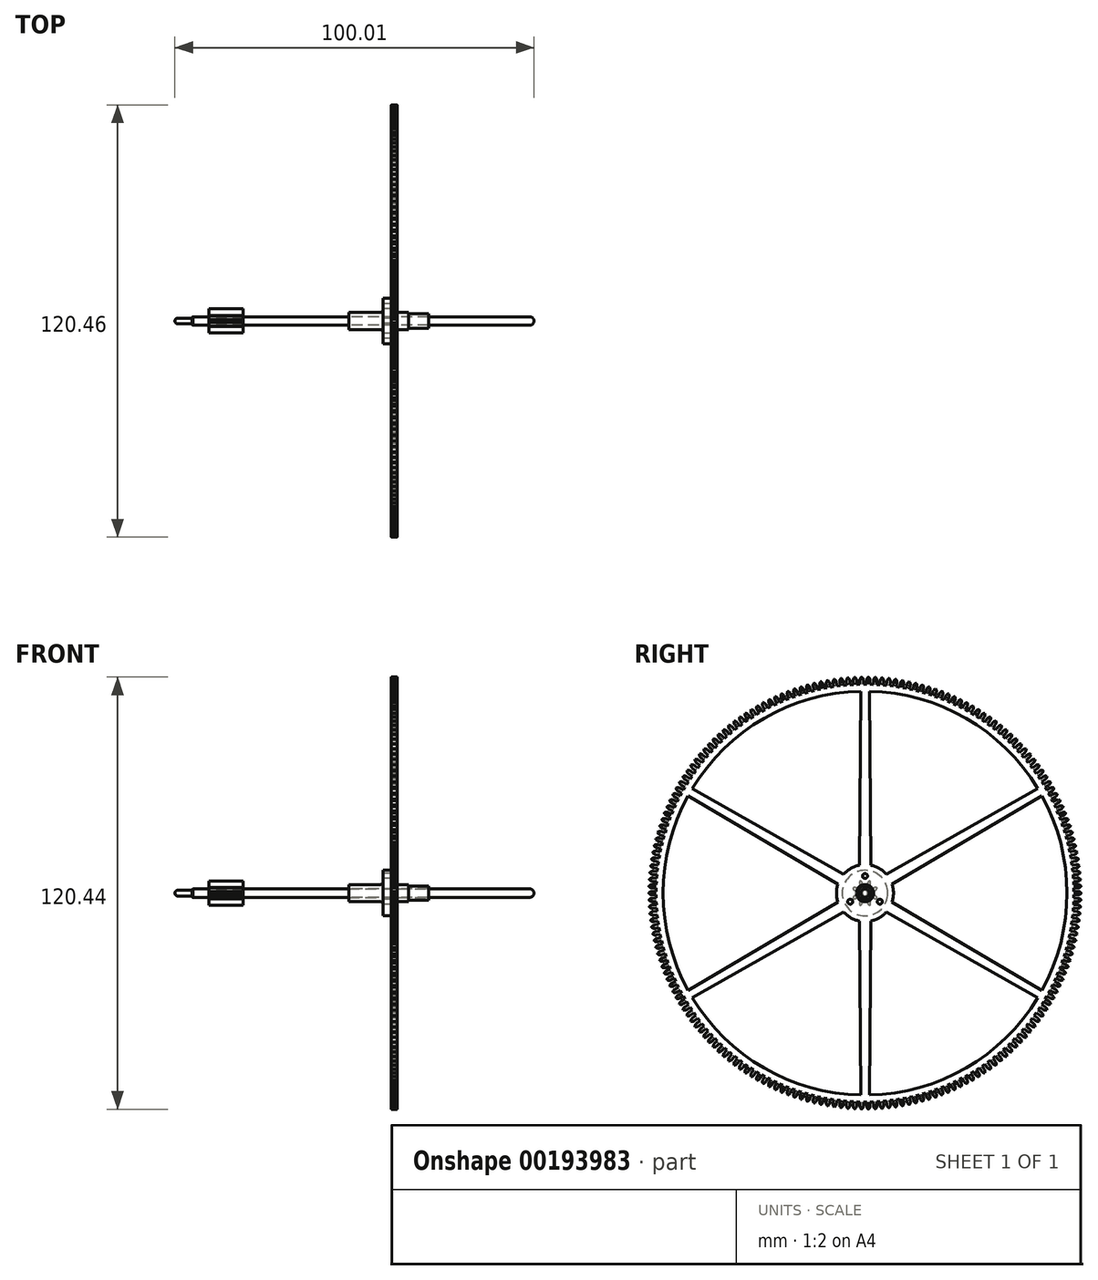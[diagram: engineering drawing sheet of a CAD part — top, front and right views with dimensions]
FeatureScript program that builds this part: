
annotation { "Feature Type Name" : "Feature", "Feature Type Description" : "" }
export const myFeature = defineFeature(function(context is Context, id is Id, definition is map)
    precondition{}
    {
        {
            var Q0;
            Q0=qCreatedBy(makeId("Front.planeOp"),FACE);
            var sketch = newSketch(context, id + "F0", { "sketchPlane" : qUnion([Q0])});
            skLineSegment(sketch, "E0", {"start": v(-11.11, 0) * mm, "end": v(-11.11, 1.2) * mm, "construction": true});
            skLineSegment(sketch, "E1", {"start": v(-11.11, 2.38) * mm, "end": v(-1.59, 2.38) * mm});
            skLineSegment(sketch, "E2", {"start": v(-1.59, 2.38) * mm, "end": v(-1.59, 6.35) * mm});
            skLineSegment(sketch, "E3", {"start": v(-1.59, 6.35) * mm, "end": v(0.8, 6.35) * mm});
            skLineSegment(sketch, "E4", {"start": v(0.8, 6.35) * mm, "end": v(0.8, 2.38) * mm});
            skLineSegment(sketch, "E5", {"start": v(11.11, 1.98) * mm, "end": v(11.11, 1.2) * mm});
            skLineSegment(sketch, "E6", {"start": v(11.11, 0) * mm, "end": v(-11.11, 0) * mm, "construction": true});
            skPoint(sketch, "E7", {"position": v(-11.11, 1.2) * mm});
            skPoint(sketch, "E8", {"position": v(11.11, 1.2) * mm});
            skLineSegment(sketch, "E9", {"start": v(-11.11, 1.2) * mm, "end": v(11.11, 1.2) * mm});
            skLineSegment(sketch, "E10", {"start": v(-11.11, 1.2) * mm, "end": v(-11.11, 2.38) * mm});
            skLineSegment(sketch, "E11", {"start": v(11.11, 1.2) * mm, "end": v(11.11, 0) * mm, "construction": true});
            skLineSegment(sketch, "E12", {"start": v(0.8, 2.38) * mm, "end": v(5.56, 2.38) * mm});
            skLineSegment(sketch, "E13", {"start": v(5.56, 2.38) * mm, "end": v(5.56, 1.98) * mm});
            skLineSegment(sketch, "E14", {"start": v(5.56, 1.98) * mm, "end": v(11.11, 1.98) * mm});
            skSolve(sketch);
        }
        {
            var Q0;
            Q0=makeQuery(id+"F0.imprint","IMPRINT",FACE,{"disambiguationData":[TD([[makeQuery(id+"F0.imprint","IMPRINT",EDGE,{"derivedFrom":sQuery(id+"F0.wireOp",EDGE,"E1")}),-1.0]])]});
            var Q1;
            Q1=sQuery(id+"F0.wireOp",EDGE,"E6");
            revolve(context, id + "F1", {"entities" : qUnion([Q0]), "axis" : qUnion([Q1]), "revolveType" : RevolveType.FULL});
        }
        {
            var Q0;
            Q0=makeQuery(id+"F1.opRevolve","SWEPT_FACE",FACE,{"disambiguationData":[OSD([sQuery(id+"F0.wireOp",EDGE,"E2")])]});
            var sketch = newSketch(context, id + "F2", { "sketchPlane" : qUnion([Q0])});
            skCircle(sketch, "E15", {"center": v(0, 4.76) * mm, "radius": 0.7 * mm});
            skCircle(sketch, "E16", {"center": v(0, 0) * mm, "radius": 4.76 * mm, "construction": true});
            skCircle(sketch, "E17.1.0", {"center": v(-4.12, -2.38) * mm, "radius": 0.7 * mm});
            skCircle(sketch, "E17.2.0", {"center": v(4.12, -2.38) * mm, "radius": 0.7 * mm});
            skSolve(sketch);
        }
        {
            var Q0;
            Q0=makeQuery(id+"F1.opRevolve","SWEPT_EDGE",EDGE,{"disambiguationData":[OSD([sQuery(id+"F0.wireOp",EDGE,"E1"),sQuery(id+"F0.wireOp",EDGE,"E2")])]});
            fillet(context, id + "F3", {"entities" : qUnion([Q0]), "radius" : 0.8 * mm, "tangentPropagation" : true, "allowEdgeOverflow" : false});
        }
        {
            var Q0;
            Q0=qCreatedBy(makeId("Front.planeOp"),FACE);
            var sketch = newSketch(context, id + "F4", { "sketchPlane" : qUnion([Q0])});
            skLineSegment(sketch, "E18", {"start": v(-54.77, 1.2) * mm, "end": v(40.48, 1.2) * mm});
            skLineSegment(sketch, "E19", {"start": v(-54.77, 1.2) * mm, "end": v(-54.77, 0.8) * mm});
            skLineSegment(sketch, "E20", {"start": v(-54.77, 0.8) * mm, "end": v(-59.53, 0.8) * mm});
            skLineSegment(sketch, "E21", {"start": v(-59.53, 0.8) * mm, "end": v(-59.53, 0) * mm});
            skLineSegment(sketch, "E22", {"start": v(-59.53, 0) * mm, "end": v(40.48, 0) * mm});
            skLineSegment(sketch, "E23", {"start": v(40.48, 0) * mm, "end": v(40.48, 1.2) * mm});
            skSolve(sketch);
        }
        {
            var Q0;
            Q0=makeQuery(id+"F4.imprint","IMPRINT",FACE,{"disambiguationData":[TD([[makeQuery(id+"F4.imprint","IMPRINT",EDGE,{"derivedFrom":sQuery(id+"F4.wireOp",EDGE,"E18")}),-1.0]])]});
            var Q1;
            Q1=sQuery(id+"F4.wireOp",EDGE,"E22");
            revolve(context, id + "F5", {"entities" : qUnion([Q0]), "axis" : qUnion([Q1]), "revolveType" : RevolveType.FULL});
        }
        {
            var Q0;
            Q0=makeQuery(id+"F5.opRevolve","SWEPT_EDGE",EDGE,{"disambiguationData":[OSD([sQuery(id+"F4.wireOp",EDGE,"E20"),sQuery(id+"F4.wireOp",EDGE,"E21")])]});
            fillet(context, id + "F6", {"entities" : qUnion([Q0]), "radius" : 0.8 * mm, "tangentPropagation" : true, "allowEdgeOverflow" : false});
        }
        {
            var Q0;
            Q0=makeQuery(id+"F5.opRevolve","SWEPT_EDGE",EDGE,{"disambiguationData":[OSD([sQuery(id+"F4.wireOp",EDGE,"E18"),sQuery(id+"F4.wireOp",EDGE,"E19")])]});
            chamfer(context, id + "F7", {"entities" : qUnion([Q0]), "width" : 0.2 * mm, "tangentPropagation" : true});
        }
        {
            var Q0;
            Q0=makeQuery(id+"F5.opRevolve","SWEPT_EDGE",EDGE,{"disambiguationData":[OSD([sQuery(id+"F4.wireOp",EDGE,"E18"),sQuery(id+"F4.wireOp",EDGE,"E23")])]});
            fillet(context, id + "F8", {"entities" : qUnion([Q0]), "radius" : 1.2 * mm, "tangentPropagation" : true, "allowEdgeOverflow" : false});
        }
        {
            var Q0;
            Q0=makeQuery(id+"F2.imprint","IMPRINT",FACE,{"disambiguationData":[TD([[makeQuery(id+"F2.imprint","IMPRINT",EDGE,{"derivedFrom":sQuery(id+"F2.wireOp",EDGE,"E15")}),1.0]])]});
            var Q1;
            Q1=makeQuery(id+"F2.imprint","IMPRINT",FACE,{"disambiguationData":[TD([[makeQuery(id+"F2.imprint","IMPRINT",EDGE,{"derivedFrom":sQuery(id+"F2.wireOp",EDGE,"E17.2.0")}),1.0]])]});
            var Q2;
            Q2=makeQuery(id+"F2.imprint","IMPRINT",FACE,{"disambiguationData":[TD([[makeQuery(id+"F2.imprint","IMPRINT",EDGE,{"derivedFrom":sQuery(id+"F2.wireOp",EDGE,"E17.1.0")}),1.0]])]});
            extrude(context, id + "F9", {"entities" : qUnion([Q0, Q1, Q2]), "operationType" : NewBodyOperationType.REMOVE, "endBound" : BoundingType.UP_TO_NEXT, "oppositeDirection" : true, "depth" : 25.4 * mm});
        }
        {
            var Q0;
            Q0=makeQuery(id+"F5.opRevolve","SWEPT_FACE",FACE,{"disambiguationData":[OSD([sQuery(id+"F4.wireOp",EDGE,"E19")])]});
            cPlane(context, id + "F10", {"entities" : qUnion([Q0]), "cplaneType" : CPlaneType.OFFSET, "offset" : 4.76 * mm, "oppositeDirection" : true, "width" : 152.4 * mm, "height" : 152.4 * mm});
        }
        {
            var Q0;
            Q0=qCreatedBy(id+"F10.planeOp",FACE);
            var sketch = newSketch(context, id + "F11", { "sketchPlane" : qUnion([Q0])});
            skCircle(sketch, "E24", {"center": v(0, 0) * mm, "radius": 1.2 * mm});
            skCircle(sketch, "E25", {"center": v(0, 0) * mm, "radius": 1.57 * mm, "construction": true});
            skCircle(sketch, "E26", {"center": v(0, 0) * mm, "radius": 3.64 * mm, "construction": true});
            skCircle(sketch, "E27", {"center": v(0, 0) * mm, "radius": 3 * mm, "construction": true});
            skLineSegment(sketch, "E28", {"start": v(0, 0) * mm, "end": v(0, 3.64) * mm, "construction": true});
            skLineSegment(sketch, "E29", {"start": v(0, 0) * mm, "end": v(2.57, 2.57) * mm, "construction": true});
            skLineSegment(sketch, "E30", {"start": v(0.43, 1.57) * mm, "end": v(0.73, 2.77) * mm});
            skLineSegment(sketch, "E31", {"start": v(0.8, 1.42) * mm, "end": v(1.44, 2.48) * mm});
            skArc(sketch, "E32", {"start": v(1.4, 3.36) * mm, "mid": v(0.97, 3.17) * mm, "end": v(0.73, 2.77) * mm});
            skArc(sketch, "E33", {"start": v(1.44, 2.48) * mm, "mid": v(1.56, 2.93) * mm, "end": v(1.4, 3.36) * mm});
            skLineSegment(sketch, "E34", {"start": v(0, 0) * mm, "end": v(1.4, 3.36) * mm, "construction": true});
            skLineSegment(sketch, "E35", {"start": v(0.77, 2.9) * mm, "end": v(1.5, 2.6) * mm, "construction": true});
            skPoint(sketch, "E36", {"position": v(1.14, 2.75) * mm});
            skLineSegment(sketch, "E37", {"start": v(0.43, 1.57) * mm, "end": v(0, 1.57) * mm});
            skLineSegment(sketch, "E38", {"start": v(0.8, 1.42) * mm, "end": v(1.11, 1.11) * mm});
            skLineSegment(sketch, "E39.1.0", {"start": v(-0.8, 1.42) * mm, "end": v(-1.11, 1.11) * mm});
            skLineSegment(sketch, "E39.1.1", {"start": v(-0.8, 1.42) * mm, "end": v(-1.44, 2.48) * mm});
            skArc(sketch, "E39.1.2", {"start": v(-1.4, 3.36) * mm, "mid": v(-1.56, 2.93) * mm, "end": v(-1.44, 2.48) * mm});
            skArc(sketch, "E39.1.3", {"start": v(-0.73, 2.77) * mm, "mid": v(-0.97, 3.17) * mm, "end": v(-1.4, 3.36) * mm});
            skLineSegment(sketch, "E39.1.4", {"start": v(-0.43, 1.57) * mm, "end": v(-0.73, 2.77) * mm});
            skLineSegment(sketch, "E39.1.5", {"start": v(-0.43, 1.57) * mm, "end": v(0, 1.57) * mm});
            skLineSegment(sketch, "E39.2.0", {"start": v(-1.57, 0.43) * mm, "end": v(-1.57, 0) * mm});
            skLineSegment(sketch, "E39.2.1", {"start": v(-1.57, 0.43) * mm, "end": v(-2.77, 0.73) * mm});
            skArc(sketch, "E39.2.2", {"start": v(-3.36, 1.4) * mm, "mid": v(-3.17, 0.97) * mm, "end": v(-2.77, 0.73) * mm});
            skArc(sketch, "E39.2.3", {"start": v(-2.48, 1.44) * mm, "mid": v(-2.93, 1.56) * mm, "end": v(-3.36, 1.4) * mm});
            skLineSegment(sketch, "E39.2.4", {"start": v(-1.42, 0.8) * mm, "end": v(-2.48, 1.44) * mm});
            skLineSegment(sketch, "E39.2.5", {"start": v(-1.42, 0.8) * mm, "end": v(-1.11, 1.11) * mm});
            skLineSegment(sketch, "E40.2.3.0", {"start": v(-1.42, -0.8) * mm, "end": v(-1.11, -1.11) * mm});
            skLineSegment(sketch, "E40.3.3.0", {"start": v(-1.42, -0.8) * mm, "end": v(-2.48, -1.44) * mm});
            skArc(sketch, "E40.6.3.0", {"start": v(-3.36, -1.4) * mm, "mid": v(-2.93, -1.56) * mm, "end": v(-2.48, -1.44) * mm});
            skArc(sketch, "E40.10.3.0", {"start": v(-2.77, -0.73) * mm, "mid": v(-3.17, -0.97) * mm, "end": v(-3.36, -1.4) * mm});
            skLineSegment(sketch, "E40.14.3.0", {"start": v(-1.57, -0.43) * mm, "end": v(-2.77, -0.73) * mm});
            skLineSegment(sketch, "E40.17.3.0", {"start": v(-1.57, -0.43) * mm, "end": v(-1.57, 0) * mm});
            skLineSegment(sketch, "E40.2.4.0", {"start": v(-0.43, -1.57) * mm, "end": v(0, -1.57) * mm});
            skLineSegment(sketch, "E40.3.4.0", {"start": v(-0.43, -1.57) * mm, "end": v(-0.73, -2.77) * mm});
            skArc(sketch, "E40.6.4.0", {"start": v(-1.4, -3.36) * mm, "mid": v(-0.97, -3.17) * mm, "end": v(-0.73, -2.77) * mm});
            skArc(sketch, "E40.10.4.0", {"start": v(-1.44, -2.48) * mm, "mid": v(-1.56, -2.93) * mm, "end": v(-1.4, -3.36) * mm});
            skLineSegment(sketch, "E40.14.4.0", {"start": v(-0.8, -1.42) * mm, "end": v(-1.44, -2.48) * mm});
            skLineSegment(sketch, "E40.17.4.0", {"start": v(-0.8, -1.42) * mm, "end": v(-1.11, -1.11) * mm});
            skLineSegment(sketch, "E40.2.5.0", {"start": v(0.8, -1.42) * mm, "end": v(1.11, -1.11) * mm});
            skLineSegment(sketch, "E40.3.5.0", {"start": v(0.8, -1.42) * mm, "end": v(1.44, -2.48) * mm});
            skArc(sketch, "E40.6.5.0", {"start": v(1.4, -3.36) * mm, "mid": v(1.56, -2.93) * mm, "end": v(1.44, -2.48) * mm});
            skArc(sketch, "E40.10.5.0", {"start": v(0.73, -2.77) * mm, "mid": v(0.97, -3.17) * mm, "end": v(1.4, -3.36) * mm});
            skLineSegment(sketch, "E40.14.5.0", {"start": v(0.43, -1.57) * mm, "end": v(0.73, -2.77) * mm});
            skLineSegment(sketch, "E40.17.5.0", {"start": v(0.43, -1.57) * mm, "end": v(0, -1.57) * mm});
            skLineSegment(sketch, "E40.2.6.0", {"start": v(1.57, -0.43) * mm, "end": v(1.57, 0) * mm});
            skLineSegment(sketch, "E40.3.6.0", {"start": v(1.57, -0.43) * mm, "end": v(2.77, -0.73) * mm});
            skArc(sketch, "E40.6.6.0", {"start": v(3.36, -1.4) * mm, "mid": v(3.17, -0.97) * mm, "end": v(2.77, -0.73) * mm});
            skArc(sketch, "E40.10.6.0", {"start": v(2.48, -1.44) * mm, "mid": v(2.93, -1.56) * mm, "end": v(3.36, -1.4) * mm});
            skLineSegment(sketch, "E40.14.6.0", {"start": v(1.42, -0.8) * mm, "end": v(2.48, -1.44) * mm});
            skLineSegment(sketch, "E40.17.6.0", {"start": v(1.42, -0.8) * mm, "end": v(1.11, -1.11) * mm});
            skLineSegment(sketch, "E40.2.7.0", {"start": v(1.42, 0.8) * mm, "end": v(1.11, 1.11) * mm});
            skLineSegment(sketch, "E40.3.7.0", {"start": v(1.42, 0.8) * mm, "end": v(2.48, 1.44) * mm});
            skArc(sketch, "E40.6.7.0", {"start": v(3.36, 1.4) * mm, "mid": v(2.93, 1.56) * mm, "end": v(2.48, 1.44) * mm});
            skArc(sketch, "E40.10.7.0", {"start": v(2.77, 0.73) * mm, "mid": v(3.17, 0.97) * mm, "end": v(3.36, 1.4) * mm});
            skLineSegment(sketch, "E40.14.7.0", {"start": v(1.57, 0.43) * mm, "end": v(2.77, 0.73) * mm});
            skLineSegment(sketch, "E40.17.7.0", {"start": v(1.57, 0.43) * mm, "end": v(1.57, 0) * mm});
            skSolve(sketch);
        }
        {
            var Q0;
            Q0=makeQuery(id+"F11.imprint","IMPRINT",FACE,{"disambiguationData":[TD([[makeQuery(id+"F11.imprint","IMPRINT",EDGE,{"derivedFrom":sQuery(id+"F11.wireOp",EDGE,"E24")}),-1.0]])]});
            extrude(context, id + "F12", {"entities" : qUnion([Q0]), "oppositeDirection" : true, "depth" : 9.52 * mm});
        }
        {
            var Q0;
            Q0=makeQuery(id+"F1.opRevolve","SWEPT_FACE",FACE,{"disambiguationData":[OSD([sQuery(id+"F0.wireOp",EDGE,"E4")])]});
            var sketch = newSketch(context, id + "F13", { "sketchPlane" : qUnion([Q0])});
            skCircle(sketch, "E41", {"center": v(0, 0) * mm, "radius": 2.38 * mm});
            skArc(sketch, "E42", {"start": v(7.53, -2.51) * mm, "mid": v(7.94, 0) * mm, "end": v(7.53, 2.51) * mm});
            skCircle(sketch, "E43", {"center": v(0, 4.76) * mm, "radius": 0.7 * mm});
            skCircle(sketch, "E44.1.0", {"center": v(-4.12, -2.38) * mm, "radius": 0.7 * mm});
            skCircle(sketch, "E44.2.0", {"center": v(4.12, -2.38) * mm, "radius": 0.7 * mm});
            skCircle(sketch, "E45", {"center": v(0, 0) * mm, "radius": 60.23 * mm, "construction": true});
            skCircle(sketch, "E46", {"center": v(0, 0) * mm, "radius": 59.4 * mm, "construction": true});
            skCircle(sketch, "E47", {"center": v(0, 0) * mm, "radius": 58.2 * mm, "construction": true});
            skArc(sketch, "E48", {"start": v(-1.2, 56.25) * mm, "mid": v(-28.13, 48.72) * mm, "end": v(-48.12, 29.15) * mm});
            skLineSegment(sketch, "E49", {"start": v(0, 0) * mm, "end": v(0, 60.23) * mm, "construction": true});
            skLineSegment(sketch, "E50", {"start": v(0, 0) * mm, "end": v(0.96, 60.22) * mm, "construction": true});
            skLineSegment(sketch, "E51", {"start": v(0, 0) * mm, "end": v(1.91, 60.2) * mm, "construction": true});
            skLineSegment(sketch, "E52", {"start": v(-1.59, 7.78) * mm, "end": v(-1.2, 56.25) * mm});
            skLineSegment(sketch, "E53", {"start": v(1.59, 7.78) * mm, "end": v(1.2, 56.25) * mm});
            skLineSegment(sketch, "E54", {"start": v(-1.2, 56.25) * mm, "end": v(1.2, 56.25) * mm, "construction": true});
            skLineSegment(sketch, "E55", {"start": v(-1.59, 7.78) * mm, "end": v(1.59, 7.78) * mm, "construction": true});
            skPoint(sketch, "E56", {"position": v(0, 7.78) * mm});
            skPoint(sketch, "E57", {"position": v(0, 56.25) * mm});
            skLineSegment(sketch, "E58.1.0", {"start": v(-7.53, 2.51) * mm, "end": v(-49.3, 27.1) * mm});
            skLineSegment(sketch, "E58.1.1", {"start": v(-5.94, 5.26) * mm, "end": v(-48.12, 29.15) * mm});
            skLineSegment(sketch, "E58.2.0", {"start": v(-5.94, -5.26) * mm, "end": v(-48.12, -29.15) * mm});
            skLineSegment(sketch, "E58.2.1", {"start": v(-7.53, -2.51) * mm, "end": v(-49.3, -27.1) * mm});
            skLineSegment(sketch, "E59.1.3.0", {"start": v(1.59, -7.78) * mm, "end": v(1.2, -56.25) * mm});
            skLineSegment(sketch, "E59.3.3.0", {"start": v(-1.59, -7.78) * mm, "end": v(-1.2, -56.25) * mm});
            skLineSegment(sketch, "E59.1.4.0", {"start": v(7.53, -2.51) * mm, "end": v(49.3, -27.1) * mm});
            skLineSegment(sketch, "E59.3.4.0", {"start": v(5.94, -5.26) * mm, "end": v(48.12, -29.15) * mm});
            skLineSegment(sketch, "E59.1.5.0", {"start": v(5.94, 5.26) * mm, "end": v(48.12, 29.15) * mm});
            skLineSegment(sketch, "E59.3.5.0", {"start": v(7.53, 2.51) * mm, "end": v(49.3, 27.1) * mm});
            skLineSegment(sketch, "E60", {"start": v(0.47, 58.2) * mm, "end": v(0.46, 59.27) * mm});
            skLineSegment(sketch, "E61", {"start": v(1.38, 58.19) * mm, "end": v(1.42, 59.26) * mm});
            skLineSegment(sketch, "E62", {"start": v(0.47, 58.2) * mm, "end": v(0, 58.2) * mm});
            skLineSegment(sketch, "E63", {"start": v(1.38, 58.19) * mm, "end": v(1.85, 58.17) * mm});
            skArc(sketch, "E64", {"start": v(0.96, 60.22) * mm, "mid": v(0.6, 59.8) * mm, "end": v(0.46, 59.27) * mm});
            skArc(sketch, "E65", {"start": v(1.42, 59.26) * mm, "mid": v(1.3, 59.8) * mm, "end": v(0.96, 60.22) * mm});
            skLineSegment(sketch, "E66", {"start": v(0.47, 59.4) * mm, "end": v(1.41, 59.38) * mm, "construction": true});
            skPoint(sketch, "E67", {"position": v(0.94, 59.4) * mm});
            skLineSegment(sketch, "E68.1.0", {"start": v(-1.38, 58.19) * mm, "end": v(-1.85, 58.17) * mm});
            skLineSegment(sketch, "E68.1.1", {"start": v(-1.38, 58.19) * mm, "end": v(-1.42, 59.26) * mm});
            skArc(sketch, "E68.1.2", {"start": v(-0.96, 60.22) * mm, "mid": v(-1.3, 59.8) * mm, "end": v(-1.42, 59.26) * mm});
            skArc(sketch, "E68.1.3", {"start": v(-0.46, 59.27) * mm, "mid": v(-0.6, 59.8) * mm, "end": v(-0.96, 60.22) * mm});
            skLineSegment(sketch, "E68.1.4", {"start": v(-0.47, 58.2) * mm, "end": v(-0.46, 59.27) * mm});
            skLineSegment(sketch, "E68.1.5", {"start": v(-0.47, 58.2) * mm, "end": v(0, 58.2) * mm});
            skArc(sketch, "E69.trimOffspring", {"start": v(48.12, 29.15) * mm, "mid": v(28.13, 48.72) * mm, "end": v(1.2, 56.25) * mm});
            skArc(sketch, "E70.trimOffspring", {"start": v(49.3, -27.1) * mm, "mid": v(56.26, 0) * mm, "end": v(49.3, 27.1) * mm});
            skArc(sketch, "E71.trimOffspring", {"start": v(5.94, 5.26) * mm, "mid": v(3.97, 6.87) * mm, "end": v(1.59, 7.78) * mm});
            skArc(sketch, "E72.trimOffspring", {"start": v(1.59, -7.78) * mm, "mid": v(3.97, -6.87) * mm, "end": v(5.94, -5.26) * mm});
            skArc(sketch, "E73.trimOffspring", {"start": v(1.2, -56.25) * mm, "mid": v(28.13, -48.72) * mm, "end": v(48.12, -29.15) * mm});
            skArc(sketch, "E74.trimOffspring", {"start": v(-48.12, -29.15) * mm, "mid": v(-28.13, -48.72) * mm, "end": v(-1.2, -56.25) * mm});
            skArc(sketch, "E75.trimOffspring", {"start": v(-5.94, -5.26) * mm, "mid": v(-3.97, -6.87) * mm, "end": v(-1.59, -7.78) * mm});
            skArc(sketch, "E76.trimOffspring", {"start": v(-7.53, 2.51) * mm, "mid": v(-7.94, 0) * mm, "end": v(-7.53, -2.51) * mm});
            skArc(sketch, "E77.trimOffspring", {"start": v(-49.3, 27.1) * mm, "mid": v(-56.26, 0) * mm, "end": v(-49.3, -27.1) * mm});
            skArc(sketch, "E78.trimOffspring", {"start": v(-1.59, 7.78) * mm, "mid": v(-3.97, 6.87) * mm, "end": v(-5.94, 5.26) * mm});
            skLineSegment(sketch, "E79.2.2.0", {"start": v(-3.23, 58.11) * mm, "end": v(-3.7, 58.08) * mm});
            skLineSegment(sketch, "E79.3.2.0", {"start": v(-3.23, 58.11) * mm, "end": v(-3.3, 59.18) * mm});
            skArc(sketch, "E79.6.2.0", {"start": v(-2.87, 60.16) * mm, "mid": v(-3.2, 59.72) * mm, "end": v(-3.3, 59.18) * mm});
            skArc(sketch, "E79.10.2.0", {"start": v(-2.35, 59.23) * mm, "mid": v(-2.5, 59.76) * mm, "end": v(-2.87, 60.16) * mm});
            skLineSegment(sketch, "E79.14.2.0", {"start": v(-2.31, 58.16) * mm, "end": v(-2.35, 59.23) * mm});
            skLineSegment(sketch, "E79.17.2.0", {"start": v(-2.31, 58.16) * mm, "end": v(-1.85, 58.17) * mm});
            skLineSegment(sketch, "E80.2.3.0", {"start": v(-5.07, 57.98) * mm, "end": v(-5.53, 57.94) * mm});
            skLineSegment(sketch, "E80.3.3.0", {"start": v(-5.07, 57.98) * mm, "end": v(-5.17, 59.05) * mm});
            skArc(sketch, "E80.6.3.0", {"start": v(-4.77, 60.04) * mm, "mid": v(-5.1, 59.6) * mm, "end": v(-5.17, 59.05) * mm});
            skArc(sketch, "E80.10.3.0", {"start": v(-4.22, 59.12) * mm, "mid": v(-4.39, 59.65) * mm, "end": v(-4.77, 60.04) * mm});
            skLineSegment(sketch, "E80.14.3.0", {"start": v(-4.16, 58.05) * mm, "end": v(-4.22, 59.12) * mm});
            skLineSegment(sketch, "E80.17.3.0", {"start": v(-4.16, 58.05) * mm, "end": v(-3.7, 58.08) * mm});
            skLineSegment(sketch, "E80.2.4.0", {"start": v(-6.9, 57.8) * mm, "end": v(-7.37, 57.73) * mm});
            skLineSegment(sketch, "E80.3.4.0", {"start": v(-6.9, 57.8) * mm, "end": v(-7.04, 58.85) * mm});
            skArc(sketch, "E80.6.4.0", {"start": v(-6.68, 59.86) * mm, "mid": v(-6.98, 59.4) * mm, "end": v(-7.04, 58.85) * mm});
            skArc(sketch, "E80.10.4.0", {"start": v(-6.1, 58.96) * mm, "mid": v(-6.28, 59.48) * mm, "end": v(-6.68, 59.86) * mm});
            skLineSegment(sketch, "E80.14.4.0", {"start": v(-6, 57.9) * mm, "end": v(-6.1, 58.96) * mm});
            skLineSegment(sketch, "E80.17.4.0", {"start": v(-6, 57.9) * mm, "end": v(-5.53, 57.94) * mm});
            skLineSegment(sketch, "E80.2.5.0", {"start": v(-8.74, 57.54) * mm, "end": v(-9.2, 57.47) * mm});
            skLineSegment(sketch, "E80.3.5.0", {"start": v(-8.74, 57.54) * mm, "end": v(-8.9, 58.6) * mm});
            skArc(sketch, "E80.6.5.0", {"start": v(-8.57, 59.62) * mm, "mid": v(-8.86, 59.15) * mm, "end": v(-8.9, 58.6) * mm});
            skArc(sketch, "E80.10.5.0", {"start": v(-7.96, 58.74) * mm, "mid": v(-8.16, 59.25) * mm, "end": v(-8.57, 59.62) * mm});
            skLineSegment(sketch, "E80.14.5.0", {"start": v(-7.83, 57.67) * mm, "end": v(-7.96, 58.74) * mm});
            skLineSegment(sketch, "E80.17.5.0", {"start": v(-7.83, 57.67) * mm, "end": v(-7.37, 57.73) * mm});
            skLineSegment(sketch, "E80.2.6.0", {"start": v(-10.56, 57.24) * mm, "end": v(-11.01, 57.15) * mm});
            skLineSegment(sketch, "E80.3.6.0", {"start": v(-10.56, 57.24) * mm, "end": v(-10.76, 58.29) * mm});
            skArc(sketch, "E80.6.6.0", {"start": v(-10.46, 59.31) * mm, "mid": v(-10.73, 58.84) * mm, "end": v(-10.76, 58.29) * mm});
            skArc(sketch, "E80.10.6.0", {"start": v(-9.82, 58.45) * mm, "mid": v(-10.04, 58.96) * mm, "end": v(-10.46, 59.31) * mm});
            skLineSegment(sketch, "E80.14.6.0", {"start": v(-9.66, 57.4) * mm, "end": v(-9.82, 58.45) * mm});
            skLineSegment(sketch, "E80.17.6.0", {"start": v(-9.66, 57.4) * mm, "end": v(-9.2, 57.47) * mm});
            skLineSegment(sketch, "E80.2.7.0", {"start": v(-12.37, 56.87) * mm, "end": v(-12.82, 56.77) * mm});
            skLineSegment(sketch, "E80.3.7.0", {"start": v(-12.37, 56.87) * mm, "end": v(-12.6, 57.92) * mm});
            skArc(sketch, "E80.6.7.0", {"start": v(-12.34, 58.95) * mm, "mid": v(-12.6, 58.47) * mm, "end": v(-12.6, 57.92) * mm});
            skArc(sketch, "E80.10.7.0", {"start": v(-11.67, 58.11) * mm, "mid": v(-11.9, 58.61) * mm, "end": v(-12.34, 58.95) * mm});
            skLineSegment(sketch, "E80.14.7.0", {"start": v(-11.47, 57.06) * mm, "end": v(-11.67, 58.11) * mm});
            skLineSegment(sketch, "E80.17.7.0", {"start": v(-11.47, 57.06) * mm, "end": v(-11.01, 57.15) * mm});
            skLineSegment(sketch, "E80.2.8.0", {"start": v(-14.17, 56.45) * mm, "end": v(-14.62, 56.33) * mm});
            skLineSegment(sketch, "E80.3.8.0", {"start": v(-14.17, 56.45) * mm, "end": v(-14.44, 57.49) * mm});
            skArc(sketch, "E80.6.8.0", {"start": v(-14.2, 58.53) * mm, "mid": v(-14.44, 58.04) * mm, "end": v(-14.44, 57.49) * mm});
            skArc(sketch, "E80.10.8.0", {"start": v(-13.51, 57.71) * mm, "mid": v(-13.76, 58.2) * mm, "end": v(-14.2, 58.53) * mm});
            skLineSegment(sketch, "E80.14.8.0", {"start": v(-13.28, 56.67) * mm, "end": v(-13.51, 57.71) * mm});
            skLineSegment(sketch, "E80.17.8.0", {"start": v(-13.28, 56.67) * mm, "end": v(-12.82, 56.77) * mm});
            skLineSegment(sketch, "E80.2.9.0", {"start": v(-15.95, 55.97) * mm, "end": v(-16.4, 55.84) * mm});
            skLineSegment(sketch, "E80.3.9.0", {"start": v(-15.95, 55.97) * mm, "end": v(-16.25, 57) * mm});
            skArc(sketch, "E80.6.9.0", {"start": v(-16.05, 58.05) * mm, "mid": v(-16.28, 57.55) * mm, "end": v(-16.25, 57) * mm});
            skArc(sketch, "E80.10.9.0", {"start": v(-15.34, 57.26) * mm, "mid": v(-15.6, 57.74) * mm, "end": v(-16.05, 58.05) * mm});
            skLineSegment(sketch, "E80.14.9.0", {"start": v(-15.07, 56.22) * mm, "end": v(-15.34, 57.26) * mm});
            skLineSegment(sketch, "E80.17.9.0", {"start": v(-15.07, 56.22) * mm, "end": v(-14.62, 56.33) * mm});
            skLineSegment(sketch, "E80.2.10.0", {"start": v(-17.72, 55.44) * mm, "end": v(-18.16, 55.3) * mm});
            skLineSegment(sketch, "E80.3.10.0", {"start": v(-17.72, 55.44) * mm, "end": v(-18.05, 56.46) * mm});
            skArc(sketch, "E80.6.10.0", {"start": v(-17.88, 57.51) * mm, "mid": v(-18.1, 57) * mm, "end": v(-18.05, 56.46) * mm});
            skArc(sketch, "E80.10.10.0", {"start": v(-17.14, 56.74) * mm, "mid": v(-17.42, 57.22) * mm, "end": v(-17.88, 57.51) * mm});
            skLineSegment(sketch, "E80.14.10.0", {"start": v(-16.84, 55.71) * mm, "end": v(-17.14, 56.74) * mm});
            skLineSegment(sketch, "E80.17.10.0", {"start": v(-16.84, 55.71) * mm, "end": v(-16.4, 55.84) * mm});
            skLineSegment(sketch, "E80.2.11.0", {"start": v(-19.47, 54.85) * mm, "end": v(-19.9, 54.7) * mm});
            skLineSegment(sketch, "E80.3.11.0", {"start": v(-19.47, 54.85) * mm, "end": v(-19.84, 55.86) * mm});
            skArc(sketch, "E80.6.11.0", {"start": v(-19.7, 56.92) * mm, "mid": v(-19.9, 56.4) * mm, "end": v(-19.84, 55.86) * mm});
            skArc(sketch, "E80.10.11.0", {"start": v(-18.94, 56.17) * mm, "mid": v(-19.23, 56.63) * mm, "end": v(-19.7, 56.92) * mm});
            skLineSegment(sketch, "E80.14.11.0", {"start": v(-18.6, 55.15) * mm, "end": v(-18.94, 56.17) * mm});
            skLineSegment(sketch, "E80.17.11.0", {"start": v(-18.6, 55.15) * mm, "end": v(-18.16, 55.3) * mm});
            skLineSegment(sketch, "E80.2.12.0", {"start": v(-21.2, 54.2) * mm, "end": v(-21.63, 54.03) * mm});
            skLineSegment(sketch, "E80.3.12.0", {"start": v(-21.2, 54.2) * mm, "end": v(-21.6, 55.2) * mm});
            skArc(sketch, "E80.6.12.0", {"start": v(-21.5, 56.26) * mm, "mid": v(-21.68, 55.74) * mm, "end": v(-21.6, 55.2) * mm});
            skArc(sketch, "E80.10.12.0", {"start": v(-20.7, 55.54) * mm, "mid": v(-21.01, 56) * mm, "end": v(-21.5, 56.26) * mm});
            skLineSegment(sketch, "E80.14.12.0", {"start": v(-20.34, 54.53) * mm, "end": v(-20.7, 55.54) * mm});
            skLineSegment(sketch, "E80.17.12.0", {"start": v(-20.34, 54.53) * mm, "end": v(-19.9, 54.7) * mm});
            skLineSegment(sketch, "E80.2.13.0", {"start": v(-22.9, 53.5) * mm, "end": v(-23.33, 53.32) * mm});
            skLineSegment(sketch, "E80.3.13.0", {"start": v(-22.9, 53.5) * mm, "end": v(-23.34, 54.49) * mm});
            skArc(sketch, "E80.6.13.0", {"start": v(-23.27, 55.55) * mm, "mid": v(-23.43, 55.03) * mm, "end": v(-23.34, 54.49) * mm});
            skArc(sketch, "E80.10.13.0", {"start": v(-22.46, 54.85) * mm, "mid": v(-22.78, 55.3) * mm, "end": v(-23.27, 55.55) * mm});
            skLineSegment(sketch, "E80.14.13.0", {"start": v(-22.06, 53.86) * mm, "end": v(-22.46, 54.85) * mm});
            skLineSegment(sketch, "E80.17.13.0", {"start": v(-22.06, 53.86) * mm, "end": v(-21.63, 54.03) * mm});
            skLineSegment(sketch, "E80.2.14.0", {"start": v(-24.6, 52.75) * mm, "end": v(-25.01, 52.55) * mm});
            skLineSegment(sketch, "E80.3.14.0", {"start": v(-24.6, 52.75) * mm, "end": v(-25.06, 53.72) * mm});
            skArc(sketch, "E80.6.14.0", {"start": v(-25.02, 54.79) * mm, "mid": v(-25.17, 54.26) * mm, "end": v(-25.06, 53.72) * mm});
            skArc(sketch, "E80.10.14.0", {"start": v(-24.19, 54.11) * mm, "mid": v(-24.52, 54.55) * mm, "end": v(-25.02, 54.79) * mm});
            skLineSegment(sketch, "E80.14.14.0", {"start": v(-23.76, 53.13) * mm, "end": v(-24.19, 54.11) * mm});
            skLineSegment(sketch, "E80.17.14.0", {"start": v(-23.76, 53.13) * mm, "end": v(-23.33, 53.32) * mm});
            skLineSegment(sketch, "E80.2.15.0", {"start": v(-26.25, 51.94) * mm, "end": v(-26.67, 51.73) * mm});
            skLineSegment(sketch, "E80.3.15.0", {"start": v(-26.25, 51.94) * mm, "end": v(-26.75, 52.9) * mm});
            skArc(sketch, "E80.6.15.0", {"start": v(-26.75, 53.96) * mm, "mid": v(-26.88, 53.43) * mm, "end": v(-26.75, 52.9) * mm});
            skArc(sketch, "E80.10.15.0", {"start": v(-25.9, 53.32) * mm, "mid": v(-26.24, 53.75) * mm, "end": v(-26.75, 53.96) * mm});
            skLineSegment(sketch, "E80.14.15.0", {"start": v(-25.44, 52.35) * mm, "end": v(-25.9, 53.32) * mm});
            skLineSegment(sketch, "E80.17.15.0", {"start": v(-25.44, 52.35) * mm, "end": v(-25.01, 52.55) * mm});
            skLineSegment(sketch, "E80.2.16.0", {"start": v(-27.89, 51.08) * mm, "end": v(-28.3, 50.86) * mm});
            skLineSegment(sketch, "E80.3.16.0", {"start": v(-27.89, 51.08) * mm, "end": v(-28.41, 52.02) * mm});
            skArc(sketch, "E80.6.16.0", {"start": v(-28.44, 53.09) * mm, "mid": v(-28.56, 52.55) * mm, "end": v(-28.41, 52.02) * mm});
            skArc(sketch, "E80.10.16.0", {"start": v(-27.57, 52.47) * mm, "mid": v(-27.93, 52.89) * mm, "end": v(-28.44, 53.09) * mm});
            skLineSegment(sketch, "E80.14.16.0", {"start": v(-27.08, 51.52) * mm, "end": v(-27.57, 52.47) * mm});
            skLineSegment(sketch, "E80.17.16.0", {"start": v(-27.08, 51.52) * mm, "end": v(-26.67, 51.73) * mm});
            skLineSegment(sketch, "E80.2.17.0", {"start": v(-29.5, 50.17) * mm, "end": v(-29.9, 49.93) * mm});
            skLineSegment(sketch, "E80.3.17.0", {"start": v(-29.5, 50.17) * mm, "end": v(-30.05, 51.1) * mm});
            skArc(sketch, "E80.6.17.0", {"start": v(-30.11, 52.16) * mm, "mid": v(-30.21, 51.62) * mm, "end": v(-30.05, 51.1) * mm});
            skArc(sketch, "E80.10.17.0", {"start": v(-29.22, 51.57) * mm, "mid": v(-29.6, 51.97) * mm, "end": v(-30.11, 52.16) * mm});
            skLineSegment(sketch, "E80.14.17.0", {"start": v(-28.7, 50.63) * mm, "end": v(-29.22, 51.57) * mm});
            skLineSegment(sketch, "E80.17.17.0", {"start": v(-28.7, 50.63) * mm, "end": v(-28.3, 50.86) * mm});
            skLineSegment(sketch, "E80.2.18.0", {"start": v(-31.07, 49.21) * mm, "end": v(-31.47, 48.96) * mm});
            skLineSegment(sketch, "E80.3.18.0", {"start": v(-31.07, 49.21) * mm, "end": v(-31.65, 50.11) * mm});
            skArc(sketch, "E80.6.18.0", {"start": v(-31.75, 51.18) * mm, "mid": v(-31.83, 50.63) * mm, "end": v(-31.65, 50.11) * mm});
            skArc(sketch, "E80.10.18.0", {"start": v(-30.85, 50.62) * mm, "mid": v(-31.23, 51) * mm, "end": v(-31.75, 51.18) * mm});
            skLineSegment(sketch, "E80.14.18.0", {"start": v(-30.3, 49.7) * mm, "end": v(-30.85, 50.62) * mm});
            skLineSegment(sketch, "E80.17.18.0", {"start": v(-30.3, 49.7) * mm, "end": v(-29.9, 49.93) * mm});
            skLineSegment(sketch, "E80.2.19.0", {"start": v(-32.62, 48.2) * mm, "end": v(-33, 47.94) * mm});
            skLineSegment(sketch, "E80.3.19.0", {"start": v(-32.62, 48.2) * mm, "end": v(-33.23, 49.08) * mm});
            skArc(sketch, "E80.6.19.0", {"start": v(-33.36, 50.14) * mm, "mid": v(-33.42, 49.6) * mm, "end": v(-33.23, 49.08) * mm});
            skArc(sketch, "E80.10.19.0", {"start": v(-32.44, 49.61) * mm, "mid": v(-32.83, 50) * mm, "end": v(-33.36, 50.14) * mm});
            skLineSegment(sketch, "E80.14.19.0", {"start": v(-31.86, 48.7) * mm, "end": v(-32.44, 49.61) * mm});
            skLineSegment(sketch, "E80.17.19.0", {"start": v(-31.86, 48.7) * mm, "end": v(-31.47, 48.96) * mm});
            skLineSegment(sketch, "E80.2.20.0", {"start": v(-34.13, 47.14) * mm, "end": v(-34.5, 46.87) * mm});
            skLineSegment(sketch, "E80.3.20.0", {"start": v(-34.13, 47.14) * mm, "end": v(-34.77, 48) * mm});
            skArc(sketch, "E80.6.20.0", {"start": v(-34.94, 49.06) * mm, "mid": v(-34.98, 48.51) * mm, "end": v(-34.77, 48) * mm});
            skArc(sketch, "E80.10.20.0", {"start": v(-34, 48.56) * mm, "mid": v(-34.4, 48.92) * mm, "end": v(-34.94, 49.06) * mm});
            skLineSegment(sketch, "E80.14.20.0", {"start": v(-33.39, 47.67) * mm, "end": v(-34, 48.56) * mm});
            skLineSegment(sketch, "E80.17.20.0", {"start": v(-33.39, 47.67) * mm, "end": v(-33, 47.94) * mm});
            skLineSegment(sketch, "E80.2.21.0", {"start": v(-35.61, 46.04) * mm, "end": v(-35.98, 45.75) * mm});
            skLineSegment(sketch, "E80.3.21.0", {"start": v(-35.61, 46.04) * mm, "end": v(-36.27, 46.88) * mm});
            skArc(sketch, "E80.6.21.0", {"start": v(-36.47, 47.93) * mm, "mid": v(-36.5, 47.38) * mm, "end": v(-36.27, 46.88) * mm});
            skArc(sketch, "E80.10.21.0", {"start": v(-35.52, 47.45) * mm, "mid": v(-35.94, 47.8) * mm, "end": v(-36.47, 47.93) * mm});
            skLineSegment(sketch, "E80.14.21.0", {"start": v(-34.88, 46.6) * mm, "end": v(-35.52, 47.45) * mm});
            skLineSegment(sketch, "E80.17.21.0", {"start": v(-34.88, 46.6) * mm, "end": v(-34.5, 46.87) * mm});
            skLineSegment(sketch, "E80.2.22.0", {"start": v(-37.05, 44.88) * mm, "end": v(-37.41, 44.58) * mm});
            skLineSegment(sketch, "E80.3.22.0", {"start": v(-37.05, 44.88) * mm, "end": v(-37.74, 45.7) * mm});
            skArc(sketch, "E80.6.22.0", {"start": v(-37.98, 46.75) * mm, "mid": v(-37.99, 46.2) * mm, "end": v(-37.74, 45.7) * mm});
            skArc(sketch, "E80.10.22.0", {"start": v(-37, 46.3) * mm, "mid": v(-37.44, 46.64) * mm, "end": v(-37.98, 46.75) * mm});
            skLineSegment(sketch, "E80.14.22.0", {"start": v(-36.34, 45.46) * mm, "end": v(-37, 46.3) * mm});
            skLineSegment(sketch, "E80.17.22.0", {"start": v(-36.34, 45.46) * mm, "end": v(-35.98, 45.75) * mm});
            skLineSegment(sketch, "E80.2.23.0", {"start": v(-38.46, 43.69) * mm, "end": v(-38.8, 43.37) * mm});
            skLineSegment(sketch, "E80.3.23.0", {"start": v(-38.46, 43.69) * mm, "end": v(-39.17, 44.48) * mm});
            skArc(sketch, "E80.6.23.0", {"start": v(-39.44, 45.52) * mm, "mid": v(-39.43, 44.97) * mm, "end": v(-39.17, 44.48) * mm});
            skArc(sketch, "E80.10.23.0", {"start": v(-38.46, 45.1) * mm, "mid": v(-38.9, 45.43) * mm, "end": v(-39.44, 45.52) * mm});
            skLineSegment(sketch, "E80.14.23.0", {"start": v(-37.77, 44.28) * mm, "end": v(-38.46, 45.1) * mm});
            skLineSegment(sketch, "E80.17.23.0", {"start": v(-37.77, 44.28) * mm, "end": v(-37.41, 44.58) * mm});
            skLineSegment(sketch, "E80.2.24.0", {"start": v(-39.82, 42.44) * mm, "end": v(-40.16, 42.12) * mm});
            skLineSegment(sketch, "E80.3.24.0", {"start": v(-39.82, 42.44) * mm, "end": v(-40.57, 43.22) * mm});
            skArc(sketch, "E80.6.24.0", {"start": v(-40.87, 44.24) * mm, "mid": v(-40.84, 43.7) * mm, "end": v(-40.57, 43.22) * mm});
            skArc(sketch, "E80.10.24.0", {"start": v(-39.87, 43.86) * mm, "mid": v(-40.32, 44.18) * mm, "end": v(-40.87, 44.24) * mm});
            skLineSegment(sketch, "E80.14.24.0", {"start": v(-39.15, 43.06) * mm, "end": v(-39.87, 43.86) * mm});
            skLineSegment(sketch, "E80.17.24.0", {"start": v(-39.15, 43.06) * mm, "end": v(-38.8, 43.37) * mm});
            skLineSegment(sketch, "E80.2.25.0", {"start": v(-41.15, 41.16) * mm, "end": v(-41.48, 40.83) * mm});
            skLineSegment(sketch, "E80.3.25.0", {"start": v(-41.15, 41.16) * mm, "end": v(-41.92, 41.9) * mm});
            skArc(sketch, "E80.6.25.0", {"start": v(-42.25, 42.92) * mm, "mid": v(-42.2, 42.38) * mm, "end": v(-41.92, 41.9) * mm});
            skArc(sketch, "E80.10.25.0", {"start": v(-41.24, 42.58) * mm, "mid": v(-41.7, 42.87) * mm, "end": v(-42.25, 42.92) * mm});
            skLineSegment(sketch, "E80.14.25.0", {"start": v(-40.5, 41.8) * mm, "end": v(-41.24, 42.58) * mm});
            skLineSegment(sketch, "E80.17.25.0", {"start": v(-40.5, 41.8) * mm, "end": v(-40.16, 42.12) * mm});
            skLineSegment(sketch, "E80.2.26.0", {"start": v(-42.44, 39.83) * mm, "end": v(-42.75, 39.49) * mm});
            skLineSegment(sketch, "E80.3.26.0", {"start": v(-42.44, 39.83) * mm, "end": v(-43.23, 40.56) * mm});
            skArc(sketch, "E80.6.26.0", {"start": v(-43.59, 41.56) * mm, "mid": v(-43.53, 41.02) * mm, "end": v(-43.23, 40.56) * mm});
            skArc(sketch, "E80.10.26.0", {"start": v(-42.57, 41.25) * mm, "mid": v(-43.04, 41.53) * mm, "end": v(-43.59, 41.56) * mm});
            skLineSegment(sketch, "E80.14.26.0", {"start": v(-41.8, 40.5) * mm, "end": v(-42.57, 41.25) * mm});
            skLineSegment(sketch, "E80.17.26.0", {"start": v(-41.8, 40.5) * mm, "end": v(-41.48, 40.83) * mm});
            skLineSegment(sketch, "E80.2.27.0", {"start": v(-43.68, 38.47) * mm, "end": v(-43.98, 38.11) * mm});
            skLineSegment(sketch, "E80.3.27.0", {"start": v(-43.68, 38.47) * mm, "end": v(-44.5, 39.17) * mm});
            skArc(sketch, "E80.6.27.0", {"start": v(-44.89, 40.16) * mm, "mid": v(-44.8, 39.61) * mm, "end": v(-44.5, 39.17) * mm});
            skArc(sketch, "E80.10.27.0", {"start": v(-43.86, 39.88) * mm, "mid": v(-44.34, 40.14) * mm, "end": v(-44.89, 40.16) * mm});
            skLineSegment(sketch, "E80.14.27.0", {"start": v(-43.07, 39.15) * mm, "end": v(-43.86, 39.88) * mm});
            skLineSegment(sketch, "E80.17.27.0", {"start": v(-43.07, 39.15) * mm, "end": v(-42.75, 39.49) * mm});
            skLineSegment(sketch, "E80.2.28.0", {"start": v(-44.88, 37.06) * mm, "end": v(-45.17, 36.7) * mm});
            skLineSegment(sketch, "E80.3.28.0", {"start": v(-44.88, 37.06) * mm, "end": v(-45.71, 37.74) * mm});
            skArc(sketch, "E80.6.28.0", {"start": v(-46.14, 38.71) * mm, "mid": v(-46.04, 38.17) * mm, "end": v(-45.71, 37.74) * mm});
            skArc(sketch, "E80.10.28.0", {"start": v(-45.1, 38.46) * mm, "mid": v(-45.59, 38.72) * mm, "end": v(-46.14, 38.71) * mm});
            skLineSegment(sketch, "E80.14.28.0", {"start": v(-44.3, 37.76) * mm, "end": v(-45.1, 38.46) * mm});
            skLineSegment(sketch, "E80.17.28.0", {"start": v(-44.3, 37.76) * mm, "end": v(-43.98, 38.11) * mm});
            skLineSegment(sketch, "E80.2.29.0", {"start": v(-46.03, 35.62) * mm, "end": v(-46.31, 35.25) * mm});
            skLineSegment(sketch, "E80.3.29.0", {"start": v(-46.03, 35.62) * mm, "end": v(-46.89, 36.27) * mm});
            skArc(sketch, "E80.6.29.0", {"start": v(-47.34, 37.23) * mm, "mid": v(-47.23, 36.7) * mm, "end": v(-46.89, 36.27) * mm});
            skArc(sketch, "E80.10.29.0", {"start": v(-46.3, 37.01) * mm, "mid": v(-46.8, 37.25) * mm, "end": v(-47.34, 37.23) * mm});
            skLineSegment(sketch, "E80.14.29.0", {"start": v(-45.47, 36.34) * mm, "end": v(-46.3, 37.01) * mm});
            skLineSegment(sketch, "E80.17.29.0", {"start": v(-45.47, 36.34) * mm, "end": v(-45.17, 36.7) * mm});
            skLineSegment(sketch, "E80.2.30.0", {"start": v(-47.14, 34.14) * mm, "end": v(-47.4, 33.76) * mm});
            skLineSegment(sketch, "E80.3.30.0", {"start": v(-47.14, 34.14) * mm, "end": v(-48.01, 34.76) * mm});
            skArc(sketch, "E80.6.30.0", {"start": v(-48.5, 35.7) * mm, "mid": v(-48.37, 35.18) * mm, "end": v(-48.01, 34.76) * mm});
            skArc(sketch, "E80.10.30.0", {"start": v(-47.45, 35.53) * mm, "mid": v(-47.95, 35.75) * mm, "end": v(-48.5, 35.7) * mm});
            skLineSegment(sketch, "E80.14.30.0", {"start": v(-46.6, 34.88) * mm, "end": v(-47.45, 35.53) * mm});
            skLineSegment(sketch, "E80.17.30.0", {"start": v(-46.6, 34.88) * mm, "end": v(-46.31, 35.25) * mm});
            skLineSegment(sketch, "E80.2.31.0", {"start": v(-48.2, 32.63) * mm, "end": v(-48.46, 32.24) * mm});
            skLineSegment(sketch, "E80.3.31.0", {"start": v(-48.2, 32.63) * mm, "end": v(-49.1, 33.22) * mm});
            skArc(sketch, "E80.6.31.0", {"start": v(-49.6, 34.15) * mm, "mid": v(-49.46, 33.62) * mm, "end": v(-49.1, 33.22) * mm});
            skArc(sketch, "E80.10.31.0", {"start": v(-48.55, 34) * mm, "mid": v(-49.06, 34.2) * mm, "end": v(-49.6, 34.15) * mm});
            skLineSegment(sketch, "E80.14.31.0", {"start": v(-47.68, 33.38) * mm, "end": v(-48.55, 34) * mm});
            skLineSegment(sketch, "E80.17.31.0", {"start": v(-47.68, 33.38) * mm, "end": v(-47.4, 33.76) * mm});
            skLineSegment(sketch, "E80.2.32.0", {"start": v(-49.2, 31.08) * mm, "end": v(-49.45, 30.68) * mm});
            skLineSegment(sketch, "E80.3.32.0", {"start": v(-49.2, 31.08) * mm, "end": v(-50.12, 31.64) * mm});
            skArc(sketch, "E80.6.32.0", {"start": v(-50.67, 32.56) * mm, "mid": v(-50.5, 32.04) * mm, "end": v(-50.12, 31.64) * mm});
            skArc(sketch, "E80.10.32.0", {"start": v(-49.6, 32.45) * mm, "mid": v(-50.12, 32.63) * mm, "end": v(-50.67, 32.56) * mm});
            skLineSegment(sketch, "E80.14.32.0", {"start": v(-48.71, 31.85) * mm, "end": v(-49.6, 32.45) * mm});
            skLineSegment(sketch, "E80.17.32.0", {"start": v(-48.71, 31.85) * mm, "end": v(-48.46, 32.24) * mm});
            skLineSegment(sketch, "E80.2.33.0", {"start": v(-50.17, 29.5) * mm, "end": v(-50.4, 29.1) * mm});
            skLineSegment(sketch, "E80.3.33.0", {"start": v(-50.17, 29.5) * mm, "end": v(-51.1, 30.04) * mm});
            skArc(sketch, "E80.6.33.0", {"start": v(-51.67, 30.94) * mm, "mid": v(-51.5, 30.42) * mm, "end": v(-51.1, 30.04) * mm});
            skArc(sketch, "E80.10.33.0", {"start": v(-50.61, 30.85) * mm, "mid": v(-51.13, 31.03) * mm, "end": v(-51.67, 30.94) * mm});
            skLineSegment(sketch, "E80.14.33.0", {"start": v(-49.7, 30.29) * mm, "end": v(-50.61, 30.85) * mm});
            skLineSegment(sketch, "E80.17.33.0", {"start": v(-49.7, 30.29) * mm, "end": v(-49.45, 30.68) * mm});
            skLineSegment(sketch, "E80.2.34.0", {"start": v(-51.08, 27.9) * mm, "end": v(-51.3, 27.49) * mm});
            skLineSegment(sketch, "E80.3.34.0", {"start": v(-51.08, 27.9) * mm, "end": v(-52.03, 28.4) * mm});
            skArc(sketch, "E80.6.34.0", {"start": v(-52.63, 29.28) * mm, "mid": v(-52.44, 28.77) * mm, "end": v(-52.03, 28.4) * mm});
            skArc(sketch, "E80.10.34.0", {"start": v(-51.56, 29.23) * mm, "mid": v(-52.1, 29.39) * mm, "end": v(-52.63, 29.28) * mm});
            skLineSegment(sketch, "E80.14.34.0", {"start": v(-50.64, 28.7) * mm, "end": v(-51.56, 29.23) * mm});
            skLineSegment(sketch, "E80.17.34.0", {"start": v(-50.64, 28.7) * mm, "end": v(-50.4, 29.1) * mm});
            skLineSegment(sketch, "E80.2.35.0", {"start": v(-51.94, 26.26) * mm, "end": v(-52.15, 25.84) * mm});
            skLineSegment(sketch, "E80.3.35.0", {"start": v(-51.94, 26.26) * mm, "end": v(-52.9, 26.74) * mm});
            skArc(sketch, "E80.6.35.0", {"start": v(-53.53, 27.6) * mm, "mid": v(-53.32, 27.1) * mm, "end": v(-52.9, 26.74) * mm});
            skArc(sketch, "E80.10.35.0", {"start": v(-52.47, 27.58) * mm, "mid": v(-53, 27.72) * mm, "end": v(-53.53, 27.6) * mm});
            skLineSegment(sketch, "E80.14.35.0", {"start": v(-51.52, 27.07) * mm, "end": v(-52.47, 27.58) * mm});
            skLineSegment(sketch, "E80.17.35.0", {"start": v(-51.52, 27.07) * mm, "end": v(-51.3, 27.49) * mm});
            skLineSegment(sketch, "E80.2.36.0", {"start": v(-52.75, 24.6) * mm, "end": v(-52.94, 24.18) * mm});
            skLineSegment(sketch, "E80.3.36.0", {"start": v(-52.75, 24.6) * mm, "end": v(-53.72, 25.05) * mm});
            skArc(sketch, "E80.6.36.0", {"start": v(-54.38, 25.89) * mm, "mid": v(-54.16, 25.39) * mm, "end": v(-53.72, 25.05) * mm});
            skArc(sketch, "E80.10.36.0", {"start": v(-53.31, 25.9) * mm, "mid": v(-53.85, 26.03) * mm, "end": v(-54.38, 25.89) * mm});
            skLineSegment(sketch, "E80.14.36.0", {"start": v(-52.35, 25.43) * mm, "end": v(-53.31, 25.9) * mm});
            skLineSegment(sketch, "E80.17.36.0", {"start": v(-52.35, 25.43) * mm, "end": v(-52.15, 25.84) * mm});
            skLineSegment(sketch, "E80.2.37.0", {"start": v(-53.5, 22.92) * mm, "end": v(-53.68, 22.49) * mm});
            skLineSegment(sketch, "E80.3.37.0", {"start": v(-53.5, 22.92) * mm, "end": v(-54.5, 23.33) * mm});
            skArc(sketch, "E80.6.37.0", {"start": v(-55.18, 24.15) * mm, "mid": v(-54.93, 23.65) * mm, "end": v(-54.5, 23.33) * mm});
            skArc(sketch, "E80.10.37.0", {"start": v(-54.1, 24.2) * mm, "mid": v(-54.65, 24.3) * mm, "end": v(-55.18, 24.15) * mm});
            skLineSegment(sketch, "E80.14.37.0", {"start": v(-53.13, 23.75) * mm, "end": v(-54.1, 24.2) * mm});
            skLineSegment(sketch, "E80.17.37.0", {"start": v(-53.13, 23.75) * mm, "end": v(-52.94, 24.18) * mm});
            skLineSegment(sketch, "E80.2.38.0", {"start": v(-54.2, 21.2) * mm, "end": v(-54.37, 20.77) * mm});
            skLineSegment(sketch, "E80.3.38.0", {"start": v(-54.2, 21.2) * mm, "end": v(-55.2, 21.59) * mm});
            skArc(sketch, "E80.6.38.0", {"start": v(-55.91, 22.38) * mm, "mid": v(-55.66, 21.9) * mm, "end": v(-55.2, 21.59) * mm});
            skArc(sketch, "E80.10.38.0", {"start": v(-54.85, 22.47) * mm, "mid": v(-55.4, 22.56) * mm, "end": v(-55.91, 22.38) * mm});
            skLineSegment(sketch, "E80.14.38.0", {"start": v(-53.86, 22.05) * mm, "end": v(-54.85, 22.47) * mm});
            skLineSegment(sketch, "E80.17.38.0", {"start": v(-53.86, 22.05) * mm, "end": v(-53.68, 22.49) * mm});
            skLineSegment(sketch, "E80.2.39.0", {"start": v(-54.85, 19.48) * mm, "end": v(-55, 19.04) * mm});
            skLineSegment(sketch, "E80.3.39.0", {"start": v(-54.85, 19.48) * mm, "end": v(-55.86, 19.83) * mm});
            skArc(sketch, "E80.6.39.0", {"start": v(-56.6, 20.6) * mm, "mid": v(-56.32, 20.12) * mm, "end": v(-55.86, 19.83) * mm});
            skArc(sketch, "E80.10.39.0", {"start": v(-55.54, 20.72) * mm, "mid": v(-56.08, 20.79) * mm, "end": v(-56.6, 20.6) * mm});
            skLineSegment(sketch, "E80.14.39.0", {"start": v(-54.53, 20.33) * mm, "end": v(-55.54, 20.72) * mm});
            skLineSegment(sketch, "E80.17.39.0", {"start": v(-54.53, 20.33) * mm, "end": v(-54.37, 20.77) * mm});
            skLineSegment(sketch, "E80.2.40.0", {"start": v(-55.44, 17.73) * mm, "end": v(-55.58, 17.28) * mm});
            skLineSegment(sketch, "E80.3.40.0", {"start": v(-55.44, 17.73) * mm, "end": v(-56.46, 18.04) * mm});
            skArc(sketch, "E80.6.40.0", {"start": v(-57.22, 18.8) * mm, "mid": v(-56.93, 18.33) * mm, "end": v(-56.46, 18.04) * mm});
            skArc(sketch, "E80.10.40.0", {"start": v(-56.16, 18.95) * mm, "mid": v(-56.71, 19) * mm, "end": v(-57.22, 18.8) * mm});
            skLineSegment(sketch, "E80.14.40.0", {"start": v(-55.15, 18.6) * mm, "end": v(-56.16, 18.95) * mm});
            skLineSegment(sketch, "E80.17.40.0", {"start": v(-55.15, 18.6) * mm, "end": v(-55, 19.04) * mm});
            skLineSegment(sketch, "E80.2.41.0", {"start": v(-55.97, 15.96) * mm, "end": v(-56.1, 15.5) * mm});
            skLineSegment(sketch, "E80.3.41.0", {"start": v(-55.97, 15.96) * mm, "end": v(-57, 16.24) * mm});
            skArc(sketch, "E80.6.41.0", {"start": v(-57.79, 16.97) * mm, "mid": v(-57.49, 16.5) * mm, "end": v(-57, 16.24) * mm});
            skArc(sketch, "E80.10.41.0", {"start": v(-56.74, 17.16) * mm, "mid": v(-57.29, 17.2) * mm, "end": v(-57.79, 16.97) * mm});
            skLineSegment(sketch, "E80.14.41.0", {"start": v(-55.71, 16.84) * mm, "end": v(-56.74, 17.16) * mm});
            skLineSegment(sketch, "E80.17.41.0", {"start": v(-55.71, 16.84) * mm, "end": v(-55.58, 17.28) * mm});
            skLineSegment(sketch, "E80.2.42.0", {"start": v(-56.45, 14.17) * mm, "end": v(-56.56, 13.72) * mm});
            skLineSegment(sketch, "E80.3.42.0", {"start": v(-56.45, 14.17) * mm, "end": v(-57.5, 14.43) * mm});
            skArc(sketch, "E80.6.42.0", {"start": v(-58.3, 15.13) * mm, "mid": v(-57.98, 14.68) * mm, "end": v(-57.5, 14.43) * mm});
            skArc(sketch, "E80.10.42.0", {"start": v(-57.25, 15.35) * mm, "mid": v(-57.8, 15.36) * mm, "end": v(-58.3, 15.13) * mm});
            skLineSegment(sketch, "E80.14.42.0", {"start": v(-56.22, 15.06) * mm, "end": v(-57.25, 15.35) * mm});
            skLineSegment(sketch, "E80.17.42.0", {"start": v(-56.22, 15.06) * mm, "end": v(-56.1, 15.5) * mm});
            skLineSegment(sketch, "E80.2.43.0", {"start": v(-56.87, 12.38) * mm, "end": v(-56.97, 11.92) * mm});
            skLineSegment(sketch, "E80.3.43.0", {"start": v(-56.87, 12.38) * mm, "end": v(-57.92, 12.6) * mm});
            skArc(sketch, "E80.6.43.0", {"start": v(-58.75, 13.27) * mm, "mid": v(-58.42, 12.83) * mm, "end": v(-57.92, 12.6) * mm});
            skArc(sketch, "E80.10.43.0", {"start": v(-57.71, 13.52) * mm, "mid": v(-58.26, 13.52) * mm, "end": v(-58.75, 13.27) * mm});
            skLineSegment(sketch, "E80.14.43.0", {"start": v(-56.67, 13.27) * mm, "end": v(-57.71, 13.52) * mm});
            skLineSegment(sketch, "E80.17.43.0", {"start": v(-56.67, 13.27) * mm, "end": v(-56.56, 13.72) * mm});
            skLineSegment(sketch, "E80.2.44.0", {"start": v(-57.23, 10.57) * mm, "end": v(-57.32, 10.1) * mm});
            skLineSegment(sketch, "E80.3.44.0", {"start": v(-57.23, 10.57) * mm, "end": v(-58.3, 10.75) * mm});
            skArc(sketch, "E80.6.44.0", {"start": v(-59.14, 11.4) * mm, "mid": v(-58.8, 10.97) * mm, "end": v(-58.3, 10.75) * mm});
            skArc(sketch, "E80.10.44.0", {"start": v(-58.11, 11.68) * mm, "mid": v(-58.66, 11.67) * mm, "end": v(-59.14, 11.4) * mm});
            skLineSegment(sketch, "E80.14.44.0", {"start": v(-57.06, 11.46) * mm, "end": v(-58.11, 11.68) * mm});
            skLineSegment(sketch, "E80.17.44.0", {"start": v(-57.06, 11.46) * mm, "end": v(-56.97, 11.92) * mm});
            skLineSegment(sketch, "E80.2.45.0", {"start": v(-57.54, 8.74) * mm, "end": v(-57.6, 8.28) * mm});
            skLineSegment(sketch, "E80.3.45.0", {"start": v(-57.54, 8.74) * mm, "end": v(-58.6, 8.9) * mm});
            skArc(sketch, "E80.6.45.0", {"start": v(-59.47, 9.52) * mm, "mid": v(-59.11, 9.1) * mm, "end": v(-58.6, 8.9) * mm});
            skArc(sketch, "E80.10.45.0", {"start": v(-58.45, 9.83) * mm, "mid": v(-59, 9.8) * mm, "end": v(-59.47, 9.52) * mm});
            skLineSegment(sketch, "E80.14.45.0", {"start": v(-57.4, 9.65) * mm, "end": v(-58.45, 9.83) * mm});
            skLineSegment(sketch, "E80.17.45.0", {"start": v(-57.4, 9.65) * mm, "end": v(-57.32, 10.1) * mm});
            skLineSegment(sketch, "E80.2.46.0", {"start": v(-57.79, 6.91) * mm, "end": v(-57.84, 6.45) * mm});
            skLineSegment(sketch, "E80.3.46.0", {"start": v(-57.79, 6.91) * mm, "end": v(-58.86, 7.03) * mm});
            skArc(sketch, "E80.6.46.0", {"start": v(-59.74, 7.62) * mm, "mid": v(-59.37, 7.22) * mm, "end": v(-58.86, 7.03) * mm});
            skArc(sketch, "E80.10.46.0", {"start": v(-58.74, 7.98) * mm, "mid": v(-59.28, 7.92) * mm, "end": v(-59.74, 7.62) * mm});
            skLineSegment(sketch, "E80.14.46.0", {"start": v(-57.67, 7.82) * mm, "end": v(-58.74, 7.98) * mm});
            skLineSegment(sketch, "E80.17.46.0", {"start": v(-57.67, 7.82) * mm, "end": v(-57.6, 8.28) * mm});
            skLineSegment(sketch, "E80.2.47.0", {"start": v(-57.98, 5.08) * mm, "end": v(-58.02, 4.61) * mm});
            skLineSegment(sketch, "E80.3.47.0", {"start": v(-57.98, 5.08) * mm, "end": v(-59.05, 5.16) * mm});
            skArc(sketch, "E80.6.47.0", {"start": v(-59.96, 5.73) * mm, "mid": v(-59.57, 5.33) * mm, "end": v(-59.05, 5.16) * mm});
            skArc(sketch, "E80.10.47.0", {"start": v(-58.96, 6.1) * mm, "mid": v(-59.5, 6.04) * mm, "end": v(-59.96, 5.73) * mm});
            skLineSegment(sketch, "E80.14.47.0", {"start": v(-57.9, 5.99) * mm, "end": v(-58.96, 6.1) * mm});
            skLineSegment(sketch, "E80.17.47.0", {"start": v(-57.9, 5.99) * mm, "end": v(-57.84, 6.45) * mm});
            skLineSegment(sketch, "E80.2.48.0", {"start": v(-58.11, 3.24) * mm, "end": v(-58.13, 2.77) * mm});
            skLineSegment(sketch, "E80.3.48.0", {"start": v(-58.11, 3.24) * mm, "end": v(-59.18, 3.28) * mm});
            skArc(sketch, "E80.6.48.0", {"start": v(-60.1, 3.82) * mm, "mid": v(-59.71, 3.44) * mm, "end": v(-59.18, 3.28) * mm});
            skArc(sketch, "E80.10.48.0", {"start": v(-59.12, 4.23) * mm, "mid": v(-59.67, 4.15) * mm, "end": v(-60.1, 3.82) * mm});
            skLineSegment(sketch, "E80.14.48.0", {"start": v(-58.05, 4.15) * mm, "end": v(-59.12, 4.23) * mm});
            skLineSegment(sketch, "E80.17.48.0", {"start": v(-58.05, 4.15) * mm, "end": v(-58.02, 4.61) * mm});
            skLineSegment(sketch, "E80.2.49.0", {"start": v(-58.19, 1.39) * mm, "end": v(-58.2, 0.92) * mm});
            skLineSegment(sketch, "E80.3.49.0", {"start": v(-58.19, 1.39) * mm, "end": v(-59.26, 1.4) * mm});
            skArc(sketch, "E80.6.49.0", {"start": v(-60.2, 1.91) * mm, "mid": v(-59.79, 1.54) * mm, "end": v(-59.26, 1.4) * mm});
            skArc(sketch, "E80.10.49.0", {"start": v(-59.23, 2.36) * mm, "mid": v(-59.77, 2.25) * mm, "end": v(-60.2, 1.91) * mm});
            skLineSegment(sketch, "E80.14.49.0", {"start": v(-58.16, 2.3) * mm, "end": v(-59.23, 2.36) * mm});
            skLineSegment(sketch, "E80.17.49.0", {"start": v(-58.16, 2.3) * mm, "end": v(-58.13, 2.77) * mm});
            skLineSegment(sketch, "E80.2.50.0", {"start": v(-58.2, -0.46) * mm, "end": v(-58.2, -0.92) * mm});
            skLineSegment(sketch, "E80.3.50.0", {"start": v(-58.2, -0.46) * mm, "end": v(-59.27, -0.48) * mm});
            skArc(sketch, "E80.6.50.0", {"start": v(-60.23, 0) * mm, "mid": v(-59.8, -0.35) * mm, "end": v(-59.27, -0.48) * mm});
            skArc(sketch, "E80.10.50.0", {"start": v(-59.27, 0.48) * mm, "mid": v(-59.8, 0.35) * mm, "end": v(-60.23, 0) * mm});
            skLineSegment(sketch, "E80.14.50.0", {"start": v(-58.2, 0.46) * mm, "end": v(-59.27, 0.48) * mm});
            skLineSegment(sketch, "E80.17.50.0", {"start": v(-58.2, 0.46) * mm, "end": v(-58.2, 0.92) * mm});
            skLineSegment(sketch, "E80.2.51.0", {"start": v(-58.16, -2.3) * mm, "end": v(-58.13, -2.77) * mm});
            skLineSegment(sketch, "E80.3.51.0", {"start": v(-58.16, -2.3) * mm, "end": v(-59.23, -2.36) * mm});
            skArc(sketch, "E80.6.51.0", {"start": v(-60.2, -1.91) * mm, "mid": v(-59.77, -2.25) * mm, "end": v(-59.23, -2.36) * mm});
            skArc(sketch, "E80.10.51.0", {"start": v(-59.26, -1.4) * mm, "mid": v(-59.79, -1.54) * mm, "end": v(-60.2, -1.91) * mm});
            skLineSegment(sketch, "E80.14.51.0", {"start": v(-58.19, -1.39) * mm, "end": v(-59.26, -1.4) * mm});
            skLineSegment(sketch, "E80.17.51.0", {"start": v(-58.19, -1.39) * mm, "end": v(-58.2, -0.92) * mm});
            skLineSegment(sketch, "E80.2.52.0", {"start": v(-58.05, -4.15) * mm, "end": v(-58.02, -4.61) * mm});
            skLineSegment(sketch, "E80.3.52.0", {"start": v(-58.05, -4.15) * mm, "end": v(-59.12, -4.23) * mm});
            skArc(sketch, "E80.6.52.0", {"start": v(-60.1, -3.82) * mm, "mid": v(-59.67, -4.15) * mm, "end": v(-59.12, -4.23) * mm});
            skArc(sketch, "E80.10.52.0", {"start": v(-59.18, -3.28) * mm, "mid": v(-59.71, -3.44) * mm, "end": v(-60.1, -3.82) * mm});
            skLineSegment(sketch, "E80.14.52.0", {"start": v(-58.11, -3.24) * mm, "end": v(-59.18, -3.28) * mm});
            skLineSegment(sketch, "E80.17.52.0", {"start": v(-58.11, -3.24) * mm, "end": v(-58.13, -2.77) * mm});
            skLineSegment(sketch, "E80.2.53.0", {"start": v(-57.9, -5.99) * mm, "end": v(-57.84, -6.45) * mm});
            skLineSegment(sketch, "E80.3.53.0", {"start": v(-57.9, -5.99) * mm, "end": v(-58.96, -6.1) * mm});
            skArc(sketch, "E80.6.53.0", {"start": v(-59.96, -5.73) * mm, "mid": v(-59.5, -6.04) * mm, "end": v(-58.96, -6.1) * mm});
            skArc(sketch, "E80.10.53.0", {"start": v(-59.05, -5.16) * mm, "mid": v(-59.57, -5.33) * mm, "end": v(-59.96, -5.73) * mm});
            skLineSegment(sketch, "E80.14.53.0", {"start": v(-57.98, -5.08) * mm, "end": v(-59.05, -5.16) * mm});
            skLineSegment(sketch, "E80.17.53.0", {"start": v(-57.98, -5.08) * mm, "end": v(-58.02, -4.61) * mm});
            skLineSegment(sketch, "E80.2.54.0", {"start": v(-57.67, -7.82) * mm, "end": v(-57.6, -8.28) * mm});
            skLineSegment(sketch, "E80.3.54.0", {"start": v(-57.67, -7.82) * mm, "end": v(-58.74, -7.98) * mm});
            skArc(sketch, "E80.6.54.0", {"start": v(-59.74, -7.62) * mm, "mid": v(-59.28, -7.92) * mm, "end": v(-58.74, -7.98) * mm});
            skArc(sketch, "E80.10.54.0", {"start": v(-58.86, -7.03) * mm, "mid": v(-59.37, -7.22) * mm, "end": v(-59.74, -7.62) * mm});
            skLineSegment(sketch, "E80.14.54.0", {"start": v(-57.79, -6.91) * mm, "end": v(-58.86, -7.03) * mm});
            skLineSegment(sketch, "E80.17.54.0", {"start": v(-57.79, -6.91) * mm, "end": v(-57.84, -6.45) * mm});
            skLineSegment(sketch, "E80.2.55.0", {"start": v(-57.4, -9.65) * mm, "end": v(-57.32, -10.1) * mm});
            skLineSegment(sketch, "E80.3.55.0", {"start": v(-57.4, -9.65) * mm, "end": v(-58.45, -9.83) * mm});
            skArc(sketch, "E80.6.55.0", {"start": v(-59.47, -9.52) * mm, "mid": v(-59, -9.8) * mm, "end": v(-58.45, -9.83) * mm});
            skArc(sketch, "E80.10.55.0", {"start": v(-58.6, -8.9) * mm, "mid": v(-59.11, -9.1) * mm, "end": v(-59.47, -9.52) * mm});
            skLineSegment(sketch, "E80.14.55.0", {"start": v(-57.54, -8.74) * mm, "end": v(-58.6, -8.9) * mm});
            skLineSegment(sketch, "E80.17.55.0", {"start": v(-57.54, -8.74) * mm, "end": v(-57.6, -8.28) * mm});
            skLineSegment(sketch, "E80.2.56.0", {"start": v(-57.06, -11.46) * mm, "end": v(-56.97, -11.92) * mm});
            skLineSegment(sketch, "E80.3.56.0", {"start": v(-57.06, -11.46) * mm, "end": v(-58.11, -11.68) * mm});
            skArc(sketch, "E80.6.56.0", {"start": v(-59.14, -11.4) * mm, "mid": v(-58.66, -11.67) * mm, "end": v(-58.11, -11.68) * mm});
            skArc(sketch, "E80.10.56.0", {"start": v(-58.3, -10.75) * mm, "mid": v(-58.8, -10.97) * mm, "end": v(-59.14, -11.4) * mm});
            skLineSegment(sketch, "E80.14.56.0", {"start": v(-57.23, -10.57) * mm, "end": v(-58.3, -10.75) * mm});
            skLineSegment(sketch, "E80.17.56.0", {"start": v(-57.23, -10.57) * mm, "end": v(-57.32, -10.1) * mm});
            skLineSegment(sketch, "E80.2.57.0", {"start": v(-56.67, -13.27) * mm, "end": v(-56.56, -13.72) * mm});
            skLineSegment(sketch, "E80.3.57.0", {"start": v(-56.67, -13.27) * mm, "end": v(-57.71, -13.52) * mm});
            skArc(sketch, "E80.6.57.0", {"start": v(-58.75, -13.27) * mm, "mid": v(-58.26, -13.52) * mm, "end": v(-57.71, -13.52) * mm});
            skArc(sketch, "E80.10.57.0", {"start": v(-57.92, -12.6) * mm, "mid": v(-58.42, -12.83) * mm, "end": v(-58.75, -13.27) * mm});
            skLineSegment(sketch, "E80.14.57.0", {"start": v(-56.87, -12.38) * mm, "end": v(-57.92, -12.6) * mm});
            skLineSegment(sketch, "E80.17.57.0", {"start": v(-56.87, -12.38) * mm, "end": v(-56.97, -11.92) * mm});
            skLineSegment(sketch, "E80.2.58.0", {"start": v(-56.22, -15.06) * mm, "end": v(-56.1, -15.5) * mm});
            skLineSegment(sketch, "E80.3.58.0", {"start": v(-56.22, -15.06) * mm, "end": v(-57.25, -15.35) * mm});
            skArc(sketch, "E80.6.58.0", {"start": v(-58.3, -15.13) * mm, "mid": v(-57.8, -15.36) * mm, "end": v(-57.25, -15.35) * mm});
            skArc(sketch, "E80.10.58.0", {"start": v(-57.5, -14.43) * mm, "mid": v(-57.98, -14.68) * mm, "end": v(-58.3, -15.13) * mm});
            skLineSegment(sketch, "E80.14.58.0", {"start": v(-56.45, -14.17) * mm, "end": v(-57.5, -14.43) * mm});
            skLineSegment(sketch, "E80.17.58.0", {"start": v(-56.45, -14.17) * mm, "end": v(-56.56, -13.72) * mm});
            skLineSegment(sketch, "E80.2.59.0", {"start": v(-55.71, -16.84) * mm, "end": v(-55.58, -17.28) * mm});
            skLineSegment(sketch, "E80.3.59.0", {"start": v(-55.71, -16.84) * mm, "end": v(-56.74, -17.16) * mm});
            skArc(sketch, "E80.6.59.0", {"start": v(-57.79, -16.97) * mm, "mid": v(-57.29, -17.2) * mm, "end": v(-56.74, -17.16) * mm});
            skArc(sketch, "E80.10.59.0", {"start": v(-57, -16.24) * mm, "mid": v(-57.49, -16.5) * mm, "end": v(-57.79, -16.97) * mm});
            skLineSegment(sketch, "E80.14.59.0", {"start": v(-55.97, -15.96) * mm, "end": v(-57, -16.24) * mm});
            skLineSegment(sketch, "E80.17.59.0", {"start": v(-55.97, -15.96) * mm, "end": v(-56.1, -15.5) * mm});
            skLineSegment(sketch, "E80.2.60.0", {"start": v(-55.15, -18.6) * mm, "end": v(-55, -19.04) * mm});
            skLineSegment(sketch, "E80.3.60.0", {"start": v(-55.15, -18.6) * mm, "end": v(-56.16, -18.95) * mm});
            skArc(sketch, "E80.6.60.0", {"start": v(-57.22, -18.8) * mm, "mid": v(-56.71, -19) * mm, "end": v(-56.16, -18.95) * mm});
            skArc(sketch, "E80.10.60.0", {"start": v(-56.46, -18.04) * mm, "mid": v(-56.93, -18.33) * mm, "end": v(-57.22, -18.8) * mm});
            skLineSegment(sketch, "E80.14.60.0", {"start": v(-55.44, -17.73) * mm, "end": v(-56.46, -18.04) * mm});
            skLineSegment(sketch, "E80.17.60.0", {"start": v(-55.44, -17.73) * mm, "end": v(-55.58, -17.28) * mm});
            skLineSegment(sketch, "E80.2.61.0", {"start": v(-54.53, -20.33) * mm, "end": v(-54.37, -20.77) * mm});
            skLineSegment(sketch, "E80.3.61.0", {"start": v(-54.53, -20.33) * mm, "end": v(-55.54, -20.72) * mm});
            skArc(sketch, "E80.6.61.0", {"start": v(-56.6, -20.6) * mm, "mid": v(-56.08, -20.79) * mm, "end": v(-55.54, -20.72) * mm});
            skArc(sketch, "E80.10.61.0", {"start": v(-55.86, -19.83) * mm, "mid": v(-56.32, -20.12) * mm, "end": v(-56.6, -20.6) * mm});
            skLineSegment(sketch, "E80.14.61.0", {"start": v(-54.85, -19.48) * mm, "end": v(-55.86, -19.83) * mm});
            skLineSegment(sketch, "E80.17.61.0", {"start": v(-54.85, -19.48) * mm, "end": v(-55, -19.04) * mm});
            skLineSegment(sketch, "E80.2.62.0", {"start": v(-53.86, -22.05) * mm, "end": v(-53.68, -22.49) * mm});
            skLineSegment(sketch, "E80.3.62.0", {"start": v(-53.86, -22.05) * mm, "end": v(-54.85, -22.47) * mm});
            skArc(sketch, "E80.6.62.0", {"start": v(-55.91, -22.38) * mm, "mid": v(-55.4, -22.56) * mm, "end": v(-54.85, -22.47) * mm});
            skArc(sketch, "E80.10.62.0", {"start": v(-55.2, -21.59) * mm, "mid": v(-55.66, -21.9) * mm, "end": v(-55.91, -22.38) * mm});
            skLineSegment(sketch, "E80.14.62.0", {"start": v(-54.2, -21.2) * mm, "end": v(-55.2, -21.59) * mm});
            skLineSegment(sketch, "E80.17.62.0", {"start": v(-54.2, -21.2) * mm, "end": v(-54.37, -20.77) * mm});
            skLineSegment(sketch, "E80.2.63.0", {"start": v(-53.13, -23.75) * mm, "end": v(-52.94, -24.18) * mm});
            skLineSegment(sketch, "E80.3.63.0", {"start": v(-53.13, -23.75) * mm, "end": v(-54.1, -24.2) * mm});
            skArc(sketch, "E80.6.63.0", {"start": v(-55.18, -24.15) * mm, "mid": v(-54.65, -24.3) * mm, "end": v(-54.1, -24.2) * mm});
            skArc(sketch, "E80.10.63.0", {"start": v(-54.5, -23.33) * mm, "mid": v(-54.93, -23.65) * mm, "end": v(-55.18, -24.15) * mm});
            skLineSegment(sketch, "E80.14.63.0", {"start": v(-53.5, -22.92) * mm, "end": v(-54.5, -23.33) * mm});
            skLineSegment(sketch, "E80.17.63.0", {"start": v(-53.5, -22.92) * mm, "end": v(-53.68, -22.49) * mm});
            skLineSegment(sketch, "E80.2.64.0", {"start": v(-52.35, -25.43) * mm, "end": v(-52.15, -25.84) * mm});
            skLineSegment(sketch, "E80.3.64.0", {"start": v(-52.35, -25.43) * mm, "end": v(-53.31, -25.9) * mm});
            skArc(sketch, "E80.6.64.0", {"start": v(-54.38, -25.89) * mm, "mid": v(-53.85, -26.03) * mm, "end": v(-53.31, -25.9) * mm});
            skArc(sketch, "E80.10.64.0", {"start": v(-53.72, -25.05) * mm, "mid": v(-54.16, -25.39) * mm, "end": v(-54.38, -25.89) * mm});
            skLineSegment(sketch, "E80.14.64.0", {"start": v(-52.75, -24.6) * mm, "end": v(-53.72, -25.05) * mm});
            skLineSegment(sketch, "E80.17.64.0", {"start": v(-52.75, -24.6) * mm, "end": v(-52.94, -24.18) * mm});
            skLineSegment(sketch, "E80.2.65.0", {"start": v(-51.52, -27.07) * mm, "end": v(-51.3, -27.49) * mm});
            skLineSegment(sketch, "E80.3.65.0", {"start": v(-51.52, -27.07) * mm, "end": v(-52.47, -27.58) * mm});
            skArc(sketch, "E80.6.65.0", {"start": v(-53.53, -27.6) * mm, "mid": v(-53, -27.72) * mm, "end": v(-52.47, -27.58) * mm});
            skArc(sketch, "E80.10.65.0", {"start": v(-52.9, -26.74) * mm, "mid": v(-53.32, -27.1) * mm, "end": v(-53.53, -27.6) * mm});
            skLineSegment(sketch, "E80.14.65.0", {"start": v(-51.94, -26.26) * mm, "end": v(-52.9, -26.74) * mm});
            skLineSegment(sketch, "E80.17.65.0", {"start": v(-51.94, -26.26) * mm, "end": v(-52.15, -25.84) * mm});
            skLineSegment(sketch, "E80.2.66.0", {"start": v(-50.64, -28.7) * mm, "end": v(-50.4, -29.1) * mm});
            skLineSegment(sketch, "E80.3.66.0", {"start": v(-50.64, -28.7) * mm, "end": v(-51.56, -29.23) * mm});
            skArc(sketch, "E80.6.66.0", {"start": v(-52.63, -29.28) * mm, "mid": v(-52.1, -29.39) * mm, "end": v(-51.56, -29.23) * mm});
            skArc(sketch, "E80.10.66.0", {"start": v(-52.03, -28.4) * mm, "mid": v(-52.44, -28.77) * mm, "end": v(-52.63, -29.28) * mm});
            skLineSegment(sketch, "E80.14.66.0", {"start": v(-51.08, -27.9) * mm, "end": v(-52.03, -28.4) * mm});
            skLineSegment(sketch, "E80.17.66.0", {"start": v(-51.08, -27.9) * mm, "end": v(-51.3, -27.49) * mm});
            skLineSegment(sketch, "E80.2.67.0", {"start": v(-49.7, -30.29) * mm, "end": v(-49.45, -30.68) * mm});
            skLineSegment(sketch, "E80.3.67.0", {"start": v(-49.7, -30.29) * mm, "end": v(-50.61, -30.85) * mm});
            skArc(sketch, "E80.6.67.0", {"start": v(-51.67, -30.94) * mm, "mid": v(-51.13, -31.03) * mm, "end": v(-50.61, -30.85) * mm});
            skArc(sketch, "E80.10.67.0", {"start": v(-51.1, -30.04) * mm, "mid": v(-51.5, -30.42) * mm, "end": v(-51.67, -30.94) * mm});
            skLineSegment(sketch, "E80.14.67.0", {"start": v(-50.17, -29.5) * mm, "end": v(-51.1, -30.04) * mm});
            skLineSegment(sketch, "E80.17.67.0", {"start": v(-50.17, -29.5) * mm, "end": v(-50.4, -29.1) * mm});
            skLineSegment(sketch, "E80.2.68.0", {"start": v(-48.71, -31.85) * mm, "end": v(-48.46, -32.24) * mm});
            skLineSegment(sketch, "E80.3.68.0", {"start": v(-48.71, -31.85) * mm, "end": v(-49.6, -32.45) * mm});
            skArc(sketch, "E80.6.68.0", {"start": v(-50.67, -32.56) * mm, "mid": v(-50.12, -32.63) * mm, "end": v(-49.6, -32.45) * mm});
            skArc(sketch, "E80.10.68.0", {"start": v(-50.12, -31.64) * mm, "mid": v(-50.5, -32.04) * mm, "end": v(-50.67, -32.56) * mm});
            skLineSegment(sketch, "E80.14.68.0", {"start": v(-49.2, -31.08) * mm, "end": v(-50.12, -31.64) * mm});
            skLineSegment(sketch, "E80.17.68.0", {"start": v(-49.2, -31.08) * mm, "end": v(-49.45, -30.68) * mm});
            skLineSegment(sketch, "E80.2.69.0", {"start": v(-47.68, -33.38) * mm, "end": v(-47.4, -33.76) * mm});
            skLineSegment(sketch, "E80.3.69.0", {"start": v(-47.68, -33.38) * mm, "end": v(-48.55, -34) * mm});
            skArc(sketch, "E80.6.69.0", {"start": v(-49.6, -34.15) * mm, "mid": v(-49.06, -34.2) * mm, "end": v(-48.55, -34) * mm});
            skArc(sketch, "E80.10.69.0", {"start": v(-49.1, -33.22) * mm, "mid": v(-49.46, -33.62) * mm, "end": v(-49.6, -34.15) * mm});
            skLineSegment(sketch, "E80.14.69.0", {"start": v(-48.2, -32.63) * mm, "end": v(-49.1, -33.22) * mm});
            skLineSegment(sketch, "E80.17.69.0", {"start": v(-48.2, -32.63) * mm, "end": v(-48.46, -32.24) * mm});
            skLineSegment(sketch, "E80.2.70.0", {"start": v(-46.6, -34.88) * mm, "end": v(-46.31, -35.25) * mm});
            skLineSegment(sketch, "E80.3.70.0", {"start": v(-46.6, -34.88) * mm, "end": v(-47.45, -35.53) * mm});
            skArc(sketch, "E80.6.70.0", {"start": v(-48.5, -35.7) * mm, "mid": v(-47.95, -35.75) * mm, "end": v(-47.45, -35.53) * mm});
            skArc(sketch, "E80.10.70.0", {"start": v(-48.01, -34.76) * mm, "mid": v(-48.37, -35.18) * mm, "end": v(-48.5, -35.7) * mm});
            skLineSegment(sketch, "E80.14.70.0", {"start": v(-47.14, -34.14) * mm, "end": v(-48.01, -34.76) * mm});
            skLineSegment(sketch, "E80.17.70.0", {"start": v(-47.14, -34.14) * mm, "end": v(-47.4, -33.76) * mm});
            skLineSegment(sketch, "E80.2.71.0", {"start": v(-45.47, -36.34) * mm, "end": v(-45.17, -36.7) * mm});
            skLineSegment(sketch, "E80.3.71.0", {"start": v(-45.47, -36.34) * mm, "end": v(-46.3, -37.01) * mm});
            skArc(sketch, "E80.6.71.0", {"start": v(-47.34, -37.23) * mm, "mid": v(-46.8, -37.25) * mm, "end": v(-46.3, -37.01) * mm});
            skArc(sketch, "E80.10.71.0", {"start": v(-46.89, -36.27) * mm, "mid": v(-47.23, -36.7) * mm, "end": v(-47.34, -37.23) * mm});
            skLineSegment(sketch, "E80.14.71.0", {"start": v(-46.03, -35.62) * mm, "end": v(-46.89, -36.27) * mm});
            skLineSegment(sketch, "E80.17.71.0", {"start": v(-46.03, -35.62) * mm, "end": v(-46.31, -35.25) * mm});
            skLineSegment(sketch, "E80.2.72.0", {"start": v(-44.3, -37.76) * mm, "end": v(-43.98, -38.11) * mm});
            skLineSegment(sketch, "E80.3.72.0", {"start": v(-44.3, -37.76) * mm, "end": v(-45.1, -38.46) * mm});
            skArc(sketch, "E80.6.72.0", {"start": v(-46.14, -38.71) * mm, "mid": v(-45.59, -38.72) * mm, "end": v(-45.1, -38.46) * mm});
            skArc(sketch, "E80.10.72.0", {"start": v(-45.71, -37.74) * mm, "mid": v(-46.04, -38.17) * mm, "end": v(-46.14, -38.71) * mm});
            skLineSegment(sketch, "E80.14.72.0", {"start": v(-44.88, -37.06) * mm, "end": v(-45.71, -37.74) * mm});
            skLineSegment(sketch, "E80.17.72.0", {"start": v(-44.88, -37.06) * mm, "end": v(-45.17, -36.7) * mm});
            skLineSegment(sketch, "E80.2.73.0", {"start": v(-43.07, -39.15) * mm, "end": v(-42.75, -39.49) * mm});
            skLineSegment(sketch, "E80.3.73.0", {"start": v(-43.07, -39.15) * mm, "end": v(-43.86, -39.88) * mm});
            skArc(sketch, "E80.6.73.0", {"start": v(-44.89, -40.16) * mm, "mid": v(-44.34, -40.14) * mm, "end": v(-43.86, -39.88) * mm});
            skArc(sketch, "E80.10.73.0", {"start": v(-44.5, -39.17) * mm, "mid": v(-44.8, -39.61) * mm, "end": v(-44.89, -40.16) * mm});
            skLineSegment(sketch, "E80.14.73.0", {"start": v(-43.68, -38.47) * mm, "end": v(-44.5, -39.17) * mm});
            skLineSegment(sketch, "E80.17.73.0", {"start": v(-43.68, -38.47) * mm, "end": v(-43.98, -38.11) * mm});
            skLineSegment(sketch, "E80.2.74.0", {"start": v(-41.8, -40.5) * mm, "end": v(-41.48, -40.83) * mm});
            skLineSegment(sketch, "E80.3.74.0", {"start": v(-41.8, -40.5) * mm, "end": v(-42.57, -41.25) * mm});
            skArc(sketch, "E80.6.74.0", {"start": v(-43.59, -41.56) * mm, "mid": v(-43.04, -41.53) * mm, "end": v(-42.57, -41.25) * mm});
            skArc(sketch, "E80.10.74.0", {"start": v(-43.23, -40.56) * mm, "mid": v(-43.53, -41.02) * mm, "end": v(-43.59, -41.56) * mm});
            skLineSegment(sketch, "E80.14.74.0", {"start": v(-42.44, -39.83) * mm, "end": v(-43.23, -40.56) * mm});
            skLineSegment(sketch, "E80.17.74.0", {"start": v(-42.44, -39.83) * mm, "end": v(-42.75, -39.49) * mm});
            skLineSegment(sketch, "E80.2.75.0", {"start": v(-40.5, -41.8) * mm, "end": v(-40.16, -42.12) * mm});
            skLineSegment(sketch, "E80.3.75.0", {"start": v(-40.5, -41.8) * mm, "end": v(-41.24, -42.58) * mm});
            skArc(sketch, "E80.6.75.0", {"start": v(-42.25, -42.92) * mm, "mid": v(-41.7, -42.87) * mm, "end": v(-41.24, -42.58) * mm});
            skArc(sketch, "E80.10.75.0", {"start": v(-41.92, -41.9) * mm, "mid": v(-42.2, -42.38) * mm, "end": v(-42.25, -42.92) * mm});
            skLineSegment(sketch, "E80.14.75.0", {"start": v(-41.15, -41.16) * mm, "end": v(-41.92, -41.9) * mm});
            skLineSegment(sketch, "E80.17.75.0", {"start": v(-41.15, -41.16) * mm, "end": v(-41.48, -40.83) * mm});
            skLineSegment(sketch, "E80.2.76.0", {"start": v(-39.15, -43.06) * mm, "end": v(-38.8, -43.37) * mm});
            skLineSegment(sketch, "E80.3.76.0", {"start": v(-39.15, -43.06) * mm, "end": v(-39.87, -43.86) * mm});
            skArc(sketch, "E80.6.76.0", {"start": v(-40.87, -44.24) * mm, "mid": v(-40.32, -44.18) * mm, "end": v(-39.87, -43.86) * mm});
            skArc(sketch, "E80.10.76.0", {"start": v(-40.57, -43.22) * mm, "mid": v(-40.84, -43.7) * mm, "end": v(-40.87, -44.24) * mm});
            skLineSegment(sketch, "E80.14.76.0", {"start": v(-39.82, -42.44) * mm, "end": v(-40.57, -43.22) * mm});
            skLineSegment(sketch, "E80.17.76.0", {"start": v(-39.82, -42.44) * mm, "end": v(-40.16, -42.12) * mm});
            skLineSegment(sketch, "E80.2.77.0", {"start": v(-37.77, -44.28) * mm, "end": v(-37.41, -44.58) * mm});
            skLineSegment(sketch, "E80.3.77.0", {"start": v(-37.77, -44.28) * mm, "end": v(-38.46, -45.1) * mm});
            skArc(sketch, "E80.6.77.0", {"start": v(-39.44, -45.52) * mm, "mid": v(-38.9, -45.43) * mm, "end": v(-38.46, -45.1) * mm});
            skArc(sketch, "E80.10.77.0", {"start": v(-39.17, -44.48) * mm, "mid": v(-39.43, -44.97) * mm, "end": v(-39.44, -45.52) * mm});
            skLineSegment(sketch, "E80.14.77.0", {"start": v(-38.46, -43.69) * mm, "end": v(-39.17, -44.48) * mm});
            skLineSegment(sketch, "E80.17.77.0", {"start": v(-38.46, -43.69) * mm, "end": v(-38.8, -43.37) * mm});
            skLineSegment(sketch, "E80.2.78.0", {"start": v(-36.34, -45.46) * mm, "end": v(-35.98, -45.75) * mm});
            skLineSegment(sketch, "E80.3.78.0", {"start": v(-36.34, -45.46) * mm, "end": v(-37, -46.3) * mm});
            skArc(sketch, "E80.6.78.0", {"start": v(-37.98, -46.75) * mm, "mid": v(-37.44, -46.64) * mm, "end": v(-37, -46.3) * mm});
            skArc(sketch, "E80.10.78.0", {"start": v(-37.74, -45.7) * mm, "mid": v(-37.99, -46.2) * mm, "end": v(-37.98, -46.75) * mm});
            skLineSegment(sketch, "E80.14.78.0", {"start": v(-37.05, -44.88) * mm, "end": v(-37.74, -45.7) * mm});
            skLineSegment(sketch, "E80.17.78.0", {"start": v(-37.05, -44.88) * mm, "end": v(-37.41, -44.58) * mm});
            skLineSegment(sketch, "E80.2.79.0", {"start": v(-34.88, -46.6) * mm, "end": v(-34.5, -46.87) * mm});
            skLineSegment(sketch, "E80.3.79.0", {"start": v(-34.88, -46.6) * mm, "end": v(-35.52, -47.45) * mm});
            skArc(sketch, "E80.6.79.0", {"start": v(-36.47, -47.93) * mm, "mid": v(-35.94, -47.8) * mm, "end": v(-35.52, -47.45) * mm});
            skArc(sketch, "E80.10.79.0", {"start": v(-36.27, -46.88) * mm, "mid": v(-36.5, -47.38) * mm, "end": v(-36.47, -47.93) * mm});
            skLineSegment(sketch, "E80.14.79.0", {"start": v(-35.61, -46.04) * mm, "end": v(-36.27, -46.88) * mm});
            skLineSegment(sketch, "E80.17.79.0", {"start": v(-35.61, -46.04) * mm, "end": v(-35.98, -45.75) * mm});
            skLineSegment(sketch, "E80.2.80.0", {"start": v(-33.39, -47.67) * mm, "end": v(-33, -47.94) * mm});
            skLineSegment(sketch, "E80.3.80.0", {"start": v(-33.39, -47.67) * mm, "end": v(-34, -48.56) * mm});
            skArc(sketch, "E80.6.80.0", {"start": v(-34.94, -49.06) * mm, "mid": v(-34.4, -48.92) * mm, "end": v(-34, -48.56) * mm});
            skArc(sketch, "E80.10.80.0", {"start": v(-34.77, -48) * mm, "mid": v(-34.98, -48.51) * mm, "end": v(-34.94, -49.06) * mm});
            skLineSegment(sketch, "E80.14.80.0", {"start": v(-34.13, -47.14) * mm, "end": v(-34.77, -48) * mm});
            skLineSegment(sketch, "E80.17.80.0", {"start": v(-34.13, -47.14) * mm, "end": v(-34.5, -46.87) * mm});
            skLineSegment(sketch, "E80.2.81.0", {"start": v(-31.86, -48.7) * mm, "end": v(-31.47, -48.96) * mm});
            skLineSegment(sketch, "E80.3.81.0", {"start": v(-31.86, -48.7) * mm, "end": v(-32.44, -49.61) * mm});
            skArc(sketch, "E80.6.81.0", {"start": v(-33.36, -50.14) * mm, "mid": v(-32.83, -50) * mm, "end": v(-32.44, -49.61) * mm});
            skArc(sketch, "E80.10.81.0", {"start": v(-33.23, -49.08) * mm, "mid": v(-33.42, -49.6) * mm, "end": v(-33.36, -50.14) * mm});
            skLineSegment(sketch, "E80.14.81.0", {"start": v(-32.62, -48.2) * mm, "end": v(-33.23, -49.08) * mm});
            skLineSegment(sketch, "E80.17.81.0", {"start": v(-32.62, -48.2) * mm, "end": v(-33, -47.94) * mm});
            skLineSegment(sketch, "E80.2.82.0", {"start": v(-30.3, -49.7) * mm, "end": v(-29.9, -49.93) * mm});
            skLineSegment(sketch, "E80.3.82.0", {"start": v(-30.3, -49.7) * mm, "end": v(-30.85, -50.62) * mm});
            skArc(sketch, "E80.6.82.0", {"start": v(-31.75, -51.18) * mm, "mid": v(-31.23, -51) * mm, "end": v(-30.85, -50.62) * mm});
            skArc(sketch, "E80.10.82.0", {"start": v(-31.65, -50.11) * mm, "mid": v(-31.83, -50.63) * mm, "end": v(-31.75, -51.18) * mm});
            skLineSegment(sketch, "E80.14.82.0", {"start": v(-31.07, -49.21) * mm, "end": v(-31.65, -50.11) * mm});
            skLineSegment(sketch, "E80.17.82.0", {"start": v(-31.07, -49.21) * mm, "end": v(-31.47, -48.96) * mm});
            skLineSegment(sketch, "E80.2.83.0", {"start": v(-28.7, -50.63) * mm, "end": v(-28.3, -50.86) * mm});
            skLineSegment(sketch, "E80.3.83.0", {"start": v(-28.7, -50.63) * mm, "end": v(-29.22, -51.57) * mm});
            skArc(sketch, "E80.6.83.0", {"start": v(-30.11, -52.16) * mm, "mid": v(-29.6, -51.97) * mm, "end": v(-29.22, -51.57) * mm});
            skArc(sketch, "E80.10.83.0", {"start": v(-30.05, -51.1) * mm, "mid": v(-30.21, -51.62) * mm, "end": v(-30.11, -52.16) * mm});
            skLineSegment(sketch, "E80.14.83.0", {"start": v(-29.5, -50.17) * mm, "end": v(-30.05, -51.1) * mm});
            skLineSegment(sketch, "E80.17.83.0", {"start": v(-29.5, -50.17) * mm, "end": v(-29.9, -49.93) * mm});
            skLineSegment(sketch, "E80.2.84.0", {"start": v(-27.08, -51.52) * mm, "end": v(-26.67, -51.73) * mm});
            skLineSegment(sketch, "E80.3.84.0", {"start": v(-27.08, -51.52) * mm, "end": v(-27.57, -52.47) * mm});
            skArc(sketch, "E80.6.84.0", {"start": v(-28.44, -53.09) * mm, "mid": v(-27.93, -52.89) * mm, "end": v(-27.57, -52.47) * mm});
            skArc(sketch, "E80.10.84.0", {"start": v(-28.41, -52.02) * mm, "mid": v(-28.56, -52.55) * mm, "end": v(-28.44, -53.09) * mm});
            skLineSegment(sketch, "E80.14.84.0", {"start": v(-27.89, -51.08) * mm, "end": v(-28.41, -52.02) * mm});
            skLineSegment(sketch, "E80.17.84.0", {"start": v(-27.89, -51.08) * mm, "end": v(-28.3, -50.86) * mm});
            skLineSegment(sketch, "E80.2.85.0", {"start": v(-25.44, -52.35) * mm, "end": v(-25.01, -52.55) * mm});
            skLineSegment(sketch, "E80.3.85.0", {"start": v(-25.44, -52.35) * mm, "end": v(-25.9, -53.32) * mm});
            skArc(sketch, "E80.6.85.0", {"start": v(-26.75, -53.96) * mm, "mid": v(-26.24, -53.75) * mm, "end": v(-25.9, -53.32) * mm});
            skArc(sketch, "E80.10.85.0", {"start": v(-26.75, -52.9) * mm, "mid": v(-26.88, -53.43) * mm, "end": v(-26.75, -53.96) * mm});
            skLineSegment(sketch, "E80.14.85.0", {"start": v(-26.25, -51.94) * mm, "end": v(-26.75, -52.9) * mm});
            skLineSegment(sketch, "E80.17.85.0", {"start": v(-26.25, -51.94) * mm, "end": v(-26.67, -51.73) * mm});
            skLineSegment(sketch, "E80.2.86.0", {"start": v(-23.76, -53.13) * mm, "end": v(-23.33, -53.32) * mm});
            skLineSegment(sketch, "E80.3.86.0", {"start": v(-23.76, -53.13) * mm, "end": v(-24.19, -54.11) * mm});
            skArc(sketch, "E80.6.86.0", {"start": v(-25.02, -54.79) * mm, "mid": v(-24.52, -54.55) * mm, "end": v(-24.19, -54.11) * mm});
            skArc(sketch, "E80.10.86.0", {"start": v(-25.06, -53.72) * mm, "mid": v(-25.17, -54.26) * mm, "end": v(-25.02, -54.79) * mm});
            skLineSegment(sketch, "E80.14.86.0", {"start": v(-24.6, -52.75) * mm, "end": v(-25.06, -53.72) * mm});
            skLineSegment(sketch, "E80.17.86.0", {"start": v(-24.6, -52.75) * mm, "end": v(-25.01, -52.55) * mm});
            skLineSegment(sketch, "E80.2.87.0", {"start": v(-22.06, -53.86) * mm, "end": v(-21.63, -54.03) * mm});
            skLineSegment(sketch, "E80.3.87.0", {"start": v(-22.06, -53.86) * mm, "end": v(-22.46, -54.85) * mm});
            skArc(sketch, "E80.6.87.0", {"start": v(-23.27, -55.55) * mm, "mid": v(-22.78, -55.3) * mm, "end": v(-22.46, -54.85) * mm});
            skArc(sketch, "E80.10.87.0", {"start": v(-23.34, -54.49) * mm, "mid": v(-23.43, -55.03) * mm, "end": v(-23.27, -55.55) * mm});
            skLineSegment(sketch, "E80.14.87.0", {"start": v(-22.9, -53.5) * mm, "end": v(-23.34, -54.49) * mm});
            skLineSegment(sketch, "E80.17.87.0", {"start": v(-22.9, -53.5) * mm, "end": v(-23.33, -53.32) * mm});
            skLineSegment(sketch, "E80.2.88.0", {"start": v(-20.34, -54.53) * mm, "end": v(-19.9, -54.7) * mm});
            skLineSegment(sketch, "E80.3.88.0", {"start": v(-20.34, -54.53) * mm, "end": v(-20.7, -55.54) * mm});
            skArc(sketch, "E80.6.88.0", {"start": v(-21.5, -56.26) * mm, "mid": v(-21.01, -56) * mm, "end": v(-20.7, -55.54) * mm});
            skArc(sketch, "E80.10.88.0", {"start": v(-21.6, -55.2) * mm, "mid": v(-21.68, -55.74) * mm, "end": v(-21.5, -56.26) * mm});
            skLineSegment(sketch, "E80.14.88.0", {"start": v(-21.2, -54.2) * mm, "end": v(-21.6, -55.2) * mm});
            skLineSegment(sketch, "E80.17.88.0", {"start": v(-21.2, -54.2) * mm, "end": v(-21.63, -54.03) * mm});
            skLineSegment(sketch, "E80.2.89.0", {"start": v(-18.6, -55.15) * mm, "end": v(-18.16, -55.3) * mm});
            skLineSegment(sketch, "E80.3.89.0", {"start": v(-18.6, -55.15) * mm, "end": v(-18.94, -56.17) * mm});
            skArc(sketch, "E80.6.89.0", {"start": v(-19.7, -56.92) * mm, "mid": v(-19.23, -56.63) * mm, "end": v(-18.94, -56.17) * mm});
            skArc(sketch, "E80.10.89.0", {"start": v(-19.84, -55.86) * mm, "mid": v(-19.9, -56.4) * mm, "end": v(-19.7, -56.92) * mm});
            skLineSegment(sketch, "E80.14.89.0", {"start": v(-19.47, -54.85) * mm, "end": v(-19.84, -55.86) * mm});
            skLineSegment(sketch, "E80.17.89.0", {"start": v(-19.47, -54.85) * mm, "end": v(-19.9, -54.7) * mm});
            skLineSegment(sketch, "E80.2.90.0", {"start": v(-16.84, -55.71) * mm, "end": v(-16.4, -55.84) * mm});
            skLineSegment(sketch, "E80.3.90.0", {"start": v(-16.84, -55.71) * mm, "end": v(-17.14, -56.74) * mm});
            skArc(sketch, "E80.6.90.0", {"start": v(-17.88, -57.51) * mm, "mid": v(-17.42, -57.22) * mm, "end": v(-17.14, -56.74) * mm});
            skArc(sketch, "E80.10.90.0", {"start": v(-18.05, -56.46) * mm, "mid": v(-18.1, -57) * mm, "end": v(-17.88, -57.51) * mm});
            skLineSegment(sketch, "E80.14.90.0", {"start": v(-17.72, -55.44) * mm, "end": v(-18.05, -56.46) * mm});
            skLineSegment(sketch, "E80.17.90.0", {"start": v(-17.72, -55.44) * mm, "end": v(-18.16, -55.3) * mm});
            skLineSegment(sketch, "E80.2.91.0", {"start": v(-15.07, -56.22) * mm, "end": v(-14.62, -56.33) * mm});
            skLineSegment(sketch, "E80.3.91.0", {"start": v(-15.07, -56.22) * mm, "end": v(-15.34, -57.26) * mm});
            skArc(sketch, "E80.6.91.0", {"start": v(-16.05, -58.05) * mm, "mid": v(-15.6, -57.74) * mm, "end": v(-15.34, -57.26) * mm});
            skArc(sketch, "E80.10.91.0", {"start": v(-16.25, -57) * mm, "mid": v(-16.28, -57.55) * mm, "end": v(-16.05, -58.05) * mm});
            skLineSegment(sketch, "E80.14.91.0", {"start": v(-15.95, -55.97) * mm, "end": v(-16.25, -57) * mm});
            skLineSegment(sketch, "E80.17.91.0", {"start": v(-15.95, -55.97) * mm, "end": v(-16.4, -55.84) * mm});
            skLineSegment(sketch, "E80.2.92.0", {"start": v(-13.28, -56.67) * mm, "end": v(-12.82, -56.77) * mm});
            skLineSegment(sketch, "E80.3.92.0", {"start": v(-13.28, -56.67) * mm, "end": v(-13.51, -57.71) * mm});
            skArc(sketch, "E80.6.92.0", {"start": v(-14.2, -58.53) * mm, "mid": v(-13.76, -58.2) * mm, "end": v(-13.51, -57.71) * mm});
            skArc(sketch, "E80.10.92.0", {"start": v(-14.44, -57.49) * mm, "mid": v(-14.44, -58.04) * mm, "end": v(-14.2, -58.53) * mm});
            skLineSegment(sketch, "E80.14.92.0", {"start": v(-14.17, -56.45) * mm, "end": v(-14.44, -57.49) * mm});
            skLineSegment(sketch, "E80.17.92.0", {"start": v(-14.17, -56.45) * mm, "end": v(-14.62, -56.33) * mm});
            skLineSegment(sketch, "E80.2.93.0", {"start": v(-11.47, -57.06) * mm, "end": v(-11.01, -57.15) * mm});
            skLineSegment(sketch, "E80.3.93.0", {"start": v(-11.47, -57.06) * mm, "end": v(-11.67, -58.11) * mm});
            skArc(sketch, "E80.6.93.0", {"start": v(-12.34, -58.95) * mm, "mid": v(-11.9, -58.61) * mm, "end": v(-11.67, -58.11) * mm});
            skArc(sketch, "E80.10.93.0", {"start": v(-12.6, -57.92) * mm, "mid": v(-12.6, -58.47) * mm, "end": v(-12.34, -58.95) * mm});
            skLineSegment(sketch, "E80.14.93.0", {"start": v(-12.37, -56.87) * mm, "end": v(-12.6, -57.92) * mm});
            skLineSegment(sketch, "E80.17.93.0", {"start": v(-12.37, -56.87) * mm, "end": v(-12.82, -56.77) * mm});
            skLineSegment(sketch, "E80.2.94.0", {"start": v(-9.66, -57.4) * mm, "end": v(-9.2, -57.47) * mm});
            skLineSegment(sketch, "E80.3.94.0", {"start": v(-9.66, -57.4) * mm, "end": v(-9.82, -58.45) * mm});
            skArc(sketch, "E80.6.94.0", {"start": v(-10.46, -59.31) * mm, "mid": v(-10.04, -58.96) * mm, "end": v(-9.82, -58.45) * mm});
            skArc(sketch, "E80.10.94.0", {"start": v(-10.76, -58.29) * mm, "mid": v(-10.73, -58.84) * mm, "end": v(-10.46, -59.31) * mm});
            skLineSegment(sketch, "E80.14.94.0", {"start": v(-10.56, -57.24) * mm, "end": v(-10.76, -58.29) * mm});
            skLineSegment(sketch, "E80.17.94.0", {"start": v(-10.56, -57.24) * mm, "end": v(-11.01, -57.15) * mm});
            skLineSegment(sketch, "E80.2.95.0", {"start": v(-7.83, -57.67) * mm, "end": v(-7.37, -57.73) * mm});
            skLineSegment(sketch, "E80.3.95.0", {"start": v(-7.83, -57.67) * mm, "end": v(-7.96, -58.74) * mm});
            skArc(sketch, "E80.6.95.0", {"start": v(-8.57, -59.62) * mm, "mid": v(-8.16, -59.25) * mm, "end": v(-7.96, -58.74) * mm});
            skArc(sketch, "E80.10.95.0", {"start": v(-8.9, -58.6) * mm, "mid": v(-8.86, -59.15) * mm, "end": v(-8.57, -59.62) * mm});
            skLineSegment(sketch, "E80.14.95.0", {"start": v(-8.74, -57.54) * mm, "end": v(-8.9, -58.6) * mm});
            skLineSegment(sketch, "E80.17.95.0", {"start": v(-8.74, -57.54) * mm, "end": v(-9.2, -57.47) * mm});
            skLineSegment(sketch, "E80.2.96.0", {"start": v(-6, -57.9) * mm, "end": v(-5.53, -57.94) * mm});
            skLineSegment(sketch, "E80.3.96.0", {"start": v(-6, -57.9) * mm, "end": v(-6.1, -58.96) * mm});
            skArc(sketch, "E80.6.96.0", {"start": v(-6.68, -59.86) * mm, "mid": v(-6.28, -59.48) * mm, "end": v(-6.1, -58.96) * mm});
            skArc(sketch, "E80.10.96.0", {"start": v(-7.04, -58.85) * mm, "mid": v(-6.98, -59.4) * mm, "end": v(-6.68, -59.86) * mm});
            skLineSegment(sketch, "E80.14.96.0", {"start": v(-6.9, -57.8) * mm, "end": v(-7.04, -58.85) * mm});
            skLineSegment(sketch, "E80.17.96.0", {"start": v(-6.9, -57.8) * mm, "end": v(-7.37, -57.73) * mm});
            skLineSegment(sketch, "E80.2.97.0", {"start": v(-4.16, -58.05) * mm, "end": v(-3.7, -58.08) * mm});
            skLineSegment(sketch, "E80.3.97.0", {"start": v(-4.16, -58.05) * mm, "end": v(-4.22, -59.12) * mm});
            skArc(sketch, "E80.6.97.0", {"start": v(-4.77, -60.04) * mm, "mid": v(-4.39, -59.65) * mm, "end": v(-4.22, -59.12) * mm});
            skArc(sketch, "E80.10.97.0", {"start": v(-5.17, -59.05) * mm, "mid": v(-5.1, -59.6) * mm, "end": v(-4.77, -60.04) * mm});
            skLineSegment(sketch, "E80.14.97.0", {"start": v(-5.07, -57.98) * mm, "end": v(-5.17, -59.05) * mm});
            skLineSegment(sketch, "E80.17.97.0", {"start": v(-5.07, -57.98) * mm, "end": v(-5.53, -57.94) * mm});
            skLineSegment(sketch, "E80.2.98.0", {"start": v(-2.31, -58.16) * mm, "end": v(-1.85, -58.17) * mm});
            skLineSegment(sketch, "E80.3.98.0", {"start": v(-2.31, -58.16) * mm, "end": v(-2.35, -59.23) * mm});
            skArc(sketch, "E80.6.98.0", {"start": v(-2.87, -60.16) * mm, "mid": v(-2.5, -59.76) * mm, "end": v(-2.35, -59.23) * mm});
            skArc(sketch, "E80.10.98.0", {"start": v(-3.3, -59.18) * mm, "mid": v(-3.2, -59.72) * mm, "end": v(-2.87, -60.16) * mm});
            skLineSegment(sketch, "E80.14.98.0", {"start": v(-3.23, -58.11) * mm, "end": v(-3.3, -59.18) * mm});
            skLineSegment(sketch, "E80.17.98.0", {"start": v(-3.23, -58.11) * mm, "end": v(-3.7, -58.08) * mm});
            skLineSegment(sketch, "E80.2.99.0", {"start": v(-0.47, -58.2) * mm, "end": v(0, -58.2) * mm});
            skLineSegment(sketch, "E80.3.99.0", {"start": v(-0.47, -58.2) * mm, "end": v(-0.46, -59.27) * mm});
            skArc(sketch, "E80.6.99.0", {"start": v(-0.96, -60.22) * mm, "mid": v(-0.6, -59.8) * mm, "end": v(-0.46, -59.27) * mm});
            skArc(sketch, "E80.10.99.0", {"start": v(-1.42, -59.26) * mm, "mid": v(-1.3, -59.8) * mm, "end": v(-0.96, -60.22) * mm});
            skLineSegment(sketch, "E80.14.99.0", {"start": v(-1.38, -58.19) * mm, "end": v(-1.42, -59.26) * mm});
            skLineSegment(sketch, "E80.17.99.0", {"start": v(-1.38, -58.19) * mm, "end": v(-1.85, -58.17) * mm});
            skLineSegment(sketch, "E80.2.100.0", {"start": v(1.38, -58.19) * mm, "end": v(1.85, -58.17) * mm});
            skLineSegment(sketch, "E80.3.100.0", {"start": v(1.38, -58.19) * mm, "end": v(1.42, -59.26) * mm});
            skArc(sketch, "E80.6.100.0", {"start": v(0.96, -60.22) * mm, "mid": v(1.3, -59.8) * mm, "end": v(1.42, -59.26) * mm});
            skArc(sketch, "E80.10.100.0", {"start": v(0.46, -59.27) * mm, "mid": v(0.6, -59.8) * mm, "end": v(0.96, -60.22) * mm});
            skLineSegment(sketch, "E80.14.100.0", {"start": v(0.47, -58.2) * mm, "end": v(0.46, -59.27) * mm});
            skLineSegment(sketch, "E80.17.100.0", {"start": v(0.47, -58.2) * mm, "end": v(0, -58.2) * mm});
            skLineSegment(sketch, "E80.2.101.0", {"start": v(3.23, -58.11) * mm, "end": v(3.7, -58.08) * mm});
            skLineSegment(sketch, "E80.3.101.0", {"start": v(3.23, -58.11) * mm, "end": v(3.3, -59.18) * mm});
            skArc(sketch, "E80.6.101.0", {"start": v(2.87, -60.16) * mm, "mid": v(3.2, -59.72) * mm, "end": v(3.3, -59.18) * mm});
            skArc(sketch, "E80.10.101.0", {"start": v(2.35, -59.23) * mm, "mid": v(2.5, -59.76) * mm, "end": v(2.87, -60.16) * mm});
            skLineSegment(sketch, "E80.14.101.0", {"start": v(2.31, -58.16) * mm, "end": v(2.35, -59.23) * mm});
            skLineSegment(sketch, "E80.17.101.0", {"start": v(2.31, -58.16) * mm, "end": v(1.85, -58.17) * mm});
            skLineSegment(sketch, "E80.2.102.0", {"start": v(5.07, -57.98) * mm, "end": v(5.53, -57.94) * mm});
            skLineSegment(sketch, "E80.3.102.0", {"start": v(5.07, -57.98) * mm, "end": v(5.17, -59.05) * mm});
            skArc(sketch, "E80.6.102.0", {"start": v(4.77, -60.04) * mm, "mid": v(5.1, -59.6) * mm, "end": v(5.17, -59.05) * mm});
            skArc(sketch, "E80.10.102.0", {"start": v(4.22, -59.12) * mm, "mid": v(4.39, -59.65) * mm, "end": v(4.77, -60.04) * mm});
            skLineSegment(sketch, "E80.14.102.0", {"start": v(4.16, -58.05) * mm, "end": v(4.22, -59.12) * mm});
            skLineSegment(sketch, "E80.17.102.0", {"start": v(4.16, -58.05) * mm, "end": v(3.7, -58.08) * mm});
            skLineSegment(sketch, "E80.2.103.0", {"start": v(6.9, -57.8) * mm, "end": v(7.37, -57.73) * mm});
            skLineSegment(sketch, "E80.3.103.0", {"start": v(6.9, -57.8) * mm, "end": v(7.04, -58.85) * mm});
            skArc(sketch, "E80.6.103.0", {"start": v(6.68, -59.86) * mm, "mid": v(6.98, -59.4) * mm, "end": v(7.04, -58.85) * mm});
            skArc(sketch, "E80.10.103.0", {"start": v(6.1, -58.96) * mm, "mid": v(6.28, -59.48) * mm, "end": v(6.68, -59.86) * mm});
            skLineSegment(sketch, "E80.14.103.0", {"start": v(6, -57.9) * mm, "end": v(6.1, -58.96) * mm});
            skLineSegment(sketch, "E80.17.103.0", {"start": v(6, -57.9) * mm, "end": v(5.53, -57.94) * mm});
            skLineSegment(sketch, "E80.2.104.0", {"start": v(8.74, -57.54) * mm, "end": v(9.2, -57.47) * mm});
            skLineSegment(sketch, "E80.3.104.0", {"start": v(8.74, -57.54) * mm, "end": v(8.9, -58.6) * mm});
            skArc(sketch, "E80.6.104.0", {"start": v(8.57, -59.62) * mm, "mid": v(8.86, -59.15) * mm, "end": v(8.9, -58.6) * mm});
            skArc(sketch, "E80.10.104.0", {"start": v(7.96, -58.74) * mm, "mid": v(8.16, -59.25) * mm, "end": v(8.57, -59.62) * mm});
            skLineSegment(sketch, "E80.14.104.0", {"start": v(7.83, -57.67) * mm, "end": v(7.96, -58.74) * mm});
            skLineSegment(sketch, "E80.17.104.0", {"start": v(7.83, -57.67) * mm, "end": v(7.37, -57.73) * mm});
            skLineSegment(sketch, "E80.2.105.0", {"start": v(10.56, -57.24) * mm, "end": v(11.01, -57.15) * mm});
            skLineSegment(sketch, "E80.3.105.0", {"start": v(10.56, -57.24) * mm, "end": v(10.76, -58.29) * mm});
            skArc(sketch, "E80.6.105.0", {"start": v(10.46, -59.31) * mm, "mid": v(10.73, -58.84) * mm, "end": v(10.76, -58.29) * mm});
            skArc(sketch, "E80.10.105.0", {"start": v(9.82, -58.45) * mm, "mid": v(10.04, -58.96) * mm, "end": v(10.46, -59.31) * mm});
            skLineSegment(sketch, "E80.14.105.0", {"start": v(9.66, -57.4) * mm, "end": v(9.82, -58.45) * mm});
            skLineSegment(sketch, "E80.17.105.0", {"start": v(9.66, -57.4) * mm, "end": v(9.2, -57.47) * mm});
            skLineSegment(sketch, "E80.2.106.0", {"start": v(12.37, -56.87) * mm, "end": v(12.82, -56.77) * mm});
            skLineSegment(sketch, "E80.3.106.0", {"start": v(12.37, -56.87) * mm, "end": v(12.6, -57.92) * mm});
            skArc(sketch, "E80.6.106.0", {"start": v(12.34, -58.95) * mm, "mid": v(12.6, -58.47) * mm, "end": v(12.6, -57.92) * mm});
            skArc(sketch, "E80.10.106.0", {"start": v(11.67, -58.11) * mm, "mid": v(11.9, -58.61) * mm, "end": v(12.34, -58.95) * mm});
            skLineSegment(sketch, "E80.14.106.0", {"start": v(11.47, -57.06) * mm, "end": v(11.67, -58.11) * mm});
            skLineSegment(sketch, "E80.17.106.0", {"start": v(11.47, -57.06) * mm, "end": v(11.01, -57.15) * mm});
            skLineSegment(sketch, "E80.2.107.0", {"start": v(14.17, -56.45) * mm, "end": v(14.62, -56.33) * mm});
            skLineSegment(sketch, "E80.3.107.0", {"start": v(14.17, -56.45) * mm, "end": v(14.44, -57.49) * mm});
            skArc(sketch, "E80.6.107.0", {"start": v(14.2, -58.53) * mm, "mid": v(14.44, -58.04) * mm, "end": v(14.44, -57.49) * mm});
            skArc(sketch, "E80.10.107.0", {"start": v(13.51, -57.71) * mm, "mid": v(13.76, -58.2) * mm, "end": v(14.2, -58.53) * mm});
            skLineSegment(sketch, "E80.14.107.0", {"start": v(13.28, -56.67) * mm, "end": v(13.51, -57.71) * mm});
            skLineSegment(sketch, "E80.17.107.0", {"start": v(13.28, -56.67) * mm, "end": v(12.82, -56.77) * mm});
            skLineSegment(sketch, "E80.2.108.0", {"start": v(15.95, -55.97) * mm, "end": v(16.4, -55.84) * mm});
            skLineSegment(sketch, "E80.3.108.0", {"start": v(15.95, -55.97) * mm, "end": v(16.25, -57) * mm});
            skArc(sketch, "E80.6.108.0", {"start": v(16.05, -58.05) * mm, "mid": v(16.28, -57.55) * mm, "end": v(16.25, -57) * mm});
            skArc(sketch, "E80.10.108.0", {"start": v(15.34, -57.26) * mm, "mid": v(15.6, -57.74) * mm, "end": v(16.05, -58.05) * mm});
            skLineSegment(sketch, "E80.14.108.0", {"start": v(15.07, -56.22) * mm, "end": v(15.34, -57.26) * mm});
            skLineSegment(sketch, "E80.17.108.0", {"start": v(15.07, -56.22) * mm, "end": v(14.62, -56.33) * mm});
            skLineSegment(sketch, "E80.2.109.0", {"start": v(17.72, -55.44) * mm, "end": v(18.16, -55.3) * mm});
            skLineSegment(sketch, "E80.3.109.0", {"start": v(17.72, -55.44) * mm, "end": v(18.05, -56.46) * mm});
            skArc(sketch, "E80.6.109.0", {"start": v(17.88, -57.51) * mm, "mid": v(18.1, -57) * mm, "end": v(18.05, -56.46) * mm});
            skArc(sketch, "E80.10.109.0", {"start": v(17.14, -56.74) * mm, "mid": v(17.42, -57.22) * mm, "end": v(17.88, -57.51) * mm});
            skLineSegment(sketch, "E80.14.109.0", {"start": v(16.84, -55.71) * mm, "end": v(17.14, -56.74) * mm});
            skLineSegment(sketch, "E80.17.109.0", {"start": v(16.84, -55.71) * mm, "end": v(16.4, -55.84) * mm});
            skLineSegment(sketch, "E80.2.110.0", {"start": v(19.47, -54.85) * mm, "end": v(19.9, -54.7) * mm});
            skLineSegment(sketch, "E80.3.110.0", {"start": v(19.47, -54.85) * mm, "end": v(19.84, -55.86) * mm});
            skArc(sketch, "E80.6.110.0", {"start": v(19.7, -56.92) * mm, "mid": v(19.9, -56.4) * mm, "end": v(19.84, -55.86) * mm});
            skArc(sketch, "E80.10.110.0", {"start": v(18.94, -56.17) * mm, "mid": v(19.23, -56.63) * mm, "end": v(19.7, -56.92) * mm});
            skLineSegment(sketch, "E80.14.110.0", {"start": v(18.6, -55.15) * mm, "end": v(18.94, -56.17) * mm});
            skLineSegment(sketch, "E80.17.110.0", {"start": v(18.6, -55.15) * mm, "end": v(18.16, -55.3) * mm});
            skLineSegment(sketch, "E80.2.111.0", {"start": v(21.2, -54.2) * mm, "end": v(21.63, -54.03) * mm});
            skLineSegment(sketch, "E80.3.111.0", {"start": v(21.2, -54.2) * mm, "end": v(21.6, -55.2) * mm});
            skArc(sketch, "E80.6.111.0", {"start": v(21.5, -56.26) * mm, "mid": v(21.68, -55.74) * mm, "end": v(21.6, -55.2) * mm});
            skArc(sketch, "E80.10.111.0", {"start": v(20.7, -55.54) * mm, "mid": v(21.01, -56) * mm, "end": v(21.5, -56.26) * mm});
            skLineSegment(sketch, "E80.14.111.0", {"start": v(20.34, -54.53) * mm, "end": v(20.7, -55.54) * mm});
            skLineSegment(sketch, "E80.17.111.0", {"start": v(20.34, -54.53) * mm, "end": v(19.9, -54.7) * mm});
            skLineSegment(sketch, "E80.2.112.0", {"start": v(22.9, -53.5) * mm, "end": v(23.33, -53.32) * mm});
            skLineSegment(sketch, "E80.3.112.0", {"start": v(22.9, -53.5) * mm, "end": v(23.34, -54.49) * mm});
            skArc(sketch, "E80.6.112.0", {"start": v(23.27, -55.55) * mm, "mid": v(23.43, -55.03) * mm, "end": v(23.34, -54.49) * mm});
            skArc(sketch, "E80.10.112.0", {"start": v(22.46, -54.85) * mm, "mid": v(22.78, -55.3) * mm, "end": v(23.27, -55.55) * mm});
            skLineSegment(sketch, "E80.14.112.0", {"start": v(22.06, -53.86) * mm, "end": v(22.46, -54.85) * mm});
            skLineSegment(sketch, "E80.17.112.0", {"start": v(22.06, -53.86) * mm, "end": v(21.63, -54.03) * mm});
            skLineSegment(sketch, "E80.2.113.0", {"start": v(24.6, -52.75) * mm, "end": v(25.01, -52.55) * mm});
            skLineSegment(sketch, "E80.3.113.0", {"start": v(24.6, -52.75) * mm, "end": v(25.06, -53.72) * mm});
            skArc(sketch, "E80.6.113.0", {"start": v(25.02, -54.79) * mm, "mid": v(25.17, -54.26) * mm, "end": v(25.06, -53.72) * mm});
            skArc(sketch, "E80.10.113.0", {"start": v(24.19, -54.11) * mm, "mid": v(24.52, -54.55) * mm, "end": v(25.02, -54.79) * mm});
            skLineSegment(sketch, "E80.14.113.0", {"start": v(23.76, -53.13) * mm, "end": v(24.19, -54.11) * mm});
            skLineSegment(sketch, "E80.17.113.0", {"start": v(23.76, -53.13) * mm, "end": v(23.33, -53.32) * mm});
            skLineSegment(sketch, "E80.2.114.0", {"start": v(26.25, -51.94) * mm, "end": v(26.67, -51.73) * mm});
            skLineSegment(sketch, "E80.3.114.0", {"start": v(26.25, -51.94) * mm, "end": v(26.75, -52.9) * mm});
            skArc(sketch, "E80.6.114.0", {"start": v(26.75, -53.96) * mm, "mid": v(26.88, -53.43) * mm, "end": v(26.75, -52.9) * mm});
            skArc(sketch, "E80.10.114.0", {"start": v(25.9, -53.32) * mm, "mid": v(26.24, -53.75) * mm, "end": v(26.75, -53.96) * mm});
            skLineSegment(sketch, "E80.14.114.0", {"start": v(25.44, -52.35) * mm, "end": v(25.9, -53.32) * mm});
            skLineSegment(sketch, "E80.17.114.0", {"start": v(25.44, -52.35) * mm, "end": v(25.01, -52.55) * mm});
            skLineSegment(sketch, "E80.2.115.0", {"start": v(27.89, -51.08) * mm, "end": v(28.3, -50.86) * mm});
            skLineSegment(sketch, "E80.3.115.0", {"start": v(27.89, -51.08) * mm, "end": v(28.41, -52.02) * mm});
            skArc(sketch, "E80.6.115.0", {"start": v(28.44, -53.09) * mm, "mid": v(28.56, -52.55) * mm, "end": v(28.41, -52.02) * mm});
            skArc(sketch, "E80.10.115.0", {"start": v(27.57, -52.47) * mm, "mid": v(27.93, -52.89) * mm, "end": v(28.44, -53.09) * mm});
            skLineSegment(sketch, "E80.14.115.0", {"start": v(27.08, -51.52) * mm, "end": v(27.57, -52.47) * mm});
            skLineSegment(sketch, "E80.17.115.0", {"start": v(27.08, -51.52) * mm, "end": v(26.67, -51.73) * mm});
            skLineSegment(sketch, "E80.2.116.0", {"start": v(29.5, -50.17) * mm, "end": v(29.9, -49.93) * mm});
            skLineSegment(sketch, "E80.3.116.0", {"start": v(29.5, -50.17) * mm, "end": v(30.05, -51.1) * mm});
            skArc(sketch, "E80.6.116.0", {"start": v(30.11, -52.16) * mm, "mid": v(30.21, -51.62) * mm, "end": v(30.05, -51.1) * mm});
            skArc(sketch, "E80.10.116.0", {"start": v(29.22, -51.57) * mm, "mid": v(29.6, -51.97) * mm, "end": v(30.11, -52.16) * mm});
            skLineSegment(sketch, "E80.14.116.0", {"start": v(28.7, -50.63) * mm, "end": v(29.22, -51.57) * mm});
            skLineSegment(sketch, "E80.17.116.0", {"start": v(28.7, -50.63) * mm, "end": v(28.3, -50.86) * mm});
            skLineSegment(sketch, "E80.2.117.0", {"start": v(31.07, -49.21) * mm, "end": v(31.47, -48.96) * mm});
            skLineSegment(sketch, "E80.3.117.0", {"start": v(31.07, -49.21) * mm, "end": v(31.65, -50.11) * mm});
            skArc(sketch, "E80.6.117.0", {"start": v(31.75, -51.18) * mm, "mid": v(31.83, -50.63) * mm, "end": v(31.65, -50.11) * mm});
            skArc(sketch, "E80.10.117.0", {"start": v(30.85, -50.62) * mm, "mid": v(31.23, -51) * mm, "end": v(31.75, -51.18) * mm});
            skLineSegment(sketch, "E80.14.117.0", {"start": v(30.3, -49.7) * mm, "end": v(30.85, -50.62) * mm});
            skLineSegment(sketch, "E80.17.117.0", {"start": v(30.3, -49.7) * mm, "end": v(29.9, -49.93) * mm});
            skLineSegment(sketch, "E80.2.118.0", {"start": v(32.62, -48.2) * mm, "end": v(33, -47.94) * mm});
            skLineSegment(sketch, "E80.3.118.0", {"start": v(32.62, -48.2) * mm, "end": v(33.23, -49.08) * mm});
            skArc(sketch, "E80.6.118.0", {"start": v(33.36, -50.14) * mm, "mid": v(33.42, -49.6) * mm, "end": v(33.23, -49.08) * mm});
            skArc(sketch, "E80.10.118.0", {"start": v(32.44, -49.61) * mm, "mid": v(32.83, -50) * mm, "end": v(33.36, -50.14) * mm});
            skLineSegment(sketch, "E80.14.118.0", {"start": v(31.86, -48.7) * mm, "end": v(32.44, -49.61) * mm});
            skLineSegment(sketch, "E80.17.118.0", {"start": v(31.86, -48.7) * mm, "end": v(31.47, -48.96) * mm});
            skLineSegment(sketch, "E80.2.119.0", {"start": v(34.13, -47.14) * mm, "end": v(34.5, -46.87) * mm});
            skLineSegment(sketch, "E80.3.119.0", {"start": v(34.13, -47.14) * mm, "end": v(34.77, -48) * mm});
            skArc(sketch, "E80.6.119.0", {"start": v(34.94, -49.06) * mm, "mid": v(34.98, -48.51) * mm, "end": v(34.77, -48) * mm});
            skArc(sketch, "E80.10.119.0", {"start": v(34, -48.56) * mm, "mid": v(34.4, -48.92) * mm, "end": v(34.94, -49.06) * mm});
            skLineSegment(sketch, "E80.14.119.0", {"start": v(33.39, -47.67) * mm, "end": v(34, -48.56) * mm});
            skLineSegment(sketch, "E80.17.119.0", {"start": v(33.39, -47.67) * mm, "end": v(33, -47.94) * mm});
            skLineSegment(sketch, "E80.2.120.0", {"start": v(35.61, -46.04) * mm, "end": v(35.98, -45.75) * mm});
            skLineSegment(sketch, "E80.3.120.0", {"start": v(35.61, -46.04) * mm, "end": v(36.27, -46.88) * mm});
            skArc(sketch, "E80.6.120.0", {"start": v(36.47, -47.93) * mm, "mid": v(36.5, -47.38) * mm, "end": v(36.27, -46.88) * mm});
            skArc(sketch, "E80.10.120.0", {"start": v(35.52, -47.45) * mm, "mid": v(35.94, -47.8) * mm, "end": v(36.47, -47.93) * mm});
            skLineSegment(sketch, "E80.14.120.0", {"start": v(34.88, -46.6) * mm, "end": v(35.52, -47.45) * mm});
            skLineSegment(sketch, "E80.17.120.0", {"start": v(34.88, -46.6) * mm, "end": v(34.5, -46.87) * mm});
            skLineSegment(sketch, "E80.2.121.0", {"start": v(37.05, -44.88) * mm, "end": v(37.41, -44.58) * mm});
            skLineSegment(sketch, "E80.3.121.0", {"start": v(37.05, -44.88) * mm, "end": v(37.74, -45.7) * mm});
            skArc(sketch, "E80.6.121.0", {"start": v(37.98, -46.75) * mm, "mid": v(37.99, -46.2) * mm, "end": v(37.74, -45.7) * mm});
            skArc(sketch, "E80.10.121.0", {"start": v(37, -46.3) * mm, "mid": v(37.44, -46.64) * mm, "end": v(37.98, -46.75) * mm});
            skLineSegment(sketch, "E80.14.121.0", {"start": v(36.34, -45.46) * mm, "end": v(37, -46.3) * mm});
            skLineSegment(sketch, "E80.17.121.0", {"start": v(36.34, -45.46) * mm, "end": v(35.98, -45.75) * mm});
            skLineSegment(sketch, "E80.2.122.0", {"start": v(38.46, -43.69) * mm, "end": v(38.8, -43.37) * mm});
            skLineSegment(sketch, "E80.3.122.0", {"start": v(38.46, -43.69) * mm, "end": v(39.17, -44.48) * mm});
            skArc(sketch, "E80.6.122.0", {"start": v(39.44, -45.52) * mm, "mid": v(39.43, -44.97) * mm, "end": v(39.17, -44.48) * mm});
            skArc(sketch, "E80.10.122.0", {"start": v(38.46, -45.1) * mm, "mid": v(38.9, -45.43) * mm, "end": v(39.44, -45.52) * mm});
            skLineSegment(sketch, "E80.14.122.0", {"start": v(37.77, -44.28) * mm, "end": v(38.46, -45.1) * mm});
            skLineSegment(sketch, "E80.17.122.0", {"start": v(37.77, -44.28) * mm, "end": v(37.41, -44.58) * mm});
            skLineSegment(sketch, "E80.2.123.0", {"start": v(39.82, -42.44) * mm, "end": v(40.16, -42.12) * mm});
            skLineSegment(sketch, "E80.3.123.0", {"start": v(39.82, -42.44) * mm, "end": v(40.57, -43.22) * mm});
            skArc(sketch, "E80.6.123.0", {"start": v(40.87, -44.24) * mm, "mid": v(40.84, -43.7) * mm, "end": v(40.57, -43.22) * mm});
            skArc(sketch, "E80.10.123.0", {"start": v(39.87, -43.86) * mm, "mid": v(40.32, -44.18) * mm, "end": v(40.87, -44.24) * mm});
            skLineSegment(sketch, "E80.14.123.0", {"start": v(39.15, -43.06) * mm, "end": v(39.87, -43.86) * mm});
            skLineSegment(sketch, "E80.17.123.0", {"start": v(39.15, -43.06) * mm, "end": v(38.8, -43.37) * mm});
            skLineSegment(sketch, "E80.2.124.0", {"start": v(41.15, -41.16) * mm, "end": v(41.48, -40.83) * mm});
            skLineSegment(sketch, "E80.3.124.0", {"start": v(41.15, -41.16) * mm, "end": v(41.92, -41.9) * mm});
            skArc(sketch, "E80.6.124.0", {"start": v(42.25, -42.92) * mm, "mid": v(42.2, -42.38) * mm, "end": v(41.92, -41.9) * mm});
            skArc(sketch, "E80.10.124.0", {"start": v(41.24, -42.58) * mm, "mid": v(41.7, -42.87) * mm, "end": v(42.25, -42.92) * mm});
            skLineSegment(sketch, "E80.14.124.0", {"start": v(40.5, -41.8) * mm, "end": v(41.24, -42.58) * mm});
            skLineSegment(sketch, "E80.17.124.0", {"start": v(40.5, -41.8) * mm, "end": v(40.16, -42.12) * mm});
            skLineSegment(sketch, "E80.2.125.0", {"start": v(42.44, -39.83) * mm, "end": v(42.75, -39.49) * mm});
            skLineSegment(sketch, "E80.3.125.0", {"start": v(42.44, -39.83) * mm, "end": v(43.23, -40.56) * mm});
            skArc(sketch, "E80.6.125.0", {"start": v(43.59, -41.56) * mm, "mid": v(43.53, -41.02) * mm, "end": v(43.23, -40.56) * mm});
            skArc(sketch, "E80.10.125.0", {"start": v(42.57, -41.25) * mm, "mid": v(43.04, -41.53) * mm, "end": v(43.59, -41.56) * mm});
            skLineSegment(sketch, "E80.14.125.0", {"start": v(41.8, -40.5) * mm, "end": v(42.57, -41.25) * mm});
            skLineSegment(sketch, "E80.17.125.0", {"start": v(41.8, -40.5) * mm, "end": v(41.48, -40.83) * mm});
            skLineSegment(sketch, "E80.2.126.0", {"start": v(43.68, -38.47) * mm, "end": v(43.98, -38.11) * mm});
            skLineSegment(sketch, "E80.3.126.0", {"start": v(43.68, -38.47) * mm, "end": v(44.5, -39.17) * mm});
            skArc(sketch, "E80.6.126.0", {"start": v(44.89, -40.16) * mm, "mid": v(44.8, -39.61) * mm, "end": v(44.5, -39.17) * mm});
            skArc(sketch, "E80.10.126.0", {"start": v(43.86, -39.88) * mm, "mid": v(44.34, -40.14) * mm, "end": v(44.89, -40.16) * mm});
            skLineSegment(sketch, "E80.14.126.0", {"start": v(43.07, -39.15) * mm, "end": v(43.86, -39.88) * mm});
            skLineSegment(sketch, "E80.17.126.0", {"start": v(43.07, -39.15) * mm, "end": v(42.75, -39.49) * mm});
            skLineSegment(sketch, "E80.2.127.0", {"start": v(44.88, -37.06) * mm, "end": v(45.17, -36.7) * mm});
            skLineSegment(sketch, "E80.3.127.0", {"start": v(44.88, -37.06) * mm, "end": v(45.71, -37.74) * mm});
            skArc(sketch, "E80.6.127.0", {"start": v(46.14, -38.71) * mm, "mid": v(46.04, -38.17) * mm, "end": v(45.71, -37.74) * mm});
            skArc(sketch, "E80.10.127.0", {"start": v(45.1, -38.46) * mm, "mid": v(45.59, -38.72) * mm, "end": v(46.14, -38.71) * mm});
            skLineSegment(sketch, "E80.14.127.0", {"start": v(44.3, -37.76) * mm, "end": v(45.1, -38.46) * mm});
            skLineSegment(sketch, "E80.17.127.0", {"start": v(44.3, -37.76) * mm, "end": v(43.98, -38.11) * mm});
            skLineSegment(sketch, "E80.2.128.0", {"start": v(46.03, -35.62) * mm, "end": v(46.31, -35.25) * mm});
            skLineSegment(sketch, "E80.3.128.0", {"start": v(46.03, -35.62) * mm, "end": v(46.89, -36.27) * mm});
            skArc(sketch, "E80.6.128.0", {"start": v(47.34, -37.23) * mm, "mid": v(47.23, -36.7) * mm, "end": v(46.89, -36.27) * mm});
            skArc(sketch, "E80.10.128.0", {"start": v(46.3, -37.01) * mm, "mid": v(46.8, -37.25) * mm, "end": v(47.34, -37.23) * mm});
            skLineSegment(sketch, "E80.14.128.0", {"start": v(45.47, -36.34) * mm, "end": v(46.3, -37.01) * mm});
            skLineSegment(sketch, "E80.17.128.0", {"start": v(45.47, -36.34) * mm, "end": v(45.17, -36.7) * mm});
            skLineSegment(sketch, "E80.2.129.0", {"start": v(47.14, -34.14) * mm, "end": v(47.4, -33.76) * mm});
            skLineSegment(sketch, "E80.3.129.0", {"start": v(47.14, -34.14) * mm, "end": v(48.01, -34.76) * mm});
            skArc(sketch, "E80.6.129.0", {"start": v(48.5, -35.7) * mm, "mid": v(48.37, -35.18) * mm, "end": v(48.01, -34.76) * mm});
            skArc(sketch, "E80.10.129.0", {"start": v(47.45, -35.53) * mm, "mid": v(47.95, -35.75) * mm, "end": v(48.5, -35.7) * mm});
            skLineSegment(sketch, "E80.14.129.0", {"start": v(46.6, -34.88) * mm, "end": v(47.45, -35.53) * mm});
            skLineSegment(sketch, "E80.17.129.0", {"start": v(46.6, -34.88) * mm, "end": v(46.31, -35.25) * mm});
            skLineSegment(sketch, "E80.2.130.0", {"start": v(48.2, -32.63) * mm, "end": v(48.46, -32.24) * mm});
            skLineSegment(sketch, "E80.3.130.0", {"start": v(48.2, -32.63) * mm, "end": v(49.1, -33.22) * mm});
            skArc(sketch, "E80.6.130.0", {"start": v(49.6, -34.15) * mm, "mid": v(49.46, -33.62) * mm, "end": v(49.1, -33.22) * mm});
            skArc(sketch, "E80.10.130.0", {"start": v(48.55, -34) * mm, "mid": v(49.06, -34.2) * mm, "end": v(49.6, -34.15) * mm});
            skLineSegment(sketch, "E80.14.130.0", {"start": v(47.68, -33.38) * mm, "end": v(48.55, -34) * mm});
            skLineSegment(sketch, "E80.17.130.0", {"start": v(47.68, -33.38) * mm, "end": v(47.4, -33.76) * mm});
            skLineSegment(sketch, "E80.2.131.0", {"start": v(49.2, -31.08) * mm, "end": v(49.45, -30.68) * mm});
            skLineSegment(sketch, "E80.3.131.0", {"start": v(49.2, -31.08) * mm, "end": v(50.12, -31.64) * mm});
            skArc(sketch, "E80.6.131.0", {"start": v(50.67, -32.56) * mm, "mid": v(50.5, -32.04) * mm, "end": v(50.12, -31.64) * mm});
            skArc(sketch, "E80.10.131.0", {"start": v(49.6, -32.45) * mm, "mid": v(50.12, -32.63) * mm, "end": v(50.67, -32.56) * mm});
            skLineSegment(sketch, "E80.14.131.0", {"start": v(48.71, -31.85) * mm, "end": v(49.6, -32.45) * mm});
            skLineSegment(sketch, "E80.17.131.0", {"start": v(48.71, -31.85) * mm, "end": v(48.46, -32.24) * mm});
            skLineSegment(sketch, "E80.2.132.0", {"start": v(50.17, -29.5) * mm, "end": v(50.4, -29.1) * mm});
            skLineSegment(sketch, "E80.3.132.0", {"start": v(50.17, -29.5) * mm, "end": v(51.1, -30.04) * mm});
            skArc(sketch, "E80.6.132.0", {"start": v(51.67, -30.94) * mm, "mid": v(51.5, -30.42) * mm, "end": v(51.1, -30.04) * mm});
            skArc(sketch, "E80.10.132.0", {"start": v(50.61, -30.85) * mm, "mid": v(51.13, -31.03) * mm, "end": v(51.67, -30.94) * mm});
            skLineSegment(sketch, "E80.14.132.0", {"start": v(49.7, -30.29) * mm, "end": v(50.61, -30.85) * mm});
            skLineSegment(sketch, "E80.17.132.0", {"start": v(49.7, -30.29) * mm, "end": v(49.45, -30.68) * mm});
            skLineSegment(sketch, "E80.2.133.0", {"start": v(51.08, -27.9) * mm, "end": v(51.3, -27.49) * mm});
            skLineSegment(sketch, "E80.3.133.0", {"start": v(51.08, -27.9) * mm, "end": v(52.03, -28.4) * mm});
            skArc(sketch, "E80.6.133.0", {"start": v(52.63, -29.28) * mm, "mid": v(52.44, -28.77) * mm, "end": v(52.03, -28.4) * mm});
            skArc(sketch, "E80.10.133.0", {"start": v(51.56, -29.23) * mm, "mid": v(52.1, -29.39) * mm, "end": v(52.63, -29.28) * mm});
            skLineSegment(sketch, "E80.14.133.0", {"start": v(50.64, -28.7) * mm, "end": v(51.56, -29.23) * mm});
            skLineSegment(sketch, "E80.17.133.0", {"start": v(50.64, -28.7) * mm, "end": v(50.4, -29.1) * mm});
            skLineSegment(sketch, "E80.2.134.0", {"start": v(51.94, -26.26) * mm, "end": v(52.15, -25.84) * mm});
            skLineSegment(sketch, "E80.3.134.0", {"start": v(51.94, -26.26) * mm, "end": v(52.9, -26.74) * mm});
            skArc(sketch, "E80.6.134.0", {"start": v(53.53, -27.6) * mm, "mid": v(53.32, -27.1) * mm, "end": v(52.9, -26.74) * mm});
            skArc(sketch, "E80.10.134.0", {"start": v(52.47, -27.58) * mm, "mid": v(53, -27.72) * mm, "end": v(53.53, -27.6) * mm});
            skLineSegment(sketch, "E80.14.134.0", {"start": v(51.52, -27.07) * mm, "end": v(52.47, -27.58) * mm});
            skLineSegment(sketch, "E80.17.134.0", {"start": v(51.52, -27.07) * mm, "end": v(51.3, -27.49) * mm});
            skLineSegment(sketch, "E80.2.135.0", {"start": v(52.75, -24.6) * mm, "end": v(52.94, -24.18) * mm});
            skLineSegment(sketch, "E80.3.135.0", {"start": v(52.75, -24.6) * mm, "end": v(53.72, -25.05) * mm});
            skArc(sketch, "E80.6.135.0", {"start": v(54.38, -25.89) * mm, "mid": v(54.16, -25.39) * mm, "end": v(53.72, -25.05) * mm});
            skArc(sketch, "E80.10.135.0", {"start": v(53.31, -25.9) * mm, "mid": v(53.85, -26.03) * mm, "end": v(54.38, -25.89) * mm});
            skLineSegment(sketch, "E80.14.135.0", {"start": v(52.35, -25.43) * mm, "end": v(53.31, -25.9) * mm});
            skLineSegment(sketch, "E80.17.135.0", {"start": v(52.35, -25.43) * mm, "end": v(52.15, -25.84) * mm});
            skLineSegment(sketch, "E80.2.136.0", {"start": v(53.5, -22.92) * mm, "end": v(53.68, -22.49) * mm});
            skLineSegment(sketch, "E80.3.136.0", {"start": v(53.5, -22.92) * mm, "end": v(54.5, -23.33) * mm});
            skArc(sketch, "E80.6.136.0", {"start": v(55.18, -24.15) * mm, "mid": v(54.93, -23.65) * mm, "end": v(54.5, -23.33) * mm});
            skArc(sketch, "E80.10.136.0", {"start": v(54.1, -24.2) * mm, "mid": v(54.65, -24.3) * mm, "end": v(55.18, -24.15) * mm});
            skLineSegment(sketch, "E80.14.136.0", {"start": v(53.13, -23.75) * mm, "end": v(54.1, -24.2) * mm});
            skLineSegment(sketch, "E80.17.136.0", {"start": v(53.13, -23.75) * mm, "end": v(52.94, -24.18) * mm});
            skLineSegment(sketch, "E80.2.137.0", {"start": v(54.2, -21.2) * mm, "end": v(54.37, -20.77) * mm});
            skLineSegment(sketch, "E80.3.137.0", {"start": v(54.2, -21.2) * mm, "end": v(55.2, -21.59) * mm});
            skArc(sketch, "E80.6.137.0", {"start": v(55.91, -22.38) * mm, "mid": v(55.66, -21.9) * mm, "end": v(55.2, -21.59) * mm});
            skArc(sketch, "E80.10.137.0", {"start": v(54.85, -22.47) * mm, "mid": v(55.4, -22.56) * mm, "end": v(55.91, -22.38) * mm});
            skLineSegment(sketch, "E80.14.137.0", {"start": v(53.86, -22.05) * mm, "end": v(54.85, -22.47) * mm});
            skLineSegment(sketch, "E80.17.137.0", {"start": v(53.86, -22.05) * mm, "end": v(53.68, -22.49) * mm});
            skLineSegment(sketch, "E80.2.138.0", {"start": v(54.85, -19.48) * mm, "end": v(55, -19.04) * mm});
            skLineSegment(sketch, "E80.3.138.0", {"start": v(54.85, -19.48) * mm, "end": v(55.86, -19.83) * mm});
            skArc(sketch, "E80.6.138.0", {"start": v(56.6, -20.6) * mm, "mid": v(56.32, -20.12) * mm, "end": v(55.86, -19.83) * mm});
            skArc(sketch, "E80.10.138.0", {"start": v(55.54, -20.72) * mm, "mid": v(56.08, -20.79) * mm, "end": v(56.6, -20.6) * mm});
            skLineSegment(sketch, "E80.14.138.0", {"start": v(54.53, -20.33) * mm, "end": v(55.54, -20.72) * mm});
            skLineSegment(sketch, "E80.17.138.0", {"start": v(54.53, -20.33) * mm, "end": v(54.37, -20.77) * mm});
            skLineSegment(sketch, "E80.2.139.0", {"start": v(55.44, -17.73) * mm, "end": v(55.58, -17.28) * mm});
            skLineSegment(sketch, "E80.3.139.0", {"start": v(55.44, -17.73) * mm, "end": v(56.46, -18.04) * mm});
            skArc(sketch, "E80.6.139.0", {"start": v(57.22, -18.8) * mm, "mid": v(56.93, -18.33) * mm, "end": v(56.46, -18.04) * mm});
            skArc(sketch, "E80.10.139.0", {"start": v(56.16, -18.95) * mm, "mid": v(56.71, -19) * mm, "end": v(57.22, -18.8) * mm});
            skLineSegment(sketch, "E80.14.139.0", {"start": v(55.15, -18.6) * mm, "end": v(56.16, -18.95) * mm});
            skLineSegment(sketch, "E80.17.139.0", {"start": v(55.15, -18.6) * mm, "end": v(55, -19.04) * mm});
            skLineSegment(sketch, "E80.2.140.0", {"start": v(55.97, -15.96) * mm, "end": v(56.1, -15.5) * mm});
            skLineSegment(sketch, "E80.3.140.0", {"start": v(55.97, -15.96) * mm, "end": v(57, -16.24) * mm});
            skArc(sketch, "E80.6.140.0", {"start": v(57.79, -16.97) * mm, "mid": v(57.49, -16.5) * mm, "end": v(57, -16.24) * mm});
            skArc(sketch, "E80.10.140.0", {"start": v(56.74, -17.16) * mm, "mid": v(57.29, -17.2) * mm, "end": v(57.79, -16.97) * mm});
            skLineSegment(sketch, "E80.14.140.0", {"start": v(55.71, -16.84) * mm, "end": v(56.74, -17.16) * mm});
            skLineSegment(sketch, "E80.17.140.0", {"start": v(55.71, -16.84) * mm, "end": v(55.58, -17.28) * mm});
            skLineSegment(sketch, "E80.2.141.0", {"start": v(56.45, -14.17) * mm, "end": v(56.56, -13.72) * mm});
            skLineSegment(sketch, "E80.3.141.0", {"start": v(56.45, -14.17) * mm, "end": v(57.5, -14.43) * mm});
            skArc(sketch, "E80.6.141.0", {"start": v(58.3, -15.13) * mm, "mid": v(57.98, -14.68) * mm, "end": v(57.5, -14.43) * mm});
            skArc(sketch, "E80.10.141.0", {"start": v(57.25, -15.35) * mm, "mid": v(57.8, -15.36) * mm, "end": v(58.3, -15.13) * mm});
            skLineSegment(sketch, "E80.14.141.0", {"start": v(56.22, -15.06) * mm, "end": v(57.25, -15.35) * mm});
            skLineSegment(sketch, "E80.17.141.0", {"start": v(56.22, -15.06) * mm, "end": v(56.1, -15.5) * mm});
            skLineSegment(sketch, "E80.2.142.0", {"start": v(56.87, -12.38) * mm, "end": v(56.97, -11.92) * mm});
            skLineSegment(sketch, "E80.3.142.0", {"start": v(56.87, -12.38) * mm, "end": v(57.92, -12.6) * mm});
            skArc(sketch, "E80.6.142.0", {"start": v(58.75, -13.27) * mm, "mid": v(58.42, -12.83) * mm, "end": v(57.92, -12.6) * mm});
            skArc(sketch, "E80.10.142.0", {"start": v(57.71, -13.52) * mm, "mid": v(58.26, -13.52) * mm, "end": v(58.75, -13.27) * mm});
            skLineSegment(sketch, "E80.14.142.0", {"start": v(56.67, -13.27) * mm, "end": v(57.71, -13.52) * mm});
            skLineSegment(sketch, "E80.17.142.0", {"start": v(56.67, -13.27) * mm, "end": v(56.56, -13.72) * mm});
            skLineSegment(sketch, "E80.2.143.0", {"start": v(57.23, -10.57) * mm, "end": v(57.32, -10.1) * mm});
            skLineSegment(sketch, "E80.3.143.0", {"start": v(57.23, -10.57) * mm, "end": v(58.3, -10.75) * mm});
            skArc(sketch, "E80.6.143.0", {"start": v(59.14, -11.4) * mm, "mid": v(58.8, -10.97) * mm, "end": v(58.3, -10.75) * mm});
            skArc(sketch, "E80.10.143.0", {"start": v(58.11, -11.68) * mm, "mid": v(58.66, -11.67) * mm, "end": v(59.14, -11.4) * mm});
            skLineSegment(sketch, "E80.14.143.0", {"start": v(57.06, -11.46) * mm, "end": v(58.11, -11.68) * mm});
            skLineSegment(sketch, "E80.17.143.0", {"start": v(57.06, -11.46) * mm, "end": v(56.97, -11.92) * mm});
            skLineSegment(sketch, "E80.2.144.0", {"start": v(57.54, -8.74) * mm, "end": v(57.6, -8.28) * mm});
            skLineSegment(sketch, "E80.3.144.0", {"start": v(57.54, -8.74) * mm, "end": v(58.6, -8.9) * mm});
            skArc(sketch, "E80.6.144.0", {"start": v(59.47, -9.52) * mm, "mid": v(59.11, -9.1) * mm, "end": v(58.6, -8.9) * mm});
            skArc(sketch, "E80.10.144.0", {"start": v(58.45, -9.83) * mm, "mid": v(59, -9.8) * mm, "end": v(59.47, -9.52) * mm});
            skLineSegment(sketch, "E80.14.144.0", {"start": v(57.4, -9.65) * mm, "end": v(58.45, -9.83) * mm});
            skLineSegment(sketch, "E80.17.144.0", {"start": v(57.4, -9.65) * mm, "end": v(57.32, -10.1) * mm});
            skLineSegment(sketch, "E80.2.145.0", {"start": v(57.79, -6.91) * mm, "end": v(57.84, -6.45) * mm});
            skLineSegment(sketch, "E80.3.145.0", {"start": v(57.79, -6.91) * mm, "end": v(58.86, -7.03) * mm});
            skArc(sketch, "E80.6.145.0", {"start": v(59.74, -7.62) * mm, "mid": v(59.37, -7.22) * mm, "end": v(58.86, -7.03) * mm});
            skArc(sketch, "E80.10.145.0", {"start": v(58.74, -7.98) * mm, "mid": v(59.28, -7.92) * mm, "end": v(59.74, -7.62) * mm});
            skLineSegment(sketch, "E80.14.145.0", {"start": v(57.67, -7.82) * mm, "end": v(58.74, -7.98) * mm});
            skLineSegment(sketch, "E80.17.145.0", {"start": v(57.67, -7.82) * mm, "end": v(57.6, -8.28) * mm});
            skLineSegment(sketch, "E80.2.146.0", {"start": v(57.98, -5.08) * mm, "end": v(58.02, -4.61) * mm});
            skLineSegment(sketch, "E80.3.146.0", {"start": v(57.98, -5.08) * mm, "end": v(59.05, -5.16) * mm});
            skArc(sketch, "E80.6.146.0", {"start": v(59.96, -5.73) * mm, "mid": v(59.57, -5.33) * mm, "end": v(59.05, -5.16) * mm});
            skArc(sketch, "E80.10.146.0", {"start": v(58.96, -6.1) * mm, "mid": v(59.5, -6.04) * mm, "end": v(59.96, -5.73) * mm});
            skLineSegment(sketch, "E80.14.146.0", {"start": v(57.9, -5.99) * mm, "end": v(58.96, -6.1) * mm});
            skLineSegment(sketch, "E80.17.146.0", {"start": v(57.9, -5.99) * mm, "end": v(57.84, -6.45) * mm});
            skLineSegment(sketch, "E80.2.147.0", {"start": v(58.11, -3.24) * mm, "end": v(58.13, -2.77) * mm});
            skLineSegment(sketch, "E80.3.147.0", {"start": v(58.11, -3.24) * mm, "end": v(59.18, -3.28) * mm});
            skArc(sketch, "E80.6.147.0", {"start": v(60.1, -3.82) * mm, "mid": v(59.71, -3.44) * mm, "end": v(59.18, -3.28) * mm});
            skArc(sketch, "E80.10.147.0", {"start": v(59.12, -4.23) * mm, "mid": v(59.67, -4.15) * mm, "end": v(60.1, -3.82) * mm});
            skLineSegment(sketch, "E80.14.147.0", {"start": v(58.05, -4.15) * mm, "end": v(59.12, -4.23) * mm});
            skLineSegment(sketch, "E80.17.147.0", {"start": v(58.05, -4.15) * mm, "end": v(58.02, -4.61) * mm});
            skLineSegment(sketch, "E80.2.148.0", {"start": v(58.19, -1.39) * mm, "end": v(58.2, -0.92) * mm});
            skLineSegment(sketch, "E80.3.148.0", {"start": v(58.19, -1.39) * mm, "end": v(59.26, -1.4) * mm});
            skArc(sketch, "E80.6.148.0", {"start": v(60.2, -1.91) * mm, "mid": v(59.79, -1.54) * mm, "end": v(59.26, -1.4) * mm});
            skArc(sketch, "E80.10.148.0", {"start": v(59.23, -2.36) * mm, "mid": v(59.77, -2.25) * mm, "end": v(60.2, -1.91) * mm});
            skLineSegment(sketch, "E80.14.148.0", {"start": v(58.16, -2.3) * mm, "end": v(59.23, -2.36) * mm});
            skLineSegment(sketch, "E80.17.148.0", {"start": v(58.16, -2.3) * mm, "end": v(58.13, -2.77) * mm});
            skLineSegment(sketch, "E80.2.149.0", {"start": v(58.2, 0.46) * mm, "end": v(58.2, 0.92) * mm});
            skLineSegment(sketch, "E80.3.149.0", {"start": v(58.2, 0.46) * mm, "end": v(59.27, 0.48) * mm});
            skArc(sketch, "E80.6.149.0", {"start": v(60.23, 0) * mm, "mid": v(59.8, 0.35) * mm, "end": v(59.27, 0.48) * mm});
            skArc(sketch, "E80.10.149.0", {"start": v(59.27, -0.48) * mm, "mid": v(59.8, -0.35) * mm, "end": v(60.23, 0) * mm});
            skLineSegment(sketch, "E80.14.149.0", {"start": v(58.2, -0.46) * mm, "end": v(59.27, -0.48) * mm});
            skLineSegment(sketch, "E80.17.149.0", {"start": v(58.2, -0.46) * mm, "end": v(58.2, -0.92) * mm});
            skLineSegment(sketch, "E80.2.150.0", {"start": v(58.16, 2.3) * mm, "end": v(58.13, 2.77) * mm});
            skLineSegment(sketch, "E80.3.150.0", {"start": v(58.16, 2.3) * mm, "end": v(59.23, 2.36) * mm});
            skArc(sketch, "E80.6.150.0", {"start": v(60.2, 1.91) * mm, "mid": v(59.77, 2.25) * mm, "end": v(59.23, 2.36) * mm});
            skArc(sketch, "E80.10.150.0", {"start": v(59.26, 1.4) * mm, "mid": v(59.79, 1.54) * mm, "end": v(60.2, 1.91) * mm});
            skLineSegment(sketch, "E80.14.150.0", {"start": v(58.19, 1.39) * mm, "end": v(59.26, 1.4) * mm});
            skLineSegment(sketch, "E80.17.150.0", {"start": v(58.19, 1.39) * mm, "end": v(58.2, 0.92) * mm});
            skLineSegment(sketch, "E80.2.151.0", {"start": v(58.05, 4.15) * mm, "end": v(58.02, 4.61) * mm});
            skLineSegment(sketch, "E80.3.151.0", {"start": v(58.05, 4.15) * mm, "end": v(59.12, 4.23) * mm});
            skArc(sketch, "E80.6.151.0", {"start": v(60.1, 3.82) * mm, "mid": v(59.67, 4.15) * mm, "end": v(59.12, 4.23) * mm});
            skArc(sketch, "E80.10.151.0", {"start": v(59.18, 3.28) * mm, "mid": v(59.71, 3.44) * mm, "end": v(60.1, 3.82) * mm});
            skLineSegment(sketch, "E80.14.151.0", {"start": v(58.11, 3.24) * mm, "end": v(59.18, 3.28) * mm});
            skLineSegment(sketch, "E80.17.151.0", {"start": v(58.11, 3.24) * mm, "end": v(58.13, 2.77) * mm});
            skLineSegment(sketch, "E80.2.152.0", {"start": v(57.9, 5.99) * mm, "end": v(57.84, 6.45) * mm});
            skLineSegment(sketch, "E80.3.152.0", {"start": v(57.9, 5.99) * mm, "end": v(58.96, 6.1) * mm});
            skArc(sketch, "E80.6.152.0", {"start": v(59.96, 5.73) * mm, "mid": v(59.5, 6.04) * mm, "end": v(58.96, 6.1) * mm});
            skArc(sketch, "E80.10.152.0", {"start": v(59.05, 5.16) * mm, "mid": v(59.57, 5.33) * mm, "end": v(59.96, 5.73) * mm});
            skLineSegment(sketch, "E80.14.152.0", {"start": v(57.98, 5.08) * mm, "end": v(59.05, 5.16) * mm});
            skLineSegment(sketch, "E80.17.152.0", {"start": v(57.98, 5.08) * mm, "end": v(58.02, 4.61) * mm});
            skLineSegment(sketch, "E80.2.153.0", {"start": v(57.67, 7.82) * mm, "end": v(57.6, 8.28) * mm});
            skLineSegment(sketch, "E80.3.153.0", {"start": v(57.67, 7.82) * mm, "end": v(58.74, 7.98) * mm});
            skArc(sketch, "E80.6.153.0", {"start": v(59.74, 7.62) * mm, "mid": v(59.28, 7.92) * mm, "end": v(58.74, 7.98) * mm});
            skArc(sketch, "E80.10.153.0", {"start": v(58.86, 7.03) * mm, "mid": v(59.37, 7.22) * mm, "end": v(59.74, 7.62) * mm});
            skLineSegment(sketch, "E80.14.153.0", {"start": v(57.79, 6.91) * mm, "end": v(58.86, 7.03) * mm});
            skLineSegment(sketch, "E80.17.153.0", {"start": v(57.79, 6.91) * mm, "end": v(57.84, 6.45) * mm});
            skLineSegment(sketch, "E80.2.154.0", {"start": v(57.4, 9.65) * mm, "end": v(57.32, 10.1) * mm});
            skLineSegment(sketch, "E80.3.154.0", {"start": v(57.4, 9.65) * mm, "end": v(58.45, 9.83) * mm});
            skArc(sketch, "E80.6.154.0", {"start": v(59.47, 9.52) * mm, "mid": v(59, 9.8) * mm, "end": v(58.45, 9.83) * mm});
            skArc(sketch, "E80.10.154.0", {"start": v(58.6, 8.9) * mm, "mid": v(59.11, 9.1) * mm, "end": v(59.47, 9.52) * mm});
            skLineSegment(sketch, "E80.14.154.0", {"start": v(57.54, 8.74) * mm, "end": v(58.6, 8.9) * mm});
            skLineSegment(sketch, "E80.17.154.0", {"start": v(57.54, 8.74) * mm, "end": v(57.6, 8.28) * mm});
            skLineSegment(sketch, "E80.2.155.0", {"start": v(57.06, 11.46) * mm, "end": v(56.97, 11.92) * mm});
            skLineSegment(sketch, "E80.3.155.0", {"start": v(57.06, 11.46) * mm, "end": v(58.11, 11.68) * mm});
            skArc(sketch, "E80.6.155.0", {"start": v(59.14, 11.4) * mm, "mid": v(58.66, 11.67) * mm, "end": v(58.11, 11.68) * mm});
            skArc(sketch, "E80.10.155.0", {"start": v(58.3, 10.75) * mm, "mid": v(58.8, 10.97) * mm, "end": v(59.14, 11.4) * mm});
            skLineSegment(sketch, "E80.14.155.0", {"start": v(57.23, 10.57) * mm, "end": v(58.3, 10.75) * mm});
            skLineSegment(sketch, "E80.17.155.0", {"start": v(57.23, 10.57) * mm, "end": v(57.32, 10.1) * mm});
            skLineSegment(sketch, "E80.2.156.0", {"start": v(56.67, 13.27) * mm, "end": v(56.56, 13.72) * mm});
            skLineSegment(sketch, "E80.3.156.0", {"start": v(56.67, 13.27) * mm, "end": v(57.71, 13.52) * mm});
            skArc(sketch, "E80.6.156.0", {"start": v(58.75, 13.27) * mm, "mid": v(58.26, 13.52) * mm, "end": v(57.71, 13.52) * mm});
            skArc(sketch, "E80.10.156.0", {"start": v(57.92, 12.6) * mm, "mid": v(58.42, 12.83) * mm, "end": v(58.75, 13.27) * mm});
            skLineSegment(sketch, "E80.14.156.0", {"start": v(56.87, 12.38) * mm, "end": v(57.92, 12.6) * mm});
            skLineSegment(sketch, "E80.17.156.0", {"start": v(56.87, 12.38) * mm, "end": v(56.97, 11.92) * mm});
            skLineSegment(sketch, "E80.2.157.0", {"start": v(56.22, 15.06) * mm, "end": v(56.1, 15.5) * mm});
            skLineSegment(sketch, "E80.3.157.0", {"start": v(56.22, 15.06) * mm, "end": v(57.25, 15.35) * mm});
            skArc(sketch, "E80.6.157.0", {"start": v(58.3, 15.13) * mm, "mid": v(57.8, 15.36) * mm, "end": v(57.25, 15.35) * mm});
            skArc(sketch, "E80.10.157.0", {"start": v(57.5, 14.43) * mm, "mid": v(57.98, 14.68) * mm, "end": v(58.3, 15.13) * mm});
            skLineSegment(sketch, "E80.14.157.0", {"start": v(56.45, 14.17) * mm, "end": v(57.5, 14.43) * mm});
            skLineSegment(sketch, "E80.17.157.0", {"start": v(56.45, 14.17) * mm, "end": v(56.56, 13.72) * mm});
            skLineSegment(sketch, "E80.2.158.0", {"start": v(55.71, 16.84) * mm, "end": v(55.58, 17.28) * mm});
            skLineSegment(sketch, "E80.3.158.0", {"start": v(55.71, 16.84) * mm, "end": v(56.74, 17.16) * mm});
            skArc(sketch, "E80.6.158.0", {"start": v(57.79, 16.97) * mm, "mid": v(57.29, 17.2) * mm, "end": v(56.74, 17.16) * mm});
            skArc(sketch, "E80.10.158.0", {"start": v(57, 16.24) * mm, "mid": v(57.49, 16.5) * mm, "end": v(57.79, 16.97) * mm});
            skLineSegment(sketch, "E80.14.158.0", {"start": v(55.97, 15.96) * mm, "end": v(57, 16.24) * mm});
            skLineSegment(sketch, "E80.17.158.0", {"start": v(55.97, 15.96) * mm, "end": v(56.1, 15.5) * mm});
            skLineSegment(sketch, "E80.2.159.0", {"start": v(55.15, 18.6) * mm, "end": v(55, 19.04) * mm});
            skLineSegment(sketch, "E80.3.159.0", {"start": v(55.15, 18.6) * mm, "end": v(56.16, 18.95) * mm});
            skArc(sketch, "E80.6.159.0", {"start": v(57.22, 18.8) * mm, "mid": v(56.71, 19) * mm, "end": v(56.16, 18.95) * mm});
            skArc(sketch, "E80.10.159.0", {"start": v(56.46, 18.04) * mm, "mid": v(56.93, 18.33) * mm, "end": v(57.22, 18.8) * mm});
            skLineSegment(sketch, "E80.14.159.0", {"start": v(55.44, 17.73) * mm, "end": v(56.46, 18.04) * mm});
            skLineSegment(sketch, "E80.17.159.0", {"start": v(55.44, 17.73) * mm, "end": v(55.58, 17.28) * mm});
            skLineSegment(sketch, "E80.2.160.0", {"start": v(54.53, 20.33) * mm, "end": v(54.37, 20.77) * mm});
            skLineSegment(sketch, "E80.3.160.0", {"start": v(54.53, 20.33) * mm, "end": v(55.54, 20.72) * mm});
            skArc(sketch, "E80.6.160.0", {"start": v(56.6, 20.6) * mm, "mid": v(56.08, 20.79) * mm, "end": v(55.54, 20.72) * mm});
            skArc(sketch, "E80.10.160.0", {"start": v(55.86, 19.83) * mm, "mid": v(56.32, 20.12) * mm, "end": v(56.6, 20.6) * mm});
            skLineSegment(sketch, "E80.14.160.0", {"start": v(54.85, 19.48) * mm, "end": v(55.86, 19.83) * mm});
            skLineSegment(sketch, "E80.17.160.0", {"start": v(54.85, 19.48) * mm, "end": v(55, 19.04) * mm});
            skLineSegment(sketch, "E80.2.161.0", {"start": v(53.86, 22.05) * mm, "end": v(53.68, 22.49) * mm});
            skLineSegment(sketch, "E80.3.161.0", {"start": v(53.86, 22.05) * mm, "end": v(54.85, 22.47) * mm});
            skArc(sketch, "E80.6.161.0", {"start": v(55.91, 22.38) * mm, "mid": v(55.4, 22.56) * mm, "end": v(54.85, 22.47) * mm});
            skArc(sketch, "E80.10.161.0", {"start": v(55.2, 21.59) * mm, "mid": v(55.66, 21.9) * mm, "end": v(55.91, 22.38) * mm});
            skLineSegment(sketch, "E80.14.161.0", {"start": v(54.2, 21.2) * mm, "end": v(55.2, 21.59) * mm});
            skLineSegment(sketch, "E80.17.161.0", {"start": v(54.2, 21.2) * mm, "end": v(54.37, 20.77) * mm});
            skLineSegment(sketch, "E80.2.162.0", {"start": v(53.13, 23.75) * mm, "end": v(52.94, 24.18) * mm});
            skLineSegment(sketch, "E80.3.162.0", {"start": v(53.13, 23.75) * mm, "end": v(54.1, 24.2) * mm});
            skArc(sketch, "E80.6.162.0", {"start": v(55.18, 24.15) * mm, "mid": v(54.65, 24.3) * mm, "end": v(54.1, 24.2) * mm});
            skArc(sketch, "E80.10.162.0", {"start": v(54.5, 23.33) * mm, "mid": v(54.93, 23.65) * mm, "end": v(55.18, 24.15) * mm});
            skLineSegment(sketch, "E80.14.162.0", {"start": v(53.5, 22.92) * mm, "end": v(54.5, 23.33) * mm});
            skLineSegment(sketch, "E80.17.162.0", {"start": v(53.5, 22.92) * mm, "end": v(53.68, 22.49) * mm});
            skLineSegment(sketch, "E80.2.163.0", {"start": v(52.35, 25.43) * mm, "end": v(52.15, 25.84) * mm});
            skLineSegment(sketch, "E80.3.163.0", {"start": v(52.35, 25.43) * mm, "end": v(53.31, 25.9) * mm});
            skArc(sketch, "E80.6.163.0", {"start": v(54.38, 25.89) * mm, "mid": v(53.85, 26.03) * mm, "end": v(53.31, 25.9) * mm});
            skArc(sketch, "E80.10.163.0", {"start": v(53.72, 25.05) * mm, "mid": v(54.16, 25.39) * mm, "end": v(54.38, 25.89) * mm});
            skLineSegment(sketch, "E80.14.163.0", {"start": v(52.75, 24.6) * mm, "end": v(53.72, 25.05) * mm});
            skLineSegment(sketch, "E80.17.163.0", {"start": v(52.75, 24.6) * mm, "end": v(52.94, 24.18) * mm});
            skLineSegment(sketch, "E80.2.164.0", {"start": v(51.52, 27.07) * mm, "end": v(51.3, 27.49) * mm});
            skLineSegment(sketch, "E80.3.164.0", {"start": v(51.52, 27.07) * mm, "end": v(52.47, 27.58) * mm});
            skArc(sketch, "E80.6.164.0", {"start": v(53.53, 27.6) * mm, "mid": v(53, 27.72) * mm, "end": v(52.47, 27.58) * mm});
            skArc(sketch, "E80.10.164.0", {"start": v(52.9, 26.74) * mm, "mid": v(53.32, 27.1) * mm, "end": v(53.53, 27.6) * mm});
            skLineSegment(sketch, "E80.14.164.0", {"start": v(51.94, 26.26) * mm, "end": v(52.9, 26.74) * mm});
            skLineSegment(sketch, "E80.17.164.0", {"start": v(51.94, 26.26) * mm, "end": v(52.15, 25.84) * mm});
            skLineSegment(sketch, "E80.2.165.0", {"start": v(50.64, 28.7) * mm, "end": v(50.4, 29.1) * mm});
            skLineSegment(sketch, "E80.3.165.0", {"start": v(50.64, 28.7) * mm, "end": v(51.56, 29.23) * mm});
            skArc(sketch, "E80.6.165.0", {"start": v(52.63, 29.28) * mm, "mid": v(52.1, 29.39) * mm, "end": v(51.56, 29.23) * mm});
            skArc(sketch, "E80.10.165.0", {"start": v(52.03, 28.4) * mm, "mid": v(52.44, 28.77) * mm, "end": v(52.63, 29.28) * mm});
            skLineSegment(sketch, "E80.14.165.0", {"start": v(51.08, 27.9) * mm, "end": v(52.03, 28.4) * mm});
            skLineSegment(sketch, "E80.17.165.0", {"start": v(51.08, 27.9) * mm, "end": v(51.3, 27.49) * mm});
            skLineSegment(sketch, "E80.2.166.0", {"start": v(49.7, 30.29) * mm, "end": v(49.45, 30.68) * mm});
            skLineSegment(sketch, "E80.3.166.0", {"start": v(49.7, 30.29) * mm, "end": v(50.61, 30.85) * mm});
            skArc(sketch, "E80.6.166.0", {"start": v(51.67, 30.94) * mm, "mid": v(51.13, 31.03) * mm, "end": v(50.61, 30.85) * mm});
            skArc(sketch, "E80.10.166.0", {"start": v(51.1, 30.04) * mm, "mid": v(51.5, 30.42) * mm, "end": v(51.67, 30.94) * mm});
            skLineSegment(sketch, "E80.14.166.0", {"start": v(50.17, 29.5) * mm, "end": v(51.1, 30.04) * mm});
            skLineSegment(sketch, "E80.17.166.0", {"start": v(50.17, 29.5) * mm, "end": v(50.4, 29.1) * mm});
            skLineSegment(sketch, "E80.2.167.0", {"start": v(48.71, 31.85) * mm, "end": v(48.46, 32.24) * mm});
            skLineSegment(sketch, "E80.3.167.0", {"start": v(48.71, 31.85) * mm, "end": v(49.6, 32.45) * mm});
            skArc(sketch, "E80.6.167.0", {"start": v(50.67, 32.56) * mm, "mid": v(50.12, 32.63) * mm, "end": v(49.6, 32.45) * mm});
            skArc(sketch, "E80.10.167.0", {"start": v(50.12, 31.64) * mm, "mid": v(50.5, 32.04) * mm, "end": v(50.67, 32.56) * mm});
            skLineSegment(sketch, "E80.14.167.0", {"start": v(49.2, 31.08) * mm, "end": v(50.12, 31.64) * mm});
            skLineSegment(sketch, "E80.17.167.0", {"start": v(49.2, 31.08) * mm, "end": v(49.45, 30.68) * mm});
            skLineSegment(sketch, "E80.2.168.0", {"start": v(47.68, 33.38) * mm, "end": v(47.4, 33.76) * mm});
            skLineSegment(sketch, "E80.3.168.0", {"start": v(47.68, 33.38) * mm, "end": v(48.55, 34) * mm});
            skArc(sketch, "E80.6.168.0", {"start": v(49.6, 34.15) * mm, "mid": v(49.06, 34.2) * mm, "end": v(48.55, 34) * mm});
            skArc(sketch, "E80.10.168.0", {"start": v(49.1, 33.22) * mm, "mid": v(49.46, 33.62) * mm, "end": v(49.6, 34.15) * mm});
            skLineSegment(sketch, "E80.14.168.0", {"start": v(48.2, 32.63) * mm, "end": v(49.1, 33.22) * mm});
            skLineSegment(sketch, "E80.17.168.0", {"start": v(48.2, 32.63) * mm, "end": v(48.46, 32.24) * mm});
            skLineSegment(sketch, "E80.2.169.0", {"start": v(46.6, 34.88) * mm, "end": v(46.31, 35.25) * mm});
            skLineSegment(sketch, "E80.3.169.0", {"start": v(46.6, 34.88) * mm, "end": v(47.45, 35.53) * mm});
            skArc(sketch, "E80.6.169.0", {"start": v(48.5, 35.7) * mm, "mid": v(47.95, 35.75) * mm, "end": v(47.45, 35.53) * mm});
            skArc(sketch, "E80.10.169.0", {"start": v(48.01, 34.76) * mm, "mid": v(48.37, 35.18) * mm, "end": v(48.5, 35.7) * mm});
            skLineSegment(sketch, "E80.14.169.0", {"start": v(47.14, 34.14) * mm, "end": v(48.01, 34.76) * mm});
            skLineSegment(sketch, "E80.17.169.0", {"start": v(47.14, 34.14) * mm, "end": v(47.4, 33.76) * mm});
            skLineSegment(sketch, "E80.2.170.0", {"start": v(45.47, 36.34) * mm, "end": v(45.17, 36.7) * mm});
            skLineSegment(sketch, "E80.3.170.0", {"start": v(45.47, 36.34) * mm, "end": v(46.3, 37.01) * mm});
            skArc(sketch, "E80.6.170.0", {"start": v(47.34, 37.23) * mm, "mid": v(46.8, 37.25) * mm, "end": v(46.3, 37.01) * mm});
            skArc(sketch, "E80.10.170.0", {"start": v(46.89, 36.27) * mm, "mid": v(47.23, 36.7) * mm, "end": v(47.34, 37.23) * mm});
            skLineSegment(sketch, "E80.14.170.0", {"start": v(46.03, 35.62) * mm, "end": v(46.89, 36.27) * mm});
            skLineSegment(sketch, "E80.17.170.0", {"start": v(46.03, 35.62) * mm, "end": v(46.31, 35.25) * mm});
            skLineSegment(sketch, "E80.2.171.0", {"start": v(44.3, 37.76) * mm, "end": v(43.98, 38.11) * mm});
            skLineSegment(sketch, "E80.3.171.0", {"start": v(44.3, 37.76) * mm, "end": v(45.1, 38.46) * mm});
            skArc(sketch, "E80.6.171.0", {"start": v(46.14, 38.71) * mm, "mid": v(45.59, 38.72) * mm, "end": v(45.1, 38.46) * mm});
            skArc(sketch, "E80.10.171.0", {"start": v(45.71, 37.74) * mm, "mid": v(46.04, 38.17) * mm, "end": v(46.14, 38.71) * mm});
            skLineSegment(sketch, "E80.14.171.0", {"start": v(44.88, 37.06) * mm, "end": v(45.71, 37.74) * mm});
            skLineSegment(sketch, "E80.17.171.0", {"start": v(44.88, 37.06) * mm, "end": v(45.17, 36.7) * mm});
            skLineSegment(sketch, "E80.2.172.0", {"start": v(43.07, 39.15) * mm, "end": v(42.75, 39.49) * mm});
            skLineSegment(sketch, "E80.3.172.0", {"start": v(43.07, 39.15) * mm, "end": v(43.86, 39.88) * mm});
            skArc(sketch, "E80.6.172.0", {"start": v(44.89, 40.16) * mm, "mid": v(44.34, 40.14) * mm, "end": v(43.86, 39.88) * mm});
            skArc(sketch, "E80.10.172.0", {"start": v(44.5, 39.17) * mm, "mid": v(44.8, 39.61) * mm, "end": v(44.89, 40.16) * mm});
            skLineSegment(sketch, "E80.14.172.0", {"start": v(43.68, 38.47) * mm, "end": v(44.5, 39.17) * mm});
            skLineSegment(sketch, "E80.17.172.0", {"start": v(43.68, 38.47) * mm, "end": v(43.98, 38.11) * mm});
            skLineSegment(sketch, "E80.2.173.0", {"start": v(41.8, 40.5) * mm, "end": v(41.48, 40.83) * mm});
            skLineSegment(sketch, "E80.3.173.0", {"start": v(41.8, 40.5) * mm, "end": v(42.57, 41.25) * mm});
            skArc(sketch, "E80.6.173.0", {"start": v(43.59, 41.56) * mm, "mid": v(43.04, 41.53) * mm, "end": v(42.57, 41.25) * mm});
            skArc(sketch, "E80.10.173.0", {"start": v(43.23, 40.56) * mm, "mid": v(43.53, 41.02) * mm, "end": v(43.59, 41.56) * mm});
            skLineSegment(sketch, "E80.14.173.0", {"start": v(42.44, 39.83) * mm, "end": v(43.23, 40.56) * mm});
            skLineSegment(sketch, "E80.17.173.0", {"start": v(42.44, 39.83) * mm, "end": v(42.75, 39.49) * mm});
            skLineSegment(sketch, "E80.2.174.0", {"start": v(40.5, 41.8) * mm, "end": v(40.16, 42.12) * mm});
            skLineSegment(sketch, "E80.3.174.0", {"start": v(40.5, 41.8) * mm, "end": v(41.24, 42.58) * mm});
            skArc(sketch, "E80.6.174.0", {"start": v(42.25, 42.92) * mm, "mid": v(41.7, 42.87) * mm, "end": v(41.24, 42.58) * mm});
            skArc(sketch, "E80.10.174.0", {"start": v(41.92, 41.9) * mm, "mid": v(42.2, 42.38) * mm, "end": v(42.25, 42.92) * mm});
            skLineSegment(sketch, "E80.14.174.0", {"start": v(41.15, 41.16) * mm, "end": v(41.92, 41.9) * mm});
            skLineSegment(sketch, "E80.17.174.0", {"start": v(41.15, 41.16) * mm, "end": v(41.48, 40.83) * mm});
            skLineSegment(sketch, "E80.2.175.0", {"start": v(39.15, 43.06) * mm, "end": v(38.8, 43.37) * mm});
            skLineSegment(sketch, "E80.3.175.0", {"start": v(39.15, 43.06) * mm, "end": v(39.87, 43.86) * mm});
            skArc(sketch, "E80.6.175.0", {"start": v(40.87, 44.24) * mm, "mid": v(40.32, 44.18) * mm, "end": v(39.87, 43.86) * mm});
            skArc(sketch, "E80.10.175.0", {"start": v(40.57, 43.22) * mm, "mid": v(40.84, 43.7) * mm, "end": v(40.87, 44.24) * mm});
            skLineSegment(sketch, "E80.14.175.0", {"start": v(39.82, 42.44) * mm, "end": v(40.57, 43.22) * mm});
            skLineSegment(sketch, "E80.17.175.0", {"start": v(39.82, 42.44) * mm, "end": v(40.16, 42.12) * mm});
            skLineSegment(sketch, "E80.2.176.0", {"start": v(37.77, 44.28) * mm, "end": v(37.41, 44.58) * mm});
            skLineSegment(sketch, "E80.3.176.0", {"start": v(37.77, 44.28) * mm, "end": v(38.46, 45.1) * mm});
            skArc(sketch, "E80.6.176.0", {"start": v(39.44, 45.52) * mm, "mid": v(38.9, 45.43) * mm, "end": v(38.46, 45.1) * mm});
            skArc(sketch, "E80.10.176.0", {"start": v(39.17, 44.48) * mm, "mid": v(39.43, 44.97) * mm, "end": v(39.44, 45.52) * mm});
            skLineSegment(sketch, "E80.14.176.0", {"start": v(38.46, 43.69) * mm, "end": v(39.17, 44.48) * mm});
            skLineSegment(sketch, "E80.17.176.0", {"start": v(38.46, 43.69) * mm, "end": v(38.8, 43.37) * mm});
            skLineSegment(sketch, "E80.2.177.0", {"start": v(36.34, 45.46) * mm, "end": v(35.98, 45.75) * mm});
            skLineSegment(sketch, "E80.3.177.0", {"start": v(36.34, 45.46) * mm, "end": v(37, 46.3) * mm});
            skArc(sketch, "E80.6.177.0", {"start": v(37.98, 46.75) * mm, "mid": v(37.44, 46.64) * mm, "end": v(37, 46.3) * mm});
            skArc(sketch, "E80.10.177.0", {"start": v(37.74, 45.7) * mm, "mid": v(37.99, 46.2) * mm, "end": v(37.98, 46.75) * mm});
            skLineSegment(sketch, "E80.14.177.0", {"start": v(37.05, 44.88) * mm, "end": v(37.74, 45.7) * mm});
            skLineSegment(sketch, "E80.17.177.0", {"start": v(37.05, 44.88) * mm, "end": v(37.41, 44.58) * mm});
            skLineSegment(sketch, "E80.2.178.0", {"start": v(34.88, 46.6) * mm, "end": v(34.5, 46.87) * mm});
            skLineSegment(sketch, "E80.3.178.0", {"start": v(34.88, 46.6) * mm, "end": v(35.52, 47.45) * mm});
            skArc(sketch, "E80.6.178.0", {"start": v(36.47, 47.93) * mm, "mid": v(35.94, 47.8) * mm, "end": v(35.52, 47.45) * mm});
            skArc(sketch, "E80.10.178.0", {"start": v(36.27, 46.88) * mm, "mid": v(36.5, 47.38) * mm, "end": v(36.47, 47.93) * mm});
            skLineSegment(sketch, "E80.14.178.0", {"start": v(35.61, 46.04) * mm, "end": v(36.27, 46.88) * mm});
            skLineSegment(sketch, "E80.17.178.0", {"start": v(35.61, 46.04) * mm, "end": v(35.98, 45.75) * mm});
            skLineSegment(sketch, "E80.2.179.0", {"start": v(33.39, 47.67) * mm, "end": v(33, 47.94) * mm});
            skLineSegment(sketch, "E80.3.179.0", {"start": v(33.39, 47.67) * mm, "end": v(34, 48.56) * mm});
            skArc(sketch, "E80.6.179.0", {"start": v(34.94, 49.06) * mm, "mid": v(34.4, 48.92) * mm, "end": v(34, 48.56) * mm});
            skArc(sketch, "E80.10.179.0", {"start": v(34.77, 48) * mm, "mid": v(34.98, 48.51) * mm, "end": v(34.94, 49.06) * mm});
            skLineSegment(sketch, "E80.14.179.0", {"start": v(34.13, 47.14) * mm, "end": v(34.77, 48) * mm});
            skLineSegment(sketch, "E80.17.179.0", {"start": v(34.13, 47.14) * mm, "end": v(34.5, 46.87) * mm});
            skLineSegment(sketch, "E80.2.180.0", {"start": v(31.86, 48.7) * mm, "end": v(31.47, 48.96) * mm});
            skLineSegment(sketch, "E80.3.180.0", {"start": v(31.86, 48.7) * mm, "end": v(32.44, 49.61) * mm});
            skArc(sketch, "E80.6.180.0", {"start": v(33.36, 50.14) * mm, "mid": v(32.83, 50) * mm, "end": v(32.44, 49.61) * mm});
            skArc(sketch, "E80.10.180.0", {"start": v(33.23, 49.08) * mm, "mid": v(33.42, 49.6) * mm, "end": v(33.36, 50.14) * mm});
            skLineSegment(sketch, "E80.14.180.0", {"start": v(32.62, 48.2) * mm, "end": v(33.23, 49.08) * mm});
            skLineSegment(sketch, "E80.17.180.0", {"start": v(32.62, 48.2) * mm, "end": v(33, 47.94) * mm});
            skLineSegment(sketch, "E80.2.181.0", {"start": v(30.3, 49.7) * mm, "end": v(29.9, 49.93) * mm});
            skLineSegment(sketch, "E80.3.181.0", {"start": v(30.3, 49.7) * mm, "end": v(30.85, 50.62) * mm});
            skArc(sketch, "E80.6.181.0", {"start": v(31.75, 51.18) * mm, "mid": v(31.23, 51) * mm, "end": v(30.85, 50.62) * mm});
            skArc(sketch, "E80.10.181.0", {"start": v(31.65, 50.11) * mm, "mid": v(31.83, 50.63) * mm, "end": v(31.75, 51.18) * mm});
            skLineSegment(sketch, "E80.14.181.0", {"start": v(31.07, 49.21) * mm, "end": v(31.65, 50.11) * mm});
            skLineSegment(sketch, "E80.17.181.0", {"start": v(31.07, 49.21) * mm, "end": v(31.47, 48.96) * mm});
            skLineSegment(sketch, "E80.2.182.0", {"start": v(28.7, 50.63) * mm, "end": v(28.3, 50.86) * mm});
            skLineSegment(sketch, "E80.3.182.0", {"start": v(28.7, 50.63) * mm, "end": v(29.22, 51.57) * mm});
            skArc(sketch, "E80.6.182.0", {"start": v(30.11, 52.16) * mm, "mid": v(29.6, 51.97) * mm, "end": v(29.22, 51.57) * mm});
            skArc(sketch, "E80.10.182.0", {"start": v(30.05, 51.1) * mm, "mid": v(30.21, 51.62) * mm, "end": v(30.11, 52.16) * mm});
            skLineSegment(sketch, "E80.14.182.0", {"start": v(29.5, 50.17) * mm, "end": v(30.05, 51.1) * mm});
            skLineSegment(sketch, "E80.17.182.0", {"start": v(29.5, 50.17) * mm, "end": v(29.9, 49.93) * mm});
            skLineSegment(sketch, "E80.2.183.0", {"start": v(27.08, 51.52) * mm, "end": v(26.67, 51.73) * mm});
            skLineSegment(sketch, "E80.3.183.0", {"start": v(27.08, 51.52) * mm, "end": v(27.57, 52.47) * mm});
            skArc(sketch, "E80.6.183.0", {"start": v(28.44, 53.09) * mm, "mid": v(27.93, 52.89) * mm, "end": v(27.57, 52.47) * mm});
            skArc(sketch, "E80.10.183.0", {"start": v(28.41, 52.02) * mm, "mid": v(28.56, 52.55) * mm, "end": v(28.44, 53.09) * mm});
            skLineSegment(sketch, "E80.14.183.0", {"start": v(27.89, 51.08) * mm, "end": v(28.41, 52.02) * mm});
            skLineSegment(sketch, "E80.17.183.0", {"start": v(27.89, 51.08) * mm, "end": v(28.3, 50.86) * mm});
            skLineSegment(sketch, "E80.2.184.0", {"start": v(25.44, 52.35) * mm, "end": v(25.01, 52.55) * mm});
            skLineSegment(sketch, "E80.3.184.0", {"start": v(25.44, 52.35) * mm, "end": v(25.9, 53.32) * mm});
            skArc(sketch, "E80.6.184.0", {"start": v(26.75, 53.96) * mm, "mid": v(26.24, 53.75) * mm, "end": v(25.9, 53.32) * mm});
            skArc(sketch, "E80.10.184.0", {"start": v(26.75, 52.9) * mm, "mid": v(26.88, 53.43) * mm, "end": v(26.75, 53.96) * mm});
            skLineSegment(sketch, "E80.14.184.0", {"start": v(26.25, 51.94) * mm, "end": v(26.75, 52.9) * mm});
            skLineSegment(sketch, "E80.17.184.0", {"start": v(26.25, 51.94) * mm, "end": v(26.67, 51.73) * mm});
            skLineSegment(sketch, "E80.2.185.0", {"start": v(23.76, 53.13) * mm, "end": v(23.33, 53.32) * mm});
            skLineSegment(sketch, "E80.3.185.0", {"start": v(23.76, 53.13) * mm, "end": v(24.19, 54.11) * mm});
            skArc(sketch, "E80.6.185.0", {"start": v(25.02, 54.79) * mm, "mid": v(24.52, 54.55) * mm, "end": v(24.19, 54.11) * mm});
            skArc(sketch, "E80.10.185.0", {"start": v(25.06, 53.72) * mm, "mid": v(25.17, 54.26) * mm, "end": v(25.02, 54.79) * mm});
            skLineSegment(sketch, "E80.14.185.0", {"start": v(24.6, 52.75) * mm, "end": v(25.06, 53.72) * mm});
            skLineSegment(sketch, "E80.17.185.0", {"start": v(24.6, 52.75) * mm, "end": v(25.01, 52.55) * mm});
            skLineSegment(sketch, "E80.2.186.0", {"start": v(22.06, 53.86) * mm, "end": v(21.63, 54.03) * mm});
            skLineSegment(sketch, "E80.3.186.0", {"start": v(22.06, 53.86) * mm, "end": v(22.46, 54.85) * mm});
            skArc(sketch, "E80.6.186.0", {"start": v(23.27, 55.55) * mm, "mid": v(22.78, 55.3) * mm, "end": v(22.46, 54.85) * mm});
            skArc(sketch, "E80.10.186.0", {"start": v(23.34, 54.49) * mm, "mid": v(23.43, 55.03) * mm, "end": v(23.27, 55.55) * mm});
            skLineSegment(sketch, "E80.14.186.0", {"start": v(22.9, 53.5) * mm, "end": v(23.34, 54.49) * mm});
            skLineSegment(sketch, "E80.17.186.0", {"start": v(22.9, 53.5) * mm, "end": v(23.33, 53.32) * mm});
            skLineSegment(sketch, "E80.2.187.0", {"start": v(20.34, 54.53) * mm, "end": v(19.9, 54.7) * mm});
            skLineSegment(sketch, "E80.3.187.0", {"start": v(20.34, 54.53) * mm, "end": v(20.7, 55.54) * mm});
            skArc(sketch, "E80.6.187.0", {"start": v(21.5, 56.26) * mm, "mid": v(21.01, 56) * mm, "end": v(20.7, 55.54) * mm});
            skArc(sketch, "E80.10.187.0", {"start": v(21.6, 55.2) * mm, "mid": v(21.68, 55.74) * mm, "end": v(21.5, 56.26) * mm});
            skLineSegment(sketch, "E80.14.187.0", {"start": v(21.2, 54.2) * mm, "end": v(21.6, 55.2) * mm});
            skLineSegment(sketch, "E80.17.187.0", {"start": v(21.2, 54.2) * mm, "end": v(21.63, 54.03) * mm});
            skLineSegment(sketch, "E80.2.188.0", {"start": v(18.6, 55.15) * mm, "end": v(18.16, 55.3) * mm});
            skLineSegment(sketch, "E80.3.188.0", {"start": v(18.6, 55.15) * mm, "end": v(18.94, 56.17) * mm});
            skArc(sketch, "E80.6.188.0", {"start": v(19.7, 56.92) * mm, "mid": v(19.23, 56.63) * mm, "end": v(18.94, 56.17) * mm});
            skArc(sketch, "E80.10.188.0", {"start": v(19.84, 55.86) * mm, "mid": v(19.9, 56.4) * mm, "end": v(19.7, 56.92) * mm});
            skLineSegment(sketch, "E80.14.188.0", {"start": v(19.47, 54.85) * mm, "end": v(19.84, 55.86) * mm});
            skLineSegment(sketch, "E80.17.188.0", {"start": v(19.47, 54.85) * mm, "end": v(19.9, 54.7) * mm});
            skLineSegment(sketch, "E80.2.189.0", {"start": v(16.84, 55.71) * mm, "end": v(16.4, 55.84) * mm});
            skLineSegment(sketch, "E80.3.189.0", {"start": v(16.84, 55.71) * mm, "end": v(17.14, 56.74) * mm});
            skArc(sketch, "E80.6.189.0", {"start": v(17.88, 57.51) * mm, "mid": v(17.42, 57.22) * mm, "end": v(17.14, 56.74) * mm});
            skArc(sketch, "E80.10.189.0", {"start": v(18.05, 56.46) * mm, "mid": v(18.1, 57) * mm, "end": v(17.88, 57.51) * mm});
            skLineSegment(sketch, "E80.14.189.0", {"start": v(17.72, 55.44) * mm, "end": v(18.05, 56.46) * mm});
            skLineSegment(sketch, "E80.17.189.0", {"start": v(17.72, 55.44) * mm, "end": v(18.16, 55.3) * mm});
            skLineSegment(sketch, "E80.2.190.0", {"start": v(15.07, 56.22) * mm, "end": v(14.62, 56.33) * mm});
            skLineSegment(sketch, "E80.3.190.0", {"start": v(15.07, 56.22) * mm, "end": v(15.34, 57.26) * mm});
            skArc(sketch, "E80.6.190.0", {"start": v(16.05, 58.05) * mm, "mid": v(15.6, 57.74) * mm, "end": v(15.34, 57.26) * mm});
            skArc(sketch, "E80.10.190.0", {"start": v(16.25, 57) * mm, "mid": v(16.28, 57.55) * mm, "end": v(16.05, 58.05) * mm});
            skLineSegment(sketch, "E80.14.190.0", {"start": v(15.95, 55.97) * mm, "end": v(16.25, 57) * mm});
            skLineSegment(sketch, "E80.17.190.0", {"start": v(15.95, 55.97) * mm, "end": v(16.4, 55.84) * mm});
            skLineSegment(sketch, "E80.2.191.0", {"start": v(13.28, 56.67) * mm, "end": v(12.82, 56.77) * mm});
            skLineSegment(sketch, "E80.3.191.0", {"start": v(13.28, 56.67) * mm, "end": v(13.51, 57.71) * mm});
            skArc(sketch, "E80.6.191.0", {"start": v(14.2, 58.53) * mm, "mid": v(13.76, 58.2) * mm, "end": v(13.51, 57.71) * mm});
            skArc(sketch, "E80.10.191.0", {"start": v(14.44, 57.49) * mm, "mid": v(14.44, 58.04) * mm, "end": v(14.2, 58.53) * mm});
            skLineSegment(sketch, "E80.14.191.0", {"start": v(14.17, 56.45) * mm, "end": v(14.44, 57.49) * mm});
            skLineSegment(sketch, "E80.17.191.0", {"start": v(14.17, 56.45) * mm, "end": v(14.62, 56.33) * mm});
            skLineSegment(sketch, "E80.2.192.0", {"start": v(11.47, 57.06) * mm, "end": v(11.01, 57.15) * mm});
            skLineSegment(sketch, "E80.3.192.0", {"start": v(11.47, 57.06) * mm, "end": v(11.67, 58.11) * mm});
            skArc(sketch, "E80.6.192.0", {"start": v(12.34, 58.95) * mm, "mid": v(11.9, 58.61) * mm, "end": v(11.67, 58.11) * mm});
            skArc(sketch, "E80.10.192.0", {"start": v(12.6, 57.92) * mm, "mid": v(12.6, 58.47) * mm, "end": v(12.34, 58.95) * mm});
            skLineSegment(sketch, "E80.14.192.0", {"start": v(12.37, 56.87) * mm, "end": v(12.6, 57.92) * mm});
            skLineSegment(sketch, "E80.17.192.0", {"start": v(12.37, 56.87) * mm, "end": v(12.82, 56.77) * mm});
            skLineSegment(sketch, "E80.2.193.0", {"start": v(9.66, 57.4) * mm, "end": v(9.2, 57.47) * mm});
            skLineSegment(sketch, "E80.3.193.0", {"start": v(9.66, 57.4) * mm, "end": v(9.82, 58.45) * mm});
            skArc(sketch, "E80.6.193.0", {"start": v(10.46, 59.31) * mm, "mid": v(10.04, 58.96) * mm, "end": v(9.82, 58.45) * mm});
            skArc(sketch, "E80.10.193.0", {"start": v(10.76, 58.29) * mm, "mid": v(10.73, 58.84) * mm, "end": v(10.46, 59.31) * mm});
            skLineSegment(sketch, "E80.14.193.0", {"start": v(10.56, 57.24) * mm, "end": v(10.76, 58.29) * mm});
            skLineSegment(sketch, "E80.17.193.0", {"start": v(10.56, 57.24) * mm, "end": v(11.01, 57.15) * mm});
            skLineSegment(sketch, "E80.2.194.0", {"start": v(7.83, 57.67) * mm, "end": v(7.37, 57.73) * mm});
            skLineSegment(sketch, "E80.3.194.0", {"start": v(7.83, 57.67) * mm, "end": v(7.96, 58.74) * mm});
            skArc(sketch, "E80.6.194.0", {"start": v(8.57, 59.62) * mm, "mid": v(8.16, 59.25) * mm, "end": v(7.96, 58.74) * mm});
            skArc(sketch, "E80.10.194.0", {"start": v(8.9, 58.6) * mm, "mid": v(8.86, 59.15) * mm, "end": v(8.57, 59.62) * mm});
            skLineSegment(sketch, "E80.14.194.0", {"start": v(8.74, 57.54) * mm, "end": v(8.9, 58.6) * mm});
            skLineSegment(sketch, "E80.17.194.0", {"start": v(8.74, 57.54) * mm, "end": v(9.2, 57.47) * mm});
            skLineSegment(sketch, "E80.2.195.0", {"start": v(6, 57.9) * mm, "end": v(5.53, 57.94) * mm});
            skLineSegment(sketch, "E80.3.195.0", {"start": v(6, 57.9) * mm, "end": v(6.1, 58.96) * mm});
            skArc(sketch, "E80.6.195.0", {"start": v(6.68, 59.86) * mm, "mid": v(6.28, 59.48) * mm, "end": v(6.1, 58.96) * mm});
            skArc(sketch, "E80.10.195.0", {"start": v(7.04, 58.85) * mm, "mid": v(6.98, 59.4) * mm, "end": v(6.68, 59.86) * mm});
            skLineSegment(sketch, "E80.14.195.0", {"start": v(6.9, 57.8) * mm, "end": v(7.04, 58.85) * mm});
            skLineSegment(sketch, "E80.17.195.0", {"start": v(6.9, 57.8) * mm, "end": v(7.37, 57.73) * mm});
            skLineSegment(sketch, "E80.2.196.0", {"start": v(4.16, 58.05) * mm, "end": v(3.7, 58.08) * mm});
            skLineSegment(sketch, "E80.3.196.0", {"start": v(4.16, 58.05) * mm, "end": v(4.22, 59.12) * mm});
            skArc(sketch, "E80.6.196.0", {"start": v(4.77, 60.04) * mm, "mid": v(4.39, 59.65) * mm, "end": v(4.22, 59.12) * mm});
            skArc(sketch, "E80.10.196.0", {"start": v(5.17, 59.05) * mm, "mid": v(5.1, 59.6) * mm, "end": v(4.77, 60.04) * mm});
            skLineSegment(sketch, "E80.14.196.0", {"start": v(5.07, 57.98) * mm, "end": v(5.17, 59.05) * mm});
            skLineSegment(sketch, "E80.17.196.0", {"start": v(5.07, 57.98) * mm, "end": v(5.53, 57.94) * mm});
            skLineSegment(sketch, "E80.2.197.0", {"start": v(2.31, 58.16) * mm, "end": v(1.85, 58.17) * mm});
            skLineSegment(sketch, "E80.3.197.0", {"start": v(2.31, 58.16) * mm, "end": v(2.35, 59.23) * mm});
            skArc(sketch, "E80.6.197.0", {"start": v(2.87, 60.16) * mm, "mid": v(2.5, 59.76) * mm, "end": v(2.35, 59.23) * mm});
            skArc(sketch, "E80.10.197.0", {"start": v(3.3, 59.18) * mm, "mid": v(3.2, 59.72) * mm, "end": v(2.87, 60.16) * mm});
            skLineSegment(sketch, "E80.14.197.0", {"start": v(3.23, 58.11) * mm, "end": v(3.3, 59.18) * mm});
            skLineSegment(sketch, "E80.17.197.0", {"start": v(3.23, 58.11) * mm, "end": v(3.7, 58.08) * mm});
            skSolve(sketch);
        }
        {
            var Q0;
            Q0=makeQuery(id+"F13.imprint","IMPRINT",FACE,{"disambiguationData":[TD([[makeQuery(id+"F13.imprint","IMPRINT",EDGE,{"derivedFrom":sQuery(id+"F13.wireOp",EDGE,"E42")}),1.0]])]});
            var Q1;
            Q1=makeQuery(id+"F13.imprint","IMPRINT",FACE,{"disambiguationData":[TD([[makeQuery(id+"F13.imprint","IMPRINT",EDGE,{"derivedFrom":sQuery(id+"F13.wireOp",EDGE,"E41")}),-1.0]])]});
            extrude(context, id + "F14", {"entities" : qUnion([Q0, Q1]), "depth" : 1.59 * mm});
        }
    });
